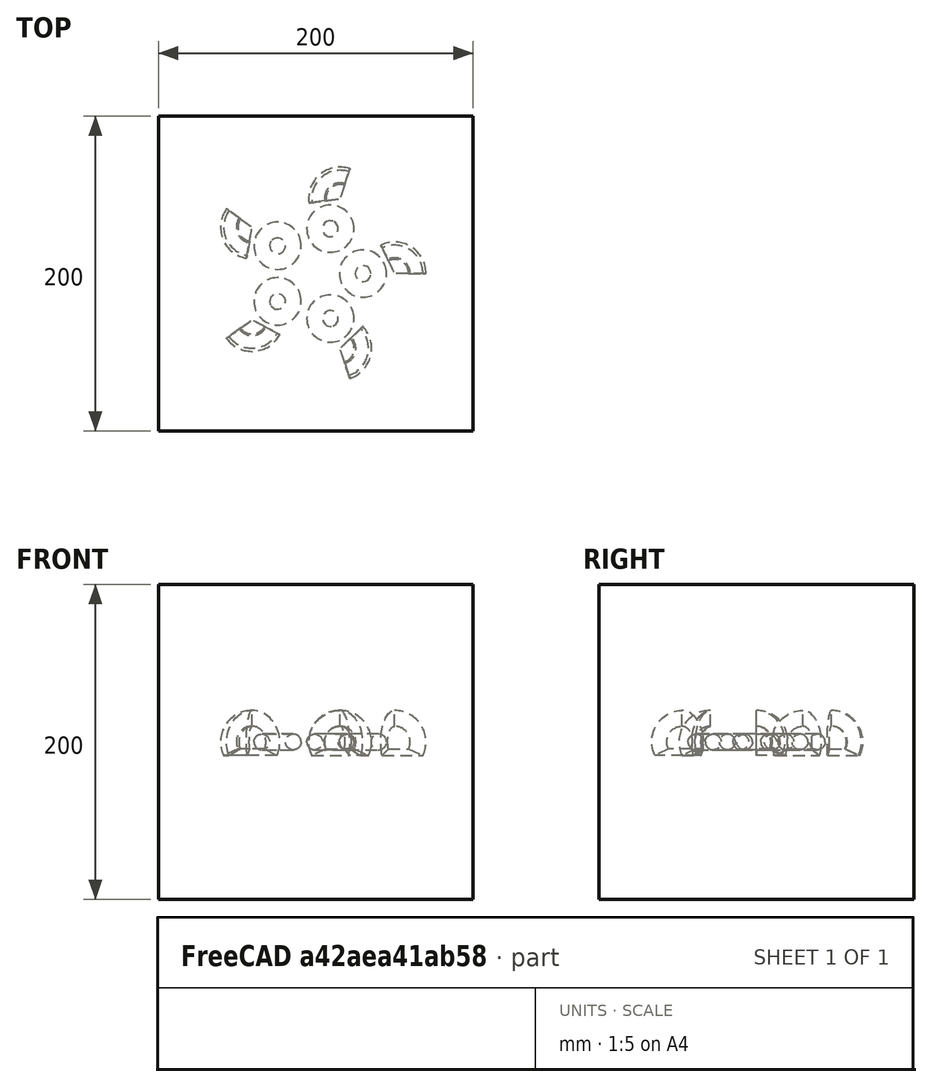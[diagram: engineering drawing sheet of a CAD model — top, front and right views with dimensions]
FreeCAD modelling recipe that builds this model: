
FCSTD DOCUMENT  (FreeCAD 0.19RUnknown)
Label: polarArray
License: All rights reserved
LicenseURL: http://en.wikipedia.org/wiki/All_rights_reserved
objects: App::DocumentObjectGroupPython×1248, Part::FeaturePython×4, App::Part×2, Part::MultiFuse×1
note: 5 computed .brp shape members not serialized (recipe doc carries the construction recipe); baked Part::Feature solids carry a one-line shape summary decoded from their .brp

FEATURE [App::DocumentObjectGroupPython] HALFPI  # scripted group (container) (typed FeaturePython)
  name = HALFPI
  value = pi/2.
FEATURE [App::DocumentObjectGroupPython] PI  # scripted group (container) (typed FeaturePython)
  name = PI
  value = 1.*pi
FEATURE [App::DocumentObjectGroupPython] TWOPI  # scripted group (container) (typed FeaturePython)
  name = TWOPI
  value = 2.*pi
FEATURE [App::DocumentObjectGroupPython] Constants  # scripted group (container) (typed FeaturePython)
  Group = -> [HALFPI,PI,TWOPI]
FEATURE [App::DocumentObjectGroupPython] Variables  # scripted group (container) (typed FeaturePython)
FEATURE [App::DocumentObjectGroupPython] Quantities  # scripted group (container) (typed FeaturePython)
FEATURE [App::DocumentObjectGroupPython] Isotopes  # scripted group (container) (typed FeaturePython)
FEATURE [App::DocumentObjectGroupPython] Elements  # scripted group (container) (typed FeaturePython)
FEATURE [App::DocumentObjectGroupPython] G4Isotopes  # scripted group (container) (typed FeaturePython)
FEATURE [App::DocumentObjectGroupPython] H_element  # scripted group (container) (typed FeaturePython)
  Z = 1
  atom_value = 1.008
  formula = H
  name = H_element
FEATURE [App::DocumentObjectGroupPython] He_element  # scripted group (container) (typed FeaturePython)
  Z = 2
  atom_value = 4.0026
  formula = He
  name = He_element
FEATURE [App::DocumentObjectGroupPython] Li_element  # scripted group (container) (typed FeaturePython)
  Z = 3
  atom_value = 6.94
  formula = Li
  name = Li_element
FEATURE [App::DocumentObjectGroupPython] Be_element  # scripted group (container) (typed FeaturePython)
  Z = 4
  atom_value = 9.01218
  formula = Be
  name = Be_element
FEATURE [App::DocumentObjectGroupPython] B_element  # scripted group (container) (typed FeaturePython)
  Z = 5
  atom_value = 10.81
  formula = B
  name = B_element
FEATURE [App::DocumentObjectGroupPython] C_element  # scripted group (container) (typed FeaturePython)
  Z = 6
  atom_value = 12.011
  formula = C
  name = C_element
FEATURE [App::DocumentObjectGroupPython] N_element  # scripted group (container) (typed FeaturePython)
  Z = 7
  atom_value = 14.007
  formula = N
  name = N_element
FEATURE [App::DocumentObjectGroupPython] O_element  # scripted group (container) (typed FeaturePython)
  Z = 8
  atom_value = 15.999
  formula = O
  name = O_element
FEATURE [App::DocumentObjectGroupPython] F_element  # scripted group (container) (typed FeaturePython)
  Z = 9
  atom_value = 18.9984
  formula = F
  name = F_element
FEATURE [App::DocumentObjectGroupPython] Ne_element  # scripted group (container) (typed FeaturePython)
  Z = 10
  atom_value = 20.1797
  formula = Ne
  name = Ne_element
FEATURE [App::DocumentObjectGroupPython] Na_element  # scripted group (container) (typed FeaturePython)
  Z = 11
  atom_value = 22.9898
  formula = Na
  name = Na_element
FEATURE [App::DocumentObjectGroupPython] Mg_element  # scripted group (container) (typed FeaturePython)
  Z = 12
  atom_value = 24.305
  formula = Mg
  name = Mg_element
FEATURE [App::DocumentObjectGroupPython] Al_element  # scripted group (container) (typed FeaturePython)
  Z = 13
  atom_value = 26.9815
  formula = Al
  name = Al_element
FEATURE [App::DocumentObjectGroupPython] Si_element  # scripted group (container) (typed FeaturePython)
  Z = 14
  atom_value = 28.085
  formula = Si
  name = Si_element
FEATURE [App::DocumentObjectGroupPython] P_element  # scripted group (container) (typed FeaturePython)
  Z = 15
  atom_value = 30.9738
  formula = P
  name = P_element
FEATURE [App::DocumentObjectGroupPython] S_element  # scripted group (container) (typed FeaturePython)
  Z = 16
  atom_value = 32.06
  formula = S
  name = S_element
FEATURE [App::DocumentObjectGroupPython] Cl_element  # scripted group (container) (typed FeaturePython)
  Z = 17
  atom_value = 35.45
  formula = Cl
  name = Cl_element
FEATURE [App::DocumentObjectGroupPython] Ar_element  # scripted group (container) (typed FeaturePython)
  Z = 18
  atom_value = 39.95
  formula = Ar
  name = Ar_element
FEATURE [App::DocumentObjectGroupPython] K_element  # scripted group (container) (typed FeaturePython)
  Z = 19
  atom_value = 39.0983
  formula = K
  name = K_element
FEATURE [App::DocumentObjectGroupPython] Ca_element  # scripted group (container) (typed FeaturePython)
  Z = 20
  atom_value = 40.078
  formula = Ca
  name = Ca_element
FEATURE [App::DocumentObjectGroupPython] Sc_element  # scripted group (container) (typed FeaturePython)
  Z = 21
  atom_value = 44.9559
  formula = Sc
  name = Sc_element
FEATURE [App::DocumentObjectGroupPython] Ti_element  # scripted group (container) (typed FeaturePython)
  Z = 22
  atom_value = 47.867
  formula = Ti
  name = Ti_element
FEATURE [App::DocumentObjectGroupPython] V_element  # scripted group (container) (typed FeaturePython)
  Z = 23
  atom_value = 50.9415
  formula = V
  name = V_element
FEATURE [App::DocumentObjectGroupPython] Cr_element  # scripted group (container) (typed FeaturePython)
  Z = 24
  atom_value = 51.9961
  formula = Cr
  name = Cr_element
FEATURE [App::DocumentObjectGroupPython] Mn_element  # scripted group (container) (typed FeaturePython)
  Z = 25
  atom_value = 54.938
  formula = Mn
  name = Mn_element
FEATURE [App::DocumentObjectGroupPython] Fe_element  # scripted group (container) (typed FeaturePython)
  Z = 26
  atom_value = 55.845
  formula = Fe
  name = Fe_element
FEATURE [App::DocumentObjectGroupPython] Co_element  # scripted group (container) (typed FeaturePython)
  Z = 27
  atom_value = 58.9332
  formula = Co
  name = Co_element
FEATURE [App::DocumentObjectGroupPython] Ni_element  # scripted group (container) (typed FeaturePython)
  Z = 28
  atom_value = 58.6934
  formula = Ni
  name = Ni_element
FEATURE [App::DocumentObjectGroupPython] Cu_element  # scripted group (container) (typed FeaturePython)
  Z = 29
  atom_value = 63.546
  formula = Cu
  name = Cu_element
FEATURE [App::DocumentObjectGroupPython] Zn_element  # scripted group (container) (typed FeaturePython)
  Z = 30
  atom_value = 65.38
  formula = Zn
  name = Zn_element
FEATURE [App::DocumentObjectGroupPython] Ga_element  # scripted group (container) (typed FeaturePython)
  Z = 31
  atom_value = 69.723
  formula = Ga
  name = Ga_element
FEATURE [App::DocumentObjectGroupPython] Ge_element  # scripted group (container) (typed FeaturePython)
  Z = 32
  atom_value = 72.63
  formula = Ge
  name = Ge_element
FEATURE [App::DocumentObjectGroupPython] As_element  # scripted group (container) (typed FeaturePython)
  Z = 33
  atom_value = 74.9216
  formula = As
  name = As_element
FEATURE [App::DocumentObjectGroupPython] Se_element  # scripted group (container) (typed FeaturePython)
  Z = 34
  atom_value = 78.971
  formula = Se
  name = Se_element
FEATURE [App::DocumentObjectGroupPython] Br_element  # scripted group (container) (typed FeaturePython)
  Z = 35
  atom_value = 79.904
  formula = Br
  name = Br_element
FEATURE [App::DocumentObjectGroupPython] Kr_element  # scripted group (container) (typed FeaturePython)
  Z = 36
  atom_value = 83.798
  formula = Kr
  name = Kr_element
FEATURE [App::DocumentObjectGroupPython] Rb_element  # scripted group (container) (typed FeaturePython)
  Z = 37
  atom_value = 85.4678
  formula = Rb
  name = Rb_element
FEATURE [App::DocumentObjectGroupPython] Sr_element  # scripted group (container) (typed FeaturePython)
  Z = 38
  atom_value = 87.62
  formula = Sr
  name = Sr_element
FEATURE [App::DocumentObjectGroupPython] Y_element  # scripted group (container) (typed FeaturePython)
  Z = 39
  atom_value = 88.9058
  formula = Y
  name = Y_element
FEATURE [App::DocumentObjectGroupPython] Zr_element  # scripted group (container) (typed FeaturePython)
  Z = 40
  atom_value = 91.224
  formula = Zr
  name = Zr_element
FEATURE [App::DocumentObjectGroupPython] Nb_element  # scripted group (container) (typed FeaturePython)
  Z = 41
  atom_value = 92.9064
  formula = Nb
  name = Nb_element
FEATURE [App::DocumentObjectGroupPython] Mo_element  # scripted group (container) (typed FeaturePython)
  Z = 42
  atom_value = 95.95
  formula = Mo
  name = Mo_element
FEATURE [App::DocumentObjectGroupPython] Tc_element  # scripted group (container) (typed FeaturePython)
  Z = 43
  atom_value = 97
  formula = Tc
  name = Tc_element
FEATURE [App::DocumentObjectGroupPython] Ru_element  # scripted group (container) (typed FeaturePython)
  Z = 44
  atom_value = 101.07
  formula = Ru
  name = Ru_element
FEATURE [App::DocumentObjectGroupPython] Rh_element  # scripted group (container) (typed FeaturePython)
  Z = 45
  atom_value = 102.905
  formula = Rh
  name = Rh_element
FEATURE [App::DocumentObjectGroupPython] Pd_element  # scripted group (container) (typed FeaturePython)
  Z = 46
  atom_value = 106.42
  formula = Pd
  name = Pd_element
FEATURE [App::DocumentObjectGroupPython] Ag_element  # scripted group (container) (typed FeaturePython)
  Z = 47
  atom_value = 107.868
  formula = Ag
  name = Ag_element
FEATURE [App::DocumentObjectGroupPython] Cd_element  # scripted group (container) (typed FeaturePython)
  Z = 48
  atom_value = 112.414
  formula = Cd
  name = Cd_element
FEATURE [App::DocumentObjectGroupPython] In_element  # scripted group (container) (typed FeaturePython)
  Z = 49
  atom_value = 114.818
  formula = In
  name = In_element
FEATURE [App::DocumentObjectGroupPython] Sn_element  # scripted group (container) (typed FeaturePython)
  Z = 50
  atom_value = 118.71
  formula = Sn
  name = Sn_element
FEATURE [App::DocumentObjectGroupPython] Sb_element  # scripted group (container) (typed FeaturePython)
  Z = 51
  atom_value = 121.76
  formula = Sb
  name = Sb_element
FEATURE [App::DocumentObjectGroupPython] Te_element  # scripted group (container) (typed FeaturePython)
  Z = 52
  atom_value = 127.6
  formula = Te
  name = Te_element
FEATURE [App::DocumentObjectGroupPython] I_element  # scripted group (container) (typed FeaturePython)
  Z = 53
  atom_value = 126.904
  formula = I
  name = I_element
FEATURE [App::DocumentObjectGroupPython] Xe_element  # scripted group (container) (typed FeaturePython)
  Z = 54
  atom_value = 131.293
  formula = Xe
  name = Xe_element
FEATURE [App::DocumentObjectGroupPython] Cs_element  # scripted group (container) (typed FeaturePython)
  Z = 55
  atom_value = 132.905
  formula = Cs
  name = Cs_element
FEATURE [App::DocumentObjectGroupPython] Ba_element  # scripted group (container) (typed FeaturePython)
  Z = 56
  atom_value = 137.327
  formula = Ba
  name = Ba_element
FEATURE [App::DocumentObjectGroupPython] La_element  # scripted group (container) (typed FeaturePython)
  Z = 57
  atom_value = 138.905
  formula = La
  name = La_element
FEATURE [App::DocumentObjectGroupPython] Ce_element  # scripted group (container) (typed FeaturePython)
  Z = 58
  atom_value = 140.116
  formula = Ce
  name = Ce_element
FEATURE [App::DocumentObjectGroupPython] Pr_element  # scripted group (container) (typed FeaturePython)
  Z = 59
  atom_value = 140.908
  formula = Pr
  name = Pr_element
FEATURE [App::DocumentObjectGroupPython] Nd_element  # scripted group (container) (typed FeaturePython)
  Z = 60
  atom_value = 144.242
  formula = Nd
  name = Nd_element
FEATURE [App::DocumentObjectGroupPython] Pm_element  # scripted group (container) (typed FeaturePython)
  Z = 61
  atom_value = 145
  formula = Pm
  name = Pm_element
FEATURE [App::DocumentObjectGroupPython] Sm_element  # scripted group (container) (typed FeaturePython)
  Z = 62
  atom_value = 150.36
  formula = Sm
  name = Sm_element
FEATURE [App::DocumentObjectGroupPython] Eu_element  # scripted group (container) (typed FeaturePython)
  Z = 63
  atom_value = 151.964
  formula = Eu
  name = Eu_element
FEATURE [App::DocumentObjectGroupPython] Gd_element  # scripted group (container) (typed FeaturePython)
  Z = 64
  atom_value = 157.25
  formula = Gd
  name = Gd_element
FEATURE [App::DocumentObjectGroupPython] Tb_element  # scripted group (container) (typed FeaturePython)
  Z = 65
  atom_value = 158.925
  formula = Tb
  name = Tb_element
FEATURE [App::DocumentObjectGroupPython] Dy_element  # scripted group (container) (typed FeaturePython)
  Z = 66
  atom_value = 162.5
  formula = Dy
  name = Dy_element
FEATURE [App::DocumentObjectGroupPython] Ho_element  # scripted group (container) (typed FeaturePython)
  Z = 67
  atom_value = 164.93
  formula = Ho
  name = Ho_element
FEATURE [App::DocumentObjectGroupPython] Er_element  # scripted group (container) (typed FeaturePython)
  Z = 68
  atom_value = 167.259
  formula = Er
  name = Er_element
FEATURE [App::DocumentObjectGroupPython] Tm_element  # scripted group (container) (typed FeaturePython)
  Z = 69
  atom_value = 168.934
  formula = Tm
  name = Tm_element
FEATURE [App::DocumentObjectGroupPython] Yb_element  # scripted group (container) (typed FeaturePython)
  Z = 70
  atom_value = 173.045
  formula = Yb
  name = Yb_element
FEATURE [App::DocumentObjectGroupPython] Lu_element  # scripted group (container) (typed FeaturePython)
  Z = 71
  atom_value = 174.967
  formula = Lu
  name = Lu_element
FEATURE [App::DocumentObjectGroupPython] Hf_element  # scripted group (container) (typed FeaturePython)
  Z = 72
  atom_value = 178.49
  formula = Hf
  name = Hf_element
FEATURE [App::DocumentObjectGroupPython] Ta_element  # scripted group (container) (typed FeaturePython)
  Z = 73
  atom_value = 180.948
  formula = Ta
  name = Ta_element
FEATURE [App::DocumentObjectGroupPython] W_element  # scripted group (container) (typed FeaturePython)
  Z = 74
  atom_value = 183.84
  formula = W
  name = W_element
FEATURE [App::DocumentObjectGroupPython] Re_element  # scripted group (container) (typed FeaturePython)
  Z = 75
  atom_value = 186.207
  formula = Re
  name = Re_element
FEATURE [App::DocumentObjectGroupPython] Os_element  # scripted group (container) (typed FeaturePython)
  Z = 76
  atom_value = 190.23
  formula = Os
  name = Os_element
FEATURE [App::DocumentObjectGroupPython] Ir_element  # scripted group (container) (typed FeaturePython)
  Z = 77
  atom_value = 192.217
  formula = Ir
  name = Ir_element
FEATURE [App::DocumentObjectGroupPython] Pt_element  # scripted group (container) (typed FeaturePython)
  Z = 78
  atom_value = 195.084
  formula = Pt
  name = Pt_element
FEATURE [App::DocumentObjectGroupPython] Au_element  # scripted group (container) (typed FeaturePython)
  Z = 79
  atom_value = 196.967
  formula = Au
  name = Au_element
FEATURE [App::DocumentObjectGroupPython] Hg_element  # scripted group (container) (typed FeaturePython)
  Z = 80
  atom_value = 200.592
  formula = Hg
  name = Hg_element
FEATURE [App::DocumentObjectGroupPython] Tl_element  # scripted group (container) (typed FeaturePython)
  Z = 81
  atom_value = 204.38
  formula = Tl
  name = Tl_element
FEATURE [App::DocumentObjectGroupPython] Pb_element  # scripted group (container) (typed FeaturePython)
  Z = 82
  atom_value = 207.2
  formula = Pb
  name = Pb_element
FEATURE [App::DocumentObjectGroupPython] Bi_element  # scripted group (container) (typed FeaturePython)
  Z = 83
  atom_value = 208.98
  formula = Bi
  name = Bi_element
FEATURE [App::DocumentObjectGroupPython] Po_element  # scripted group (container) (typed FeaturePython)
  Z = 84
  atom_value = 209
  formula = Po
  name = Po_element
FEATURE [App::DocumentObjectGroupPython] At_element  # scripted group (container) (typed FeaturePython)
  Z = 85
  atom_value = 210
  formula = At
  name = At_element
FEATURE [App::DocumentObjectGroupPython] Rn_element  # scripted group (container) (typed FeaturePython)
  Z = 86
  atom_value = 222
  formula = Rn
  name = Rn_element
FEATURE [App::DocumentObjectGroupPython] Fr_element  # scripted group (container) (typed FeaturePython)
  Z = 87
  atom_value = 223
  formula = Fr
  name = Fr_element
FEATURE [App::DocumentObjectGroupPython] Ra_element  # scripted group (container) (typed FeaturePython)
  Z = 88
  atom_value = 226
  formula = Ra
  name = Ra_element
FEATURE [App::DocumentObjectGroupPython] Ac_element  # scripted group (container) (typed FeaturePython)
  Z = 89
  atom_value = 227
  formula = Ac
  name = Ac_element
FEATURE [App::DocumentObjectGroupPython] Th_element  # scripted group (container) (typed FeaturePython)
  Z = 90
  atom_value = 232.038
  formula = Th
  name = Th_element
FEATURE [App::DocumentObjectGroupPython] Pa_element  # scripted group (container) (typed FeaturePython)
  Z = 91
  atom_value = 231.036
  formula = Pa
  name = Pa_element
FEATURE [App::DocumentObjectGroupPython] U_element  # scripted group (container) (typed FeaturePython)
  Z = 92
  atom_value = 238.029
  formula = U
  name = U_element
FEATURE [App::DocumentObjectGroupPython] Np_element  # scripted group (container) (typed FeaturePython)
  Z = 93
  atom_value = 237
  formula = Np
  name = Np_element
FEATURE [App::DocumentObjectGroupPython] Pu_element  # scripted group (container) (typed FeaturePython)
  Z = 94
  atom_value = 244
  formula = Pu
  name = Pu_element
FEATURE [App::DocumentObjectGroupPython] Am_element  # scripted group (container) (typed FeaturePython)
  Z = 95
  atom_value = 243
  formula = Am
  name = Am_element
FEATURE [App::DocumentObjectGroupPython] Cm_element  # scripted group (container) (typed FeaturePython)
  Z = 96
  atom_value = 247
  formula = Cm
  name = Cm_element
FEATURE [App::DocumentObjectGroupPython] Bk_element  # scripted group (container) (typed FeaturePython)
  Z = 97
  atom_value = 247
  formula = Bk
  name = Bk_element
FEATURE [App::DocumentObjectGroupPython] Cf_element  # scripted group (container) (typed FeaturePython)
  Z = 98
  atom_value = 251
  formula = Cf
  name = Cf_element
FEATURE [App::DocumentObjectGroupPython] G4Elements  # scripted group (container) (typed FeaturePython)
  Group = -> [H_element,He_element,Li_element,Be_element,B_element,C_element,N_element,O_element,F_element,Ne_element,Na_element,Mg_element,Al_element,Si_element,P_element,S_element,Cl_element,Ar_element,K_element,Ca_element,Sc_element,Ti_element,V_element,Cr_element,Mn_element,Fe_element,Co_element,Ni_element,Cu_element,Zn_element,Ga_element,Ge_element,As_element,Se_element,Br_element,Kr_element,Rb_element,+61 more]
FEATURE [App::DocumentObjectGroupPython] H_element001  label="H_element : 0.101"  # scripted group (container) (typed FeaturePython)
  n = 0.101327
FEATURE [App::DocumentObjectGroupPython] C_element001  label="C_element : 0.775"  # scripted group (container) (typed FeaturePython)
  n = 0.7755
FEATURE [App::DocumentObjectGroupPython] N_element001  label="N_element : 0.035"  # scripted group (container) (typed FeaturePython)
  n = 0.035057
FEATURE [App::DocumentObjectGroupPython] O_element001  label="O_element : 0.052"  # scripted group (container) (typed FeaturePython)
  n = 0.0523159
FEATURE [App::DocumentObjectGroupPython] F_element001  label="F_element : 0.017"  # scripted group (container) (typed FeaturePython)
  n = 0.017422
FEATURE [App::DocumentObjectGroupPython] Ca_element001  label="Ca_element : 0.018"  # scripted group (container) (typed FeaturePython)
  n = 0.018378
FEATURE [App::DocumentObjectGroupPython] G4_A_150_TISSUE  label="G4_A-150_TISSUE"  # scripted group (container) (typed FeaturePython)
  Dunit = g/cm3
  Dvalue = 1.127
  Group = -> [H_element001,C_element001,N_element001,O_element001,F_element001,Ca_element001]
  conduct = 2
  density = 1
  expand = 3
  formula = G4_A-150_TISSUE
  name = G4_A-150_TISSUE
  specific = 4
FEATURE [App::DocumentObjectGroupPython] C_element002  label="C_element : 3"  # scripted group (container) (typed FeaturePython)
  n = 3
  ref = C_element
FEATURE [App::DocumentObjectGroupPython] H_element002  label="H_element : 6"  # scripted group (container) (typed FeaturePython)
  n = 6
  ref = H_element
FEATURE [App::DocumentObjectGroupPython] O_element002  label="O_element : 1"  # scripted group (container) (typed FeaturePython)
  n = 1
  ref = O_element
FEATURE [App::DocumentObjectGroupPython] G4_ACETONE  # scripted group (container) (typed FeaturePython)
  Dunit = g/cm3
  Dvalue = 0.7899
  Group = -> [C_element002,H_element002,O_element002]
  conduct = 2
  density = 1
  expand = 3
  formula = G4_ACETONE
  name = G4_ACETONE
  specific = 4
FEATURE [App::DocumentObjectGroupPython] C_element003  label="C_element : 2"  # scripted group (container) (typed FeaturePython)
  n = 2
  ref = C_element
FEATURE [App::DocumentObjectGroupPython] H_element003  label="H_element : 2"  # scripted group (container) (typed FeaturePython)
  n = 2
  ref = H_element
FEATURE [App::DocumentObjectGroupPython] G4_ACETYLENE  # scripted group (container) (typed FeaturePython)
  Dunit = g/cm3
  Dvalue = 0.0010967
  Group = -> [C_element003,H_element003]
  conduct = 2
  density = 1
  expand = 3
  formula = G4_ACETYLENE
  name = G4_ACETYLENE
  specific = 4
FEATURE [App::DocumentObjectGroupPython] C_element004  label="C_element : 5"  # scripted group (container) (typed FeaturePython)
  n = 5
  ref = C_element
FEATURE [App::DocumentObjectGroupPython] H_element004  label="H_element : 5"  # scripted group (container) (typed FeaturePython)
  n = 5
  ref = H_element
FEATURE [App::DocumentObjectGroupPython] N_element002  label="N_element : 5"  # scripted group (container) (typed FeaturePython)
  n = 5
  ref = N_element
FEATURE [App::DocumentObjectGroupPython] G4_ADENINE  # scripted group (container) (typed FeaturePython)
  Dunit = g/cm3
  Dvalue = 1.6
  Group = -> [C_element004,H_element004,N_element002]
  conduct = 2
  density = 1
  expand = 3
  formula = G4_ADENINE
  name = G4_ADENINE
  specific = 4
FEATURE [App::DocumentObjectGroupPython] H_element005  label="H_element : 0.114"  # scripted group (container) (typed FeaturePython)
  n = 0.114
FEATURE [App::DocumentObjectGroupPython] C_element005  label="C_element : 0.598"  # scripted group (container) (typed FeaturePython)
  n = 0.598
FEATURE [App::DocumentObjectGroupPython] N_element003  label="N_element : 0.007"  # scripted group (container) (typed FeaturePython)
  n = 0.007
FEATURE [App::DocumentObjectGroupPython] O_element003  label="O_element : 0.278"  # scripted group (container) (typed FeaturePython)
  n = 0.278
FEATURE [App::DocumentObjectGroupPython] Na_element001  label="Na_element : 0.001"  # scripted group (container) (typed FeaturePython)
  n = 0.001
FEATURE [App::DocumentObjectGroupPython] S_element001  label="S_element : 0.001"  # scripted group (container) (typed FeaturePython)
  n = 0.001
FEATURE [App::DocumentObjectGroupPython] Cl_element001  label="Cl_element : 0.001"  # scripted group (container) (typed FeaturePython)
  n = 0.001
FEATURE [App::DocumentObjectGroupPython] G4_ADIPOSE_TISSUE_ICRP  # scripted group (container) (typed FeaturePython)
  Dunit = g/cm3
  Dvalue = 0.95
  Group = -> [H_element005,C_element005,N_element003,O_element003,Na_element001,S_element001,Cl_element001]
  conduct = 2
  density = 1
  expand = 3
  formula = G4_ADIPOSE_TISSUE_ICRP
  name = G4_ADIPOSE_TISSUE_ICRP
  specific = 4
FEATURE [App::DocumentObjectGroupPython] C_element006  label="C_element : 0.000"  # scripted group (container) (typed FeaturePython)
  n = 0.000124
FEATURE [App::DocumentObjectGroupPython] N_element004  label="N_element : 0.755"  # scripted group (container) (typed FeaturePython)
  n = 0.755268
FEATURE [App::DocumentObjectGroupPython] O_element004  label="O_element : 0.232"  # scripted group (container) (typed FeaturePython)
  n = 0.231781
FEATURE [App::DocumentObjectGroupPython] Ar_element001  label="Ar_element : 0.013"  # scripted group (container) (typed FeaturePython)
  n = 0.012827
FEATURE [App::DocumentObjectGroupPython] G4_AIR  # scripted group (container) (typed FeaturePython)
  Dunit = g/cm3
  Dvalue = 0.00120479
  Group = -> [C_element006,N_element004,O_element004,Ar_element001]
  conduct = 2
  density = 1
  expand = 3
  formula = G4_AIR
  name = G4_AIR
  specific = 4
FEATURE [App::DocumentObjectGroupPython] C_element007  label="C_element : 006"  # scripted group (container) (typed FeaturePython)
  n = 3
  ref = C_element
FEATURE [App::DocumentObjectGroupPython] H_element006  label="H_element : 7"  # scripted group (container) (typed FeaturePython)
  n = 7
  ref = H_element
FEATURE [App::DocumentObjectGroupPython] N_element005  label="N_element : 1"  # scripted group (container) (typed FeaturePython)
  n = 1
  ref = N_element
FEATURE [App::DocumentObjectGroupPython] O_element005  label="O_element : 2"  # scripted group (container) (typed FeaturePython)
  n = 2
  ref = O_element
FEATURE [App::DocumentObjectGroupPython] G4_ALANINE  # scripted group (container) (typed FeaturePython)
  Dunit = g/cm3
  Dvalue = 1.42
  Group = -> [C_element007,H_element006,N_element005,O_element005]
  conduct = 2
  density = 1
  expand = 3
  formula = G4_ALANINE
  name = G4_ALANINE
  specific = 4
FEATURE [App::DocumentObjectGroupPython] Al_element001  label="Al_element : 2"  # scripted group (container) (typed FeaturePython)
  n = 2
  ref = Al_element
FEATURE [App::DocumentObjectGroupPython] O_element006  label="O_element : 3"  # scripted group (container) (typed FeaturePython)
  n = 3
  ref = O_element
FEATURE [App::DocumentObjectGroupPython] G4_ALUMINUM_OXIDE  # scripted group (container) (typed FeaturePython)
  Dunit = g/cm3
  Dvalue = 3.97
  Group = -> [Al_element001,O_element006]
  conduct = 2
  density = 1
  expand = 3
  formula = G4_ALUMINUM_OXIDE
  name = G4_ALUMINUM_OXIDE
  specific = 4
FEATURE [App::DocumentObjectGroupPython] H_element007  label="H_element : 0.106"  # scripted group (container) (typed FeaturePython)
  n = 0.10593
FEATURE [App::DocumentObjectGroupPython] C_element008  label="C_element : 0.789"  # scripted group (container) (typed FeaturePython)
  n = 0.788974
FEATURE [App::DocumentObjectGroupPython] O_element007  label="O_element : 0.105"  # scripted group (container) (typed FeaturePython)
  n = 0.105096
FEATURE [App::DocumentObjectGroupPython] G4_AMBER  # scripted group (container) (typed FeaturePython)
  Dunit = g/cm3
  Dvalue = 1.1
  Group = -> [H_element007,C_element008,O_element007]
  conduct = 2
  density = 1
  expand = 3
  formula = G4_AMBER
  name = G4_AMBER
  specific = 4
FEATURE [App::DocumentObjectGroupPython] N_element006  label="N_element : 006"  # scripted group (container) (typed FeaturePython)
  n = 1
  ref = N_element
FEATURE [App::DocumentObjectGroupPython] H_element008  label="H_element : 3"  # scripted group (container) (typed FeaturePython)
  n = 3
  ref = H_element
FEATURE [App::DocumentObjectGroupPython] G4_AMMONIA  # scripted group (container) (typed FeaturePython)
  Dunit = g/cm3
  Dvalue = 0.000826019
  Group = -> [N_element006,H_element008]
  conduct = 2
  density = 1
  expand = 3
  formula = G4_AMMONIA
  name = G4_AMMONIA
  specific = 4
FEATURE [App::DocumentObjectGroupPython] C_element009  label="C_element : 6"  # scripted group (container) (typed FeaturePython)
  n = 6
  ref = C_element
FEATURE [App::DocumentObjectGroupPython] H_element009  label="H_element : 008"  # scripted group (container) (typed FeaturePython)
  n = 7
  ref = H_element
FEATURE [App::DocumentObjectGroupPython] N_element007  label="N_element : 007"  # scripted group (container) (typed FeaturePython)
  n = 1
  ref = N_element
FEATURE [App::DocumentObjectGroupPython] G4_ANILINE  # scripted group (container) (typed FeaturePython)
  Dunit = g/cm3
  Dvalue = 1.0235
  Group = -> [C_element009,H_element009,N_element007]
  conduct = 2
  density = 1
  expand = 3
  formula = G4_ANILINE
  name = G4_ANILINE
  specific = 4
FEATURE [App::DocumentObjectGroupPython] C_element010  label="C_element : 14"  # scripted group (container) (typed FeaturePython)
  n = 14
  ref = C_element
FEATURE [App::DocumentObjectGroupPython] H_element010  label="H_element : 10"  # scripted group (container) (typed FeaturePython)
  n = 10
  ref = H_element
FEATURE [App::DocumentObjectGroupPython] G4_ANTHRACENE  # scripted group (container) (typed FeaturePython)
  Dunit = g/cm3
  Dvalue = 1.283
  Group = -> [C_element010,H_element010]
  conduct = 2
  density = 1
  expand = 3
  formula = G4_ANTHRACENE
  name = G4_ANTHRACENE
  specific = 4
FEATURE [App::DocumentObjectGroupPython] H_element011  label="H_element : 0.065"  # scripted group (container) (typed FeaturePython)
  n = 0.0654709
FEATURE [App::DocumentObjectGroupPython] C_element011  label="C_element : 0.537"  # scripted group (container) (typed FeaturePython)
  n = 0.536944
FEATURE [App::DocumentObjectGroupPython] N_element008  label="N_element : 0.021"  # scripted group (container) (typed FeaturePython)
  n = 0.0215
FEATURE [App::DocumentObjectGroupPython] O_element008  label="O_element : 0.032"  # scripted group (container) (typed FeaturePython)
  n = 0.032085
FEATURE [App::DocumentObjectGroupPython] F_element002  label="F_element : 0.167"  # scripted group (container) (typed FeaturePython)
  n = 0.167411
FEATURE [App::DocumentObjectGroupPython] Ca_element002  label="Ca_element : 0.177"  # scripted group (container) (typed FeaturePython)
  n = 0.176589
FEATURE [App::DocumentObjectGroupPython] G4_B_100_BONE  label="G4_B-100_BONE"  # scripted group (container) (typed FeaturePython)
  Dunit = g/cm3
  Dvalue = 1.45
  Group = -> [H_element011,C_element011,N_element008,O_element008,F_element002,Ca_element002]
  conduct = 2
  density = 1
  expand = 3
  formula = G4_B-100_BONE
  name = G4_B-100_BONE
  specific = 4
FEATURE [App::DocumentObjectGroupPython] H_element012  label="H_element : 0.057"  # scripted group (container) (typed FeaturePython)
  n = 0.057441
FEATURE [App::DocumentObjectGroupPython] C_element012  label="C_element : 0.790"  # scripted group (container) (typed FeaturePython)
  n = 0.774591
FEATURE [App::DocumentObjectGroupPython] O_element009  label="O_element : 0.168"  # scripted group (container) (typed FeaturePython)
  n = 0.167968
FEATURE [App::DocumentObjectGroupPython] G4_BAKELITE  # scripted group (container) (typed FeaturePython)
  Dunit = g/cm3
  Dvalue = 1.25
  Group = -> [H_element012,C_element012,O_element009]
  conduct = 2
  density = 1
  expand = 3
  formula = G4_BAKELITE
  name = G4_BAKELITE
  specific = 4
FEATURE [App::DocumentObjectGroupPython] Ba_element001  label="Ba_element : 1"  # scripted group (container) (typed FeaturePython)
  n = 1
  ref = Ba_element
FEATURE [App::DocumentObjectGroupPython] F_element003  label="F_element : 2"  # scripted group (container) (typed FeaturePython)
  n = 2
  ref = F_element
FEATURE [App::DocumentObjectGroupPython] G4_BARIUM_FLUORIDE  # scripted group (container) (typed FeaturePython)
  Dunit = g/cm3
  Dvalue = 4.89
  Group = -> [Ba_element001,F_element003]
  conduct = 2
  density = 1
  expand = 3
  formula = G4_BARIUM_FLUORIDE
  name = G4_BARIUM_FLUORIDE
  specific = 4
FEATURE [App::DocumentObjectGroupPython] Ba_element002  label="Ba_element : 002"  # scripted group (container) (typed FeaturePython)
  n = 1
  ref = Ba_element
FEATURE [App::DocumentObjectGroupPython] S_element002  label="S_element : 1"  # scripted group (container) (typed FeaturePython)
  n = 1
  ref = S_element
FEATURE [App::DocumentObjectGroupPython] O_element010  label="O_element : 4"  # scripted group (container) (typed FeaturePython)
  n = 4
  ref = O_element
FEATURE [App::DocumentObjectGroupPython] G4_BARIUM_SULFATE  # scripted group (container) (typed FeaturePython)
  Dunit = g/cm3
  Dvalue = 4.5
  Group = -> [Ba_element002,S_element002,O_element010]
  conduct = 2
  density = 1
  expand = 3
  formula = G4_BARIUM_SULFATE
  name = G4_BARIUM_SULFATE
  specific = 4
FEATURE [App::DocumentObjectGroupPython] C_element013  label="C_element : 007"  # scripted group (container) (typed FeaturePython)
  n = 6
  ref = C_element
FEATURE [App::DocumentObjectGroupPython] H_element013  label="H_element : 009"  # scripted group (container) (typed FeaturePython)
  n = 6
  ref = H_element
FEATURE [App::DocumentObjectGroupPython] G4_BENZENE  # scripted group (container) (typed FeaturePython)
  Dunit = g/cm3
  Dvalue = 0.87865
  Group = -> [C_element013,H_element013]
  conduct = 2
  density = 1
  expand = 3
  formula = G4_BENZENE
  name = G4_BENZENE
  specific = 4
FEATURE [App::DocumentObjectGroupPython] Be_element001  label="Be_element : 1"  # scripted group (container) (typed FeaturePython)
  n = 1
  ref = Be_element
FEATURE [App::DocumentObjectGroupPython] O_element011  label="O_element : 005"  # scripted group (container) (typed FeaturePython)
  n = 1
  ref = O_element
FEATURE [App::DocumentObjectGroupPython] G4_BERYLLIUM_OXIDE  # scripted group (container) (typed FeaturePython)
  Dunit = g/cm3
  Dvalue = 3.01
  Group = -> [Be_element001,O_element011]
  conduct = 2
  density = 1
  expand = 3
  formula = G4_BERYLLIUM_OXIDE
  name = G4_BERYLLIUM_OXIDE
  specific = 4
FEATURE [App::DocumentObjectGroupPython] Bi_element001  label="Bi_element : 4"  # scripted group (container) (typed FeaturePython)
  n = 4
  ref = Bi_element
FEATURE [App::DocumentObjectGroupPython] Ge_element001  label="Ge_element : 3"  # scripted group (container) (typed FeaturePython)
  n = 3
  ref = Ge_element
FEATURE [App::DocumentObjectGroupPython] O_element012  label="O_element : 12"  # scripted group (container) (typed FeaturePython)
  n = 12
  ref = O_element
FEATURE [App::DocumentObjectGroupPython] G4_BGO  # scripted group (container) (typed FeaturePython)
  Dunit = g/cm3
  Dvalue = 7.13
  Group = -> [Bi_element001,Ge_element001,O_element012]
  conduct = 2
  density = 1
  expand = 3
  formula = G4_BGO
  name = G4_BGO
  specific = 4
FEATURE [App::DocumentObjectGroupPython] H_element014  label="H_element : 0.102"  # scripted group (container) (typed FeaturePython)
  n = 0.102
FEATURE [App::DocumentObjectGroupPython] C_element014  label="C_element : 0.110"  # scripted group (container) (typed FeaturePython)
  n = 0.11
FEATURE [App::DocumentObjectGroupPython] N_element009  label="N_element : 0.033"  # scripted group (container) (typed FeaturePython)
  n = 0.033
FEATURE [App::DocumentObjectGroupPython] O_element013  label="O_element : 0.745"  # scripted group (container) (typed FeaturePython)
  n = 0.745
FEATURE [App::DocumentObjectGroupPython] Na_element002  label="Na_element : 0.002"  # scripted group (container) (typed FeaturePython)
  n = 0.001
FEATURE [App::DocumentObjectGroupPython] P_element001  label="P_element : 0.001"  # scripted group (container) (typed FeaturePython)
  n = 0.001
FEATURE [App::DocumentObjectGroupPython] S_element003  label="S_element : 0.002"  # scripted group (container) (typed FeaturePython)
  n = 0.002
FEATURE [App::DocumentObjectGroupPython] Cl_element002  label="Cl_element : 0.003"  # scripted group (container) (typed FeaturePython)
  n = 0.003
FEATURE [App::DocumentObjectGroupPython] K_element001  label="K_element : 0.002"  # scripted group (container) (typed FeaturePython)
  n = 0.002
FEATURE [App::DocumentObjectGroupPython] Fe_element001  label="Fe_element : 0.001"  # scripted group (container) (typed FeaturePython)
  n = 0.001
FEATURE [App::DocumentObjectGroupPython] G4_BLOOD_ICRP  # scripted group (container) (typed FeaturePython)
  Dunit = g/cm3
  Dvalue = 1.06
  Group = -> [H_element014,C_element014,N_element009,O_element013,Na_element002,P_element001,S_element003,Cl_element002,K_element001,Fe_element001]
  conduct = 2
  density = 1
  expand = 3
  formula = G4_BLOOD_ICRP
  name = G4_BLOOD_ICRP
  specific = 4
FEATURE [App::DocumentObjectGroupPython] H_element015  label="H_element : 0.064"  # scripted group (container) (typed FeaturePython)
  n = 0.064
FEATURE [App::DocumentObjectGroupPython] C_element015  label="C_element : 0.278"  # scripted group (container) (typed FeaturePython)
  n = 0.278
FEATURE [App::DocumentObjectGroupPython] N_element010  label="N_element : 0.027"  # scripted group (container) (typed FeaturePython)
  n = 0.027
FEATURE [App::DocumentObjectGroupPython] O_element014  label="O_element : 0.410"  # scripted group (container) (typed FeaturePython)
  n = 0.41
FEATURE [App::DocumentObjectGroupPython] Mg_element001  label="Mg_element : 0.002"  # scripted group (container) (typed FeaturePython)
  n = 0.002
FEATURE [App::DocumentObjectGroupPython] P_element002  label="P_element : 0.070"  # scripted group (container) (typed FeaturePython)
  n = 0.07
FEATURE [App::DocumentObjectGroupPython] S_element004  label="S_element : 0.003"  # scripted group (container) (typed FeaturePython)
  n = 0.002
FEATURE [App::DocumentObjectGroupPython] Ca_element003  label="Ca_element : 0.147"  # scripted group (container) (typed FeaturePython)
  n = 0.147
FEATURE [App::DocumentObjectGroupPython] G4_BONE_COMPACT_ICRU  # scripted group (container) (typed FeaturePython)
  Dunit = g/cm3
  Dvalue = 1.85
  Group = -> [H_element015,C_element015,N_element010,O_element014,Mg_element001,P_element002,S_element004,Ca_element003]
  conduct = 2
  density = 1
  expand = 3
  formula = G4_BONE_COMPACT_ICRU
  name = G4_BONE_COMPACT_ICRU
  specific = 4
FEATURE [App::DocumentObjectGroupPython] H_element016  label="H_element : 0.034"  # scripted group (container) (typed FeaturePython)
  n = 0.034
FEATURE [App::DocumentObjectGroupPython] C_element016  label="C_element : 0.155"  # scripted group (container) (typed FeaturePython)
  n = 0.155
FEATURE [App::DocumentObjectGroupPython] N_element011  label="N_element : 0.042"  # scripted group (container) (typed FeaturePython)
  n = 0.042
FEATURE [App::DocumentObjectGroupPython] O_element015  label="O_element : 0.435"  # scripted group (container) (typed FeaturePython)
  n = 0.435
FEATURE [App::DocumentObjectGroupPython] Na_element003  label="Na_element : 0.003"  # scripted group (container) (typed FeaturePython)
  n = 0.001
FEATURE [App::DocumentObjectGroupPython] Mg_element002  label="Mg_element : 0.003"  # scripted group (container) (typed FeaturePython)
  n = 0.002
FEATURE [App::DocumentObjectGroupPython] P_element003  label="P_element : 0.103"  # scripted group (container) (typed FeaturePython)
  n = 0.103
FEATURE [App::DocumentObjectGroupPython] S_element005  label="S_element : 0.004"  # scripted group (container) (typed FeaturePython)
  n = 0.003
FEATURE [App::DocumentObjectGroupPython] Ca_element004  label="Ca_element : 0.225"  # scripted group (container) (typed FeaturePython)
  n = 0.225
FEATURE [App::DocumentObjectGroupPython] G4_BONE_CORTICAL_ICRP  # scripted group (container) (typed FeaturePython)
  Dunit = g/cm3
  Dvalue = 1.92
  Group = -> [H_element016,C_element016,N_element011,O_element015,Na_element003,Mg_element002,P_element003,S_element005,Ca_element004]
  conduct = 2
  density = 1
  expand = 3
  formula = G4_BONE_CORTICAL_ICRP
  name = G4_BONE_CORTICAL_ICRP
  specific = 4
FEATURE [App::DocumentObjectGroupPython] B_element001  label="B_element : 4"  # scripted group (container) (typed FeaturePython)
  n = 4
  ref = B_element
FEATURE [App::DocumentObjectGroupPython] C_element017  label="C_element : 1"  # scripted group (container) (typed FeaturePython)
  n = 1
  ref = C_element
FEATURE [App::DocumentObjectGroupPython] G4_BORON_CARBIDE  # scripted group (container) (typed FeaturePython)
  Dunit = g/cm3
  Dvalue = 2.52
  Group = -> [B_element001,C_element017]
  conduct = 2
  density = 1
  expand = 3
  formula = G4_BORON_CARBIDE
  name = G4_BORON_CARBIDE
  specific = 4
FEATURE [App::DocumentObjectGroupPython] B_element002  label="B_element : 2"  # scripted group (container) (typed FeaturePython)
  n = 2
  ref = B_element
FEATURE [App::DocumentObjectGroupPython] O_element016  label="O_element : 006"  # scripted group (container) (typed FeaturePython)
  n = 3
  ref = O_element
FEATURE [App::DocumentObjectGroupPython] G4_BORON_OXIDE  # scripted group (container) (typed FeaturePython)
  Dunit = g/cm3
  Dvalue = 1.812
  Group = -> [B_element002,O_element016]
  conduct = 2
  density = 1
  expand = 3
  formula = G4_BORON_OXIDE
  name = G4_BORON_OXIDE
  specific = 4
FEATURE [App::DocumentObjectGroupPython] H_element017  label="H_element : 0.107"  # scripted group (container) (typed FeaturePython)
  n = 0.107
FEATURE [App::DocumentObjectGroupPython] C_element018  label="C_element : 0.145"  # scripted group (container) (typed FeaturePython)
  n = 0.145
FEATURE [App::DocumentObjectGroupPython] N_element012  label="N_element : 0.022"  # scripted group (container) (typed FeaturePython)
  n = 0.022
FEATURE [App::DocumentObjectGroupPython] O_element017  label="O_element : 0.712"  # scripted group (container) (typed FeaturePython)
  n = 0.712
FEATURE [App::DocumentObjectGroupPython] Na_element004  label="Na_element : 0.004"  # scripted group (container) (typed FeaturePython)
  n = 0.002
FEATURE [App::DocumentObjectGroupPython] P_element004  label="P_element : 0.004"  # scripted group (container) (typed FeaturePython)
  n = 0.004
FEATURE [App::DocumentObjectGroupPython] S_element006  label="S_element : 0.005"  # scripted group (container) (typed FeaturePython)
  n = 0.002
FEATURE [App::DocumentObjectGroupPython] Cl_element003  label="Cl_element : 0.004"  # scripted group (container) (typed FeaturePython)
  n = 0.003
FEATURE [App::DocumentObjectGroupPython] K_element002  label="K_element : 0.003"  # scripted group (container) (typed FeaturePython)
  n = 0.003
FEATURE [App::DocumentObjectGroupPython] G4_BRAIN_ICRP  # scripted group (container) (typed FeaturePython)
  Dunit = g/cm3
  Dvalue = 1.04
  Group = -> [H_element017,C_element018,N_element012,O_element017,Na_element004,P_element004,S_element006,Cl_element003,K_element002]
  conduct = 2
  density = 1
  expand = 3
  formula = G4_BRAIN_ICRP
  name = G4_BRAIN_ICRP
  specific = 4
FEATURE [App::DocumentObjectGroupPython] C_element019  label="C_element : 4"  # scripted group (container) (typed FeaturePython)
  n = 4
  ref = C_element
FEATURE [App::DocumentObjectGroupPython] H_element018  label="H_element : 010"  # scripted group (container) (typed FeaturePython)
  n = 10
  ref = H_element
FEATURE [App::DocumentObjectGroupPython] G4_BUTANE  # scripted group (container) (typed FeaturePython)
  Dunit = g/cm3
  Dvalue = 0.00249343
  Group = -> [C_element019,H_element018]
  conduct = 2
  density = 1
  expand = 3
  formula = G4_BUTANE
  name = G4_BUTANE
  specific = 4
FEATURE [App::DocumentObjectGroupPython] C_element020  label="C_element : 008"  # scripted group (container) (typed FeaturePython)
  n = 4
  ref = C_element
FEATURE [App::DocumentObjectGroupPython] H_element019  label="H_element : 011"  # scripted group (container) (typed FeaturePython)
  n = 10
  ref = H_element
FEATURE [App::DocumentObjectGroupPython] O_element018  label="O_element : 007"  # scripted group (container) (typed FeaturePython)
  n = 1
  ref = O_element
FEATURE [App::DocumentObjectGroupPython] G4_N_BUTYL_ALCOHOL  label="G4_N-BUTYL_ALCOHOL"  # scripted group (container) (typed FeaturePython)
  Dunit = g/cm3
  Dvalue = 0.8098
  Group = -> [C_element020,H_element019,O_element018]
  conduct = 2
  density = 1
  expand = 3
  formula = G4_N-BUTYL_ALCOHOL
  name = G4_N-BUTYL_ALCOHOL
  specific = 4
FEATURE [App::DocumentObjectGroupPython] H_element020  label="H_element : 0.025"  # scripted group (container) (typed FeaturePython)
  n = 0.02468
FEATURE [App::DocumentObjectGroupPython] C_element021  label="C_element : 0.502"  # scripted group (container) (typed FeaturePython)
  n = 0.501611
FEATURE [App::DocumentObjectGroupPython] O_element019  label="O_element : 0.005"  # scripted group (container) (typed FeaturePython)
  n = 0.004527
FEATURE [App::DocumentObjectGroupPython] F_element004  label="F_element : 0.465"  # scripted group (container) (typed FeaturePython)
  n = 0.465209
FEATURE [App::DocumentObjectGroupPython] Si_element001  label="Si_element : 0.004"  # scripted group (container) (typed FeaturePython)
  n = 0.003973
FEATURE [App::DocumentObjectGroupPython] G4_C_552  label="G4_C-552"  # scripted group (container) (typed FeaturePython)
  Dunit = g/cm3
  Dvalue = 1.76
  Group = -> [H_element020,C_element021,O_element019,F_element004,Si_element001]
  conduct = 2
  density = 1
  expand = 3
  formula = G4_C-552
  name = G4_C-552
  specific = 4
FEATURE [App::DocumentObjectGroupPython] Cd_element001  label="Cd_element : 1"  # scripted group (container) (typed FeaturePython)
  n = 1
  ref = Cd_element
FEATURE [App::DocumentObjectGroupPython] Te_element001  label="Te_element : 1"  # scripted group (container) (typed FeaturePython)
  n = 1
  ref = Te_element
FEATURE [App::DocumentObjectGroupPython] G4_CADMIUM_TELLURIDE  # scripted group (container) (typed FeaturePython)
  Dunit = g/cm3
  Dvalue = 6.2
  Group = -> [Cd_element001,Te_element001]
  conduct = 2
  density = 1
  expand = 3
  formula = G4_CADMIUM_TELLURIDE
  name = G4_CADMIUM_TELLURIDE
  specific = 4
FEATURE [App::DocumentObjectGroupPython] Cd_element002  label="Cd_element : 002"  # scripted group (container) (typed FeaturePython)
  n = 1
  ref = Cd_element
FEATURE [App::DocumentObjectGroupPython] W_element001  label="W_element : 1"  # scripted group (container) (typed FeaturePython)
  n = 1
  ref = W_element
FEATURE [App::DocumentObjectGroupPython] O_element020  label="O_element : 008"  # scripted group (container) (typed FeaturePython)
  n = 4
  ref = O_element
FEATURE [App::DocumentObjectGroupPython] G4_CADMIUM_TUNGSTATE  # scripted group (container) (typed FeaturePython)
  Dunit = g/cm3
  Dvalue = 7.9
  Group = -> [Cd_element002,W_element001,O_element020]
  conduct = 2
  density = 1
  expand = 3
  formula = G4_CADMIUM_TUNGSTATE
  name = G4_CADMIUM_TUNGSTATE
  specific = 4
FEATURE [App::DocumentObjectGroupPython] Ca_element005  label="Ca_element : 1"  # scripted group (container) (typed FeaturePython)
  n = 1
  ref = Ca_element
FEATURE [App::DocumentObjectGroupPython] C_element022  label="C_element : 009"  # scripted group (container) (typed FeaturePython)
  n = 1
  ref = C_element
FEATURE [App::DocumentObjectGroupPython] O_element021  label="O_element : 009"  # scripted group (container) (typed FeaturePython)
  n = 3
  ref = O_element
FEATURE [App::DocumentObjectGroupPython] G4_CALCIUM_CARBONATE  # scripted group (container) (typed FeaturePython)
  Dunit = g/cm3
  Dvalue = 2.8
  Group = -> [Ca_element005,C_element022,O_element021]
  conduct = 2
  density = 1
  expand = 3
  formula = G4_CALCIUM_CARBONATE
  name = G4_CALCIUM_CARBONATE
  specific = 4
FEATURE [App::DocumentObjectGroupPython] Ca_element006  label="Ca_element : 002"  # scripted group (container) (typed FeaturePython)
  n = 1
  ref = Ca_element
FEATURE [App::DocumentObjectGroupPython] F_element005  label="F_element : 003"  # scripted group (container) (typed FeaturePython)
  n = 2
  ref = F_element
FEATURE [App::DocumentObjectGroupPython] G4_CALCIUM_FLUORIDE  # scripted group (container) (typed FeaturePython)
  Dunit = g/cm3
  Dvalue = 3.18
  Group = -> [Ca_element006,F_element005]
  conduct = 2
  density = 1
  expand = 3
  formula = G4_CALCIUM_FLUORIDE
  name = G4_CALCIUM_FLUORIDE
  specific = 4
FEATURE [App::DocumentObjectGroupPython] Ca_element007  label="Ca_element : 003"  # scripted group (container) (typed FeaturePython)
  n = 1
  ref = Ca_element
FEATURE [App::DocumentObjectGroupPython] O_element022  label="O_element : 010"  # scripted group (container) (typed FeaturePython)
  n = 1
  ref = O_element
FEATURE [App::DocumentObjectGroupPython] G4_CALCIUM_OXIDE  # scripted group (container) (typed FeaturePython)
  Dunit = g/cm3
  Dvalue = 3.3
  Group = -> [Ca_element007,O_element022]
  conduct = 2
  density = 1
  expand = 3
  formula = G4_CALCIUM_OXIDE
  name = G4_CALCIUM_OXIDE
  specific = 4
FEATURE [App::DocumentObjectGroupPython] Ca_element008  label="Ca_element : 004"  # scripted group (container) (typed FeaturePython)
  n = 1
  ref = Ca_element
FEATURE [App::DocumentObjectGroupPython] S_element007  label="S_element : 002"  # scripted group (container) (typed FeaturePython)
  n = 1
  ref = S_element
FEATURE [App::DocumentObjectGroupPython] O_element023  label="O_element : 011"  # scripted group (container) (typed FeaturePython)
  n = 4
  ref = O_element
FEATURE [App::DocumentObjectGroupPython] G4_CALCIUM_SULFATE  # scripted group (container) (typed FeaturePython)
  Dunit = g/cm3
  Dvalue = 2.96
  Group = -> [Ca_element008,S_element007,O_element023]
  conduct = 2
  density = 1
  expand = 3
  formula = G4_CALCIUM_SULFATE
  name = G4_CALCIUM_SULFATE
  specific = 4
FEATURE [App::DocumentObjectGroupPython] Ca_element009  label="Ca_element : 005"  # scripted group (container) (typed FeaturePython)
  n = 1
  ref = Ca_element
FEATURE [App::DocumentObjectGroupPython] W_element002  label="W_element : 002"  # scripted group (container) (typed FeaturePython)
  n = 1
  ref = W_element
FEATURE [App::DocumentObjectGroupPython] O_element024  label="O_element : 012"  # scripted group (container) (typed FeaturePython)
  n = 4
  ref = O_element
FEATURE [App::DocumentObjectGroupPython] G4_CALCIUM_TUNGSTATE  # scripted group (container) (typed FeaturePython)
  Dunit = g/cm3
  Dvalue = 6.062
  Group = -> [Ca_element009,W_element002,O_element024]
  conduct = 2
  density = 1
  expand = 3
  formula = G4_CALCIUM_TUNGSTATE
  name = G4_CALCIUM_TUNGSTATE
  specific = 4
FEATURE [App::DocumentObjectGroupPython] C_element023  label="C_element : 010"  # scripted group (container) (typed FeaturePython)
  n = 1
  ref = C_element
FEATURE [App::DocumentObjectGroupPython] O_element025  label="O_element : 013"  # scripted group (container) (typed FeaturePython)
  n = 2
  ref = O_element
FEATURE [App::DocumentObjectGroupPython] G4_CARBON_DIOXIDE  # scripted group (container) (typed FeaturePython)
  Dunit = g/cm3
  Dvalue = 0.00184212
  Group = -> [C_element023,O_element025]
  conduct = 2
  density = 1
  expand = 3
  formula = G4_CARBON_DIOXIDE
  name = G4_CARBON_DIOXIDE
  specific = 4
FEATURE [App::DocumentObjectGroupPython] C_element024  label="C_element : 011"  # scripted group (container) (typed FeaturePython)
  n = 1
  ref = C_element
FEATURE [App::DocumentObjectGroupPython] Cl_element004  label="Cl_element : 4"  # scripted group (container) (typed FeaturePython)
  n = 4
  ref = Cl_element
FEATURE [App::DocumentObjectGroupPython] G4_CARBON_TETRACHLORIDE  # scripted group (container) (typed FeaturePython)
  Dunit = g/cm3
  Dvalue = 1.594
  Group = -> [C_element024,Cl_element004]
  conduct = 2
  density = 1
  expand = 3
  formula = G4_CARBON_TETRACHLORIDE
  name = G4_CARBON_TETRACHLORIDE
  specific = 4
FEATURE [App::DocumentObjectGroupPython] C_element025  label="C_element : 012"  # scripted group (container) (typed FeaturePython)
  n = 6
  ref = C_element
FEATURE [App::DocumentObjectGroupPython] H_element021  label="H_element : 012"  # scripted group (container) (typed FeaturePython)
  n = 10
  ref = H_element
FEATURE [App::DocumentObjectGroupPython] O_element026  label="O_element : 5"  # scripted group (container) (typed FeaturePython)
  n = 5
  ref = O_element
FEATURE [App::DocumentObjectGroupPython] G4_CELLULOSE_CELLOPHANE  # scripted group (container) (typed FeaturePython)
  Dunit = g/cm3
  Dvalue = 1.42
  Group = -> [C_element025,H_element021,O_element026]
  conduct = 2
  density = 1
  expand = 3
  formula = G4_CELLULOSE_CELLOPHANE
  name = G4_CELLULOSE_CELLOPHANE
  specific = 4
FEATURE [App::DocumentObjectGroupPython] H_element022  label="H_element : 0.067"  # scripted group (container) (typed FeaturePython)
  n = 0.067125
FEATURE [App::DocumentObjectGroupPython] C_element026  label="C_element : 0.545"  # scripted group (container) (typed FeaturePython)
  n = 0.545403
FEATURE [App::DocumentObjectGroupPython] O_element027  label="O_element : 0.387"  # scripted group (container) (typed FeaturePython)
  n = 0.387472
FEATURE [App::DocumentObjectGroupPython] G4_CELLULOSE_BUTYRATE  # scripted group (container) (typed FeaturePython)
  Dunit = g/cm3
  Dvalue = 1.2
  Group = -> [H_element022,C_element026,O_element027]
  conduct = 2
  density = 1
  expand = 3
  formula = G4_CELLULOSE_BUTYRATE
  name = G4_CELLULOSE_BUTYRATE
  specific = 4
FEATURE [App::DocumentObjectGroupPython] H_element023  label="H_element : 0.029"  # scripted group (container) (typed FeaturePython)
  n = 0.029216
FEATURE [App::DocumentObjectGroupPython] C_element027  label="C_element : 0.271"  # scripted group (container) (typed FeaturePython)
  n = 0.271296
FEATURE [App::DocumentObjectGroupPython] N_element013  label="N_element : 0.121"  # scripted group (container) (typed FeaturePython)
  n = 0.121276
FEATURE [App::DocumentObjectGroupPython] O_element028  label="O_element : 0.578"  # scripted group (container) (typed FeaturePython)
  n = 0.578212
FEATURE [App::DocumentObjectGroupPython] G4_CELLULOSE_NITRATE  # scripted group (container) (typed FeaturePython)
  Dunit = g/cm3
  Dvalue = 1.49
  Group = -> [H_element023,C_element027,N_element013,O_element028]
  conduct = 2
  density = 1
  expand = 3
  formula = G4_CELLULOSE_NITRATE
  name = G4_CELLULOSE_NITRATE
  specific = 4
FEATURE [App::DocumentObjectGroupPython] H_element024  label="H_element : 0.108"  # scripted group (container) (typed FeaturePython)
  n = 0.107596
FEATURE [App::DocumentObjectGroupPython] N_element014  label="N_element : 0.001"  # scripted group (container) (typed FeaturePython)
  n = 0.0008
FEATURE [App::DocumentObjectGroupPython] O_element029  label="O_element : 0.875"  # scripted group (container) (typed FeaturePython)
  n = 0.874976
FEATURE [App::DocumentObjectGroupPython] S_element008  label="S_element : 0.015"  # scripted group (container) (typed FeaturePython)
  n = 0.014627
FEATURE [App::DocumentObjectGroupPython] Ce_element001  label="Ce_element : 0.002"  # scripted group (container) (typed FeaturePython)
  n = 0.002001
FEATURE [App::DocumentObjectGroupPython] G4_CERIC_SULFATE  # scripted group (container) (typed FeaturePython)
  Dunit = g/cm3
  Dvalue = 1.03
  Group = -> [H_element024,N_element014,O_element029,S_element008,Ce_element001]
  conduct = 2
  density = 1
  expand = 3
  formula = G4_CERIC_SULFATE
  name = G4_CERIC_SULFATE
  specific = 4
FEATURE [App::DocumentObjectGroupPython] Cs_element001  label="Cs_element : 1"  # scripted group (container) (typed FeaturePython)
  n = 1
  ref = Cs_element
FEATURE [App::DocumentObjectGroupPython] F_element006  label="F_element : 1"  # scripted group (container) (typed FeaturePython)
  n = 1
  ref = F_element
FEATURE [App::DocumentObjectGroupPython] G4_CESIUM_FLUORIDE  # scripted group (container) (typed FeaturePython)
  Dunit = g/cm3
  Dvalue = 4.115
  Group = -> [Cs_element001,F_element006]
  conduct = 2
  density = 1
  expand = 3
  formula = G4_CESIUM_FLUORIDE
  name = G4_CESIUM_FLUORIDE
  specific = 4
FEATURE [App::DocumentObjectGroupPython] Cs_element002  label="Cs_element : 002"  # scripted group (container) (typed FeaturePython)
  n = 1
  ref = Cs_element
FEATURE [App::DocumentObjectGroupPython] I_element001  label="I_element : 1"  # scripted group (container) (typed FeaturePython)
  n = 1
  ref = I_element
FEATURE [App::DocumentObjectGroupPython] G4_CESIUM_IODIDE  # scripted group (container) (typed FeaturePython)
  Dunit = g/cm3
  Dvalue = 4.51
  Group = -> [Cs_element002,I_element001]
  conduct = 2
  density = 1
  expand = 3
  formula = G4_CESIUM_IODIDE
  name = G4_CESIUM_IODIDE
  specific = 4
FEATURE [App::DocumentObjectGroupPython] C_element028  label="C_element : 013"  # scripted group (container) (typed FeaturePython)
  n = 6
  ref = C_element
FEATURE [App::DocumentObjectGroupPython] H_element025  label="H_element : 013"  # scripted group (container) (typed FeaturePython)
  n = 5
  ref = H_element
FEATURE [App::DocumentObjectGroupPython] Cl_element005  label="Cl_element : 1"  # scripted group (container) (typed FeaturePython)
  n = 1
  ref = Cl_element
FEATURE [App::DocumentObjectGroupPython] G4_CHLOROBENZENE  # scripted group (container) (typed FeaturePython)
  Dunit = g/cm3
  Dvalue = 1.1058
  Group = -> [C_element028,H_element025,Cl_element005]
  conduct = 2
  density = 1
  expand = 3
  formula = G4_CHLOROBENZENE
  name = G4_CHLOROBENZENE
  specific = 4
FEATURE [App::DocumentObjectGroupPython] C_element029  label="C_element : 014"  # scripted group (container) (typed FeaturePython)
  n = 1
  ref = C_element
FEATURE [App::DocumentObjectGroupPython] H_element026  label="H_element : 1"  # scripted group (container) (typed FeaturePython)
  n = 1
  ref = H_element
FEATURE [App::DocumentObjectGroupPython] Cl_element006  label="Cl_element : 3"  # scripted group (container) (typed FeaturePython)
  n = 3
  ref = Cl_element
FEATURE [App::DocumentObjectGroupPython] G4_CHLOROFORM  # scripted group (container) (typed FeaturePython)
  Dunit = g/cm3
  Dvalue = 1.4832
  Group = -> [C_element029,H_element026,Cl_element006]
  conduct = 2
  density = 1
  expand = 3
  formula = G4_CHLOROFORM
  name = G4_CHLOROFORM
  specific = 4
FEATURE [App::DocumentObjectGroupPython] H_element027  label="H_element : 0.010"  # scripted group (container) (typed FeaturePython)
  n = 0.01
FEATURE [App::DocumentObjectGroupPython] C_element030  label="C_element : 0.001"  # scripted group (container) (typed FeaturePython)
  n = 0.001
FEATURE [App::DocumentObjectGroupPython] O_element030  label="O_element : 0.529"  # scripted group (container) (typed FeaturePython)
  n = 0.529107
FEATURE [App::DocumentObjectGroupPython] Na_element005  label="Na_element : 0.016"  # scripted group (container) (typed FeaturePython)
  n = 0.016
FEATURE [App::DocumentObjectGroupPython] Mg_element003  label="Mg_element : 0.004"  # scripted group (container) (typed FeaturePython)
  n = 0.002
FEATURE [App::DocumentObjectGroupPython] Al_element002  label="Al_element : 0.034"  # scripted group (container) (typed FeaturePython)
  n = 0.033872
FEATURE [App::DocumentObjectGroupPython] Si_element002  label="Si_element : 0.337"  # scripted group (container) (typed FeaturePython)
  n = 0.337021
FEATURE [App::DocumentObjectGroupPython] K_element003  label="K_element : 0.013"  # scripted group (container) (typed FeaturePython)
  n = 0.013
FEATURE [App::DocumentObjectGroupPython] Ca_element010  label="Ca_element : 0.044"  # scripted group (container) (typed FeaturePython)
  n = 0.044
FEATURE [App::DocumentObjectGroupPython] Fe_element002  label="Fe_element : 0.014"  # scripted group (container) (typed FeaturePython)
  n = 0.014
FEATURE [App::DocumentObjectGroupPython] G4_CONCRETE  # scripted group (container) (typed FeaturePython)
  Dunit = g/cm3
  Dvalue = 2.3
  Group = -> [H_element027,C_element030,O_element030,Na_element005,Mg_element003,Al_element002,Si_element002,K_element003,Ca_element010,Fe_element002]
  conduct = 2
  density = 1
  expand = 3
  formula = G4_CONCRETE
  name = G4_CONCRETE
  specific = 4
FEATURE [App::DocumentObjectGroupPython] C_element031  label="C_element : 015"  # scripted group (container) (typed FeaturePython)
  n = 6
  ref = C_element
FEATURE [App::DocumentObjectGroupPython] H_element028  label="H_element : 12"  # scripted group (container) (typed FeaturePython)
  n = 12
  ref = H_element
FEATURE [App::DocumentObjectGroupPython] G4_CYCLOHEXANE  # scripted group (container) (typed FeaturePython)
  Dunit = g/cm3
  Dvalue = 0.779
  Group = -> [C_element031,H_element028]
  conduct = 2
  density = 1
  expand = 3
  formula = G4_CYCLOHEXANE
  name = G4_CYCLOHEXANE
  specific = 4
FEATURE [App::DocumentObjectGroupPython] C_element032  label="C_element : 016"  # scripted group (container) (typed FeaturePython)
  n = 6
  ref = C_element
FEATURE [App::DocumentObjectGroupPython] H_element029  label="H_element : 4"  # scripted group (container) (typed FeaturePython)
  n = 4
  ref = H_element
FEATURE [App::DocumentObjectGroupPython] Cl_element007  label="Cl_element : 2"  # scripted group (container) (typed FeaturePython)
  n = 2
  ref = Cl_element
FEATURE [App::DocumentObjectGroupPython] G4_1_2_DICHLOROBENZENE  label="G4_1.2-DICHLOROBENZENE"  # scripted group (container) (typed FeaturePython)
  Dunit = g/cm3
  Dvalue = 1.3048
  Group = -> [C_element032,H_element029,Cl_element007]
  conduct = 2
  density = 1
  expand = 3
  formula = G4_1.2-DICHLOROBENZENE
  name = G4_1.2-DICHLOROBENZENE
  specific = 4
FEATURE [App::DocumentObjectGroupPython] C_element033  label="C_element : 017"  # scripted group (container) (typed FeaturePython)
  n = 4
  ref = C_element
FEATURE [App::DocumentObjectGroupPython] H_element030  label="H_element : 8"  # scripted group (container) (typed FeaturePython)
  n = 8
  ref = H_element
FEATURE [App::DocumentObjectGroupPython] O_element031  label="O_element : 014"  # scripted group (container) (typed FeaturePython)
  n = 1
  ref = O_element
FEATURE [App::DocumentObjectGroupPython] Cl_element008  label="Cl_element : 005"  # scripted group (container) (typed FeaturePython)
  n = 2
  ref = Cl_element
FEATURE [App::DocumentObjectGroupPython] G4_DICHLORODIETHYL_ETHER  # scripted group (container) (typed FeaturePython)
  Dunit = g/cm3
  Dvalue = 1.2199
  Group = -> [C_element033,H_element030,O_element031,Cl_element008]
  conduct = 2
  density = 1
  expand = 3
  formula = G4_DICHLORODIETHYL_ETHER
  name = G4_DICHLORODIETHYL_ETHER
  specific = 4
FEATURE [App::DocumentObjectGroupPython] C_element034  label="C_element : 018"  # scripted group (container) (typed FeaturePython)
  n = 2
  ref = C_element
FEATURE [App::DocumentObjectGroupPython] H_element031  label="H_element : 014"  # scripted group (container) (typed FeaturePython)
  n = 4
  ref = H_element
FEATURE [App::DocumentObjectGroupPython] Cl_element009  label="Cl_element : 006"  # scripted group (container) (typed FeaturePython)
  n = 2
  ref = Cl_element
FEATURE [App::DocumentObjectGroupPython] G4_1_2_DICHLOROETHANE  label="G4_1.2-DICHLOROETHANE"  # scripted group (container) (typed FeaturePython)
  Dunit = g/cm3
  Dvalue = 1.2351
  Group = -> [C_element034,H_element031,Cl_element009]
  conduct = 2
  density = 1
  expand = 3
  formula = G4_1.2-DICHLOROETHANE
  name = G4_1.2-DICHLOROETHANE
  specific = 4
FEATURE [App::DocumentObjectGroupPython] C_element035  label="C_element : 019"  # scripted group (container) (typed FeaturePython)
  n = 4
  ref = C_element
FEATURE [App::DocumentObjectGroupPython] H_element032  label="H_element : 015"  # scripted group (container) (typed FeaturePython)
  n = 10
  ref = H_element
FEATURE [App::DocumentObjectGroupPython] O_element032  label="O_element : 015"  # scripted group (container) (typed FeaturePython)
  n = 1
  ref = O_element
FEATURE [App::DocumentObjectGroupPython] G4_DIETHYL_ETHER  # scripted group (container) (typed FeaturePython)
  Dunit = g/cm3
  Dvalue = 0.71378
  Group = -> [C_element035,H_element032,O_element032]
  conduct = 2
  density = 1
  expand = 3
  formula = G4_DIETHYL_ETHER
  name = G4_DIETHYL_ETHER
  specific = 4
FEATURE [App::DocumentObjectGroupPython] C_element036  label="C_element : 020"  # scripted group (container) (typed FeaturePython)
  n = 3
  ref = C_element
FEATURE [App::DocumentObjectGroupPython] H_element033  label="H_element : 016"  # scripted group (container) (typed FeaturePython)
  n = 7
  ref = H_element
FEATURE [App::DocumentObjectGroupPython] N_element015  label="N_element : 008"  # scripted group (container) (typed FeaturePython)
  n = 1
  ref = N_element
FEATURE [App::DocumentObjectGroupPython] O_element033  label="O_element : 016"  # scripted group (container) (typed FeaturePython)
  n = 1
  ref = O_element
FEATURE [App::DocumentObjectGroupPython] G4_N_N_DIMETHYL_FORMAMIDE  label="G4_N.N-DIMETHYL_FORMAMIDE"  # scripted group (container) (typed FeaturePython)
  Dunit = g/cm3
  Dvalue = 0.9487
  Group = -> [C_element036,H_element033,N_element015,O_element033]
  conduct = 2
  density = 1
  expand = 3
  formula = G4_N.N-DIMETHYL_FORMAMIDE
  name = G4_N.N-DIMETHYL_FORMAMIDE
  specific = 4
FEATURE [App::DocumentObjectGroupPython] C_element037  label="C_element : 021"  # scripted group (container) (typed FeaturePython)
  n = 2
  ref = C_element
FEATURE [App::DocumentObjectGroupPython] H_element034  label="H_element : 017"  # scripted group (container) (typed FeaturePython)
  n = 6
  ref = H_element
FEATURE [App::DocumentObjectGroupPython] O_element034  label="O_element : 017"  # scripted group (container) (typed FeaturePython)
  n = 1
  ref = O_element
FEATURE [App::DocumentObjectGroupPython] S_element009  label="S_element : 003"  # scripted group (container) (typed FeaturePython)
  n = 1
  ref = S_element
FEATURE [App::DocumentObjectGroupPython] G4_DIMETHYL_SULFOXIDE  # scripted group (container) (typed FeaturePython)
  Dunit = g/cm3
  Dvalue = 1.1014
  Group = -> [C_element037,H_element034,O_element034,S_element009]
  conduct = 2
  density = 1
  expand = 3
  formula = G4_DIMETHYL_SULFOXIDE
  name = G4_DIMETHYL_SULFOXIDE
  specific = 4
FEATURE [App::DocumentObjectGroupPython] C_element038  label="C_element : 022"  # scripted group (container) (typed FeaturePython)
  n = 2
  ref = C_element
FEATURE [App::DocumentObjectGroupPython] H_element035  label="H_element : 018"  # scripted group (container) (typed FeaturePython)
  n = 6
  ref = H_element
FEATURE [App::DocumentObjectGroupPython] G4_ETHANE  # scripted group (container) (typed FeaturePython)
  Dunit = g/cm3
  Dvalue = 0.00125324
  Group = -> [C_element038,H_element035]
  conduct = 2
  density = 1
  expand = 3
  formula = G4_ETHANE
  name = G4_ETHANE
  specific = 4
FEATURE [App::DocumentObjectGroupPython] C_element039  label="C_element : 023"  # scripted group (container) (typed FeaturePython)
  n = 2
  ref = C_element
FEATURE [App::DocumentObjectGroupPython] H_element036  label="H_element : 019"  # scripted group (container) (typed FeaturePython)
  n = 6
  ref = H_element
FEATURE [App::DocumentObjectGroupPython] O_element035  label="O_element : 018"  # scripted group (container) (typed FeaturePython)
  n = 1
  ref = O_element
FEATURE [App::DocumentObjectGroupPython] G4_ETHYL_ALCOHOL  # scripted group (container) (typed FeaturePython)
  Dunit = g/cm3
  Dvalue = 0.7893
  Group = -> [C_element039,H_element036,O_element035]
  conduct = 2
  density = 1
  expand = 3
  formula = G4_ETHYL_ALCOHOL
  name = G4_ETHYL_ALCOHOL
  specific = 4
FEATURE [App::DocumentObjectGroupPython] H_element037  label="H_element : 0.090"  # scripted group (container) (typed FeaturePython)
  n = 0.090027
FEATURE [App::DocumentObjectGroupPython] C_element040  label="C_element : 0.585"  # scripted group (container) (typed FeaturePython)
  n = 0.585182
FEATURE [App::DocumentObjectGroupPython] O_element036  label="O_element : 0.325"  # scripted group (container) (typed FeaturePython)
  n = 0.324791
FEATURE [App::DocumentObjectGroupPython] G4_ETHYL_CELLULOSE  # scripted group (container) (typed FeaturePython)
  Dunit = g/cm3
  Dvalue = 1.13
  Group = -> [H_element037,C_element040,O_element036]
  conduct = 2
  density = 1
  expand = 3
  formula = G4_ETHYL_CELLULOSE
  name = G4_ETHYL_CELLULOSE
  specific = 4
FEATURE [App::DocumentObjectGroupPython] C_element041  label="C_element : 024"  # scripted group (container) (typed FeaturePython)
  n = 2
  ref = C_element
FEATURE [App::DocumentObjectGroupPython] H_element038  label="H_element : 020"  # scripted group (container) (typed FeaturePython)
  n = 4
  ref = H_element
FEATURE [App::DocumentObjectGroupPython] G4_ETHYLENE  # scripted group (container) (typed FeaturePython)
  Dunit = g/cm3
  Dvalue = 0.00117497
  Group = -> [C_element041,H_element038]
  conduct = 2
  density = 1
  expand = 3
  formula = G4_ETHYLENE
  name = G4_ETHYLENE
  specific = 4
FEATURE [App::DocumentObjectGroupPython] H_element039  label="H_element : 0.096"  # scripted group (container) (typed FeaturePython)
  n = 0.096
FEATURE [App::DocumentObjectGroupPython] C_element042  label="C_element : 0.195"  # scripted group (container) (typed FeaturePython)
  n = 0.195
FEATURE [App::DocumentObjectGroupPython] N_element016  label="N_element : 0.057"  # scripted group (container) (typed FeaturePython)
  n = 0.057
FEATURE [App::DocumentObjectGroupPython] O_element037  label="O_element : 0.646"  # scripted group (container) (typed FeaturePython)
  n = 0.646
FEATURE [App::DocumentObjectGroupPython] Na_element006  label="Na_element : 0.017"  # scripted group (container) (typed FeaturePython)
  n = 0.001
FEATURE [App::DocumentObjectGroupPython] P_element005  label="P_element : 0.104"  # scripted group (container) (typed FeaturePython)
  n = 0.001
FEATURE [App::DocumentObjectGroupPython] S_element010  label="S_element : 0.016"  # scripted group (container) (typed FeaturePython)
  n = 0.003
FEATURE [App::DocumentObjectGroupPython] Cl_element010  label="Cl_element : 0.005"  # scripted group (container) (typed FeaturePython)
  n = 0.001
FEATURE [App::DocumentObjectGroupPython] G4_EYE_LENS_ICRP  # scripted group (container) (typed FeaturePython)
  Dunit = g/cm3
  Dvalue = 1.07
  Group = -> [H_element039,C_element042,N_element016,O_element037,Na_element006,P_element005,S_element010,Cl_element010]
  conduct = 2
  density = 1
  expand = 3
  formula = G4_EYE_LENS_ICRP
  name = G4_EYE_LENS_ICRP
  specific = 4
FEATURE [App::DocumentObjectGroupPython] Fe_element003  label="Fe_element : 2"  # scripted group (container) (typed FeaturePython)
  n = 2
  ref = Fe_element
FEATURE [App::DocumentObjectGroupPython] O_element038  label="O_element : 019"  # scripted group (container) (typed FeaturePython)
  n = 3
  ref = O_element
FEATURE [App::DocumentObjectGroupPython] G4_FERRIC_OXIDE  # scripted group (container) (typed FeaturePython)
  Dunit = g/cm3
  Dvalue = 5.2
  Group = -> [Fe_element003,O_element038]
  conduct = 2
  density = 1
  expand = 3
  formula = G4_FERRIC_OXIDE
  name = G4_FERRIC_OXIDE
  specific = 4
FEATURE [App::DocumentObjectGroupPython] Fe_element004  label="Fe_element : 1"  # scripted group (container) (typed FeaturePython)
  n = 1
  ref = Fe_element
FEATURE [App::DocumentObjectGroupPython] B_element003  label="B_element : 1"  # scripted group (container) (typed FeaturePython)
  n = 1
  ref = B_element
FEATURE [App::DocumentObjectGroupPython] G4_FERROBORIDE  # scripted group (container) (typed FeaturePython)
  Dunit = g/cm3
  Dvalue = 7.15
  Group = -> [Fe_element004,B_element003]
  conduct = 2
  density = 1
  expand = 3
  formula = G4_FERROBORIDE
  name = G4_FERROBORIDE
  specific = 4
FEATURE [App::DocumentObjectGroupPython] Fe_element005  label="Fe_element : 003"  # scripted group (container) (typed FeaturePython)
  n = 1
  ref = Fe_element
FEATURE [App::DocumentObjectGroupPython] O_element039  label="O_element : 020"  # scripted group (container) (typed FeaturePython)
  n = 1
  ref = O_element
FEATURE [App::DocumentObjectGroupPython] G4_FERROUS_OXIDE  # scripted group (container) (typed FeaturePython)
  Dunit = g/cm3
  Dvalue = 5.7
  Group = -> [Fe_element005,O_element039]
  conduct = 2
  density = 1
  expand = 3
  formula = G4_FERROUS_OXIDE
  name = G4_FERROUS_OXIDE
  specific = 4
FEATURE [App::DocumentObjectGroupPython] H_element040  label="H_element : 0.115"  # scripted group (container) (typed FeaturePython)
  n = 0.108259
FEATURE [App::DocumentObjectGroupPython] N_element017  label="N_element : 0.000"  # scripted group (container) (typed FeaturePython)
  n = 2.7e-05
FEATURE [App::DocumentObjectGroupPython] O_element040  label="O_element : 0.879"  # scripted group (container) (typed FeaturePython)
  n = 0.878636
FEATURE [App::DocumentObjectGroupPython] Na_element007  label="Na_element : 0.000"  # scripted group (container) (typed FeaturePython)
  n = 2.2e-05
FEATURE [App::DocumentObjectGroupPython] S_element011  label="S_element : 0.013"  # scripted group (container) (typed FeaturePython)
  n = 0.012968
FEATURE [App::DocumentObjectGroupPython] Cl_element011  label="Cl_element : 0.000"  # scripted group (container) (typed FeaturePython)
  n = 3.4e-05
FEATURE [App::DocumentObjectGroupPython] Fe_element006  label="Fe_element : 0.000"  # scripted group (container) (typed FeaturePython)
  n = 5.4e-05
FEATURE [App::DocumentObjectGroupPython] G4_FERROUS_SULFATE  # scripted group (container) (typed FeaturePython)
  Dunit = g/cm3
  Dvalue = 1.024
  Group = -> [H_element040,N_element017,O_element040,Na_element007,S_element011,Cl_element011,Fe_element006]
  conduct = 2
  density = 1
  expand = 3
  formula = G4_FERROUS_SULFATE
  name = G4_FERROUS_SULFATE
  specific = 4
FEATURE [App::DocumentObjectGroupPython] C_element043  label="C_element : 0.099"  # scripted group (container) (typed FeaturePython)
  n = 0.099335
FEATURE [App::DocumentObjectGroupPython] F_element007  label="F_element : 0.314"  # scripted group (container) (typed FeaturePython)
  n = 0.314247
FEATURE [App::DocumentObjectGroupPython] Cl_element012  label="Cl_element : 0.586"  # scripted group (container) (typed FeaturePython)
  n = 0.586418
FEATURE [App::DocumentObjectGroupPython] G4_FREON_12  label="G4_FREON-12"  # scripted group (container) (typed FeaturePython)
  Dunit = g/cm3
  Dvalue = 1.12
  Group = -> [C_element043,F_element007,Cl_element012]
  conduct = 2
  density = 1
  expand = 3
  formula = G4_FREON-12
  name = G4_FREON-12
  specific = 4
FEATURE [App::DocumentObjectGroupPython] C_element044  label="C_element : 0.057"  # scripted group (container) (typed FeaturePython)
  n = 0.057245
FEATURE [App::DocumentObjectGroupPython] F_element008  label="F_element : 0.181"  # scripted group (container) (typed FeaturePython)
  n = 0.181096
FEATURE [App::DocumentObjectGroupPython] Br_element001  label="Br_element : 0.762"  # scripted group (container) (typed FeaturePython)
  n = 0.761659
FEATURE [App::DocumentObjectGroupPython] G4_FREON_12B2  label="G4_FREON-12B2"  # scripted group (container) (typed FeaturePython)
  Dunit = g/cm3
  Dvalue = 1.8
  Group = -> [C_element044,F_element008,Br_element001]
  conduct = 2
  density = 1
  expand = 3
  formula = G4_FREON-12B2
  name = G4_FREON-12B2
  specific = 4
FEATURE [App::DocumentObjectGroupPython] C_element045  label="C_element : 0.115"  # scripted group (container) (typed FeaturePython)
  n = 0.114983
FEATURE [App::DocumentObjectGroupPython] F_element009  label="F_element : 0.546"  # scripted group (container) (typed FeaturePython)
  n = 0.545621
FEATURE [App::DocumentObjectGroupPython] Cl_element013  label="Cl_element : 0.339"  # scripted group (container) (typed FeaturePython)
  n = 0.339396
FEATURE [App::DocumentObjectGroupPython] G4_FREON_13  label="G4_FREON-13"  # scripted group (container) (typed FeaturePython)
  Dunit = g/cm3
  Dvalue = 0.95
  Group = -> [C_element045,F_element009,Cl_element013]
  conduct = 2
  density = 1
  expand = 3
  formula = G4_FREON-13
  name = G4_FREON-13
  specific = 4
FEATURE [App::DocumentObjectGroupPython] C_element046  label="C_element : 025"  # scripted group (container) (typed FeaturePython)
  n = 1
  ref = C_element
FEATURE [App::DocumentObjectGroupPython] F_element010  label="F_element : 3"  # scripted group (container) (typed FeaturePython)
  n = 3
  ref = F_element
FEATURE [App::DocumentObjectGroupPython] Br_element002  label="Br_element : 1"  # scripted group (container) (typed FeaturePython)
  n = 1
  ref = Br_element
FEATURE [App::DocumentObjectGroupPython] G4_FREON_13B1  label="G4_FREON-13B1"  # scripted group (container) (typed FeaturePython)
  Dunit = g/cm3
  Dvalue = 1.5
  Group = -> [C_element046,F_element010,Br_element002]
  conduct = 2
  density = 1
  expand = 3
  formula = G4_FREON-13B1
  name = G4_FREON-13B1
  specific = 4
FEATURE [App::DocumentObjectGroupPython] C_element047  label="C_element : 0.061"  # scripted group (container) (typed FeaturePython)
  n = 0.061309
FEATURE [App::DocumentObjectGroupPython] F_element011  label="F_element : 0.291"  # scripted group (container) (typed FeaturePython)
  n = 0.290924
FEATURE [App::DocumentObjectGroupPython] I_element002  label="I_element : 0.648"  # scripted group (container) (typed FeaturePython)
  n = 0.647767
FEATURE [App::DocumentObjectGroupPython] G4_FREON_13I1  label="G4_FREON-13I1"  # scripted group (container) (typed FeaturePython)
  Dunit = g/cm3
  Dvalue = 1.8
  Group = -> [C_element047,F_element011,I_element002]
  conduct = 2
  density = 1
  expand = 3
  formula = G4_FREON-13I1
  name = G4_FREON-13I1
  specific = 4
FEATURE [App::DocumentObjectGroupPython] Gd_element001  label="Gd_element : 2"  # scripted group (container) (typed FeaturePython)
  n = 2
  ref = Gd_element
FEATURE [App::DocumentObjectGroupPython] O_element041  label="O_element : 021"  # scripted group (container) (typed FeaturePython)
  n = 2
  ref = O_element
FEATURE [App::DocumentObjectGroupPython] S_element012  label="S_element : 004"  # scripted group (container) (typed FeaturePython)
  n = 1
  ref = S_element
FEATURE [App::DocumentObjectGroupPython] G4_GADOLINIUM_OXYSULFIDE  # scripted group (container) (typed FeaturePython)
  Dunit = g/cm3
  Dvalue = 7.44
  Group = -> [Gd_element001,O_element041,S_element012]
  conduct = 2
  density = 1
  expand = 3
  formula = G4_GADOLINIUM_OXYSULFIDE
  name = G4_GADOLINIUM_OXYSULFIDE
  specific = 4
FEATURE [App::DocumentObjectGroupPython] Ga_element001  label="Ga_element : 1"  # scripted group (container) (typed FeaturePython)
  n = 1
  ref = Ga_element
FEATURE [App::DocumentObjectGroupPython] As_element001  label="As_element : 1"  # scripted group (container) (typed FeaturePython)
  n = 1
  ref = As_element
FEATURE [App::DocumentObjectGroupPython] G4_GALLIUM_ARSENIDE  # scripted group (container) (typed FeaturePython)
  Dunit = g/cm3
  Dvalue = 5.31
  Group = -> [Ga_element001,As_element001]
  conduct = 2
  density = 1
  expand = 3
  formula = G4_GALLIUM_ARSENIDE
  name = G4_GALLIUM_ARSENIDE
  specific = 4
FEATURE [App::DocumentObjectGroupPython] H_element041  label="H_element : 0.081"  # scripted group (container) (typed FeaturePython)
  n = 0.08118
FEATURE [App::DocumentObjectGroupPython] C_element048  label="C_element : 0.416"  # scripted group (container) (typed FeaturePython)
  n = 0.41606
FEATURE [App::DocumentObjectGroupPython] N_element018  label="N_element : 0.111"  # scripted group (container) (typed FeaturePython)
  n = 0.11124
FEATURE [App::DocumentObjectGroupPython] O_element042  label="O_element : 0.381"  # scripted group (container) (typed FeaturePython)
  n = 0.38064
FEATURE [App::DocumentObjectGroupPython] S_element013  label="S_element : 0.011"  # scripted group (container) (typed FeaturePython)
  n = 0.01088
FEATURE [App::DocumentObjectGroupPython] G4_GEL_PHOTO_EMULSION  # scripted group (container) (typed FeaturePython)
  Dunit = g/cm3
  Dvalue = 1.2914
  Group = -> [H_element041,C_element048,N_element018,O_element042,S_element013]
  conduct = 2
  density = 1
  expand = 3
  formula = G4_GEL_PHOTO_EMULSION
  name = G4_GEL_PHOTO_EMULSION
  specific = 4
FEATURE [App::DocumentObjectGroupPython] B_element004  label="B_element : 0.040"  # scripted group (container) (typed FeaturePython)
  n = 0.0400639
FEATURE [App::DocumentObjectGroupPython] O_element043  label="O_element : 0.540"  # scripted group (container) (typed FeaturePython)
  n = 0.539561
FEATURE [App::DocumentObjectGroupPython] Na_element008  label="Na_element : 0.028"  # scripted group (container) (typed FeaturePython)
  n = 0.0281909
FEATURE [App::DocumentObjectGroupPython] Al_element003  label="Al_element : 0.012"  # scripted group (container) (typed FeaturePython)
  n = 0.011644
FEATURE [App::DocumentObjectGroupPython] Si_element003  label="Si_element : 0.377"  # scripted group (container) (typed FeaturePython)
  n = 0.377219
FEATURE [App::DocumentObjectGroupPython] K_element004  label="K_element : 0.014"  # scripted group (container) (typed FeaturePython)
  n = 0.00332099
FEATURE [App::DocumentObjectGroupPython] G4_Pyrex_Glass  # scripted group (container) (typed FeaturePython)
  Dunit = g/cm3
  Dvalue = 2.23
  Group = -> [B_element004,O_element043,Na_element008,Al_element003,Si_element003,K_element004]
  conduct = 2
  density = 1
  expand = 3
  formula = G4_Pyrex_Glass
  name = G4_Pyrex_Glass
  specific = 4
FEATURE [App::DocumentObjectGroupPython] O_element044  label="O_element : 0.156"  # scripted group (container) (typed FeaturePython)
  n = 0.156453
FEATURE [App::DocumentObjectGroupPython] Si_element004  label="Si_element : 0.081"  # scripted group (container) (typed FeaturePython)
  n = 0.080866
FEATURE [App::DocumentObjectGroupPython] Ti_element001  label="Ti_element : 0.008"  # scripted group (container) (typed FeaturePython)
  n = 0.008092
FEATURE [App::DocumentObjectGroupPython] As_element002  label="As_element : 0.003"  # scripted group (container) (typed FeaturePython)
  n = 0.002651
FEATURE [App::DocumentObjectGroupPython] Pb_element001  label="Pb_element : 0.752"  # scripted group (container) (typed FeaturePython)
  n = 0.751938
FEATURE [App::DocumentObjectGroupPython] G4_GLASS_LEAD  # scripted group (container) (typed FeaturePython)
  Dunit = g/cm3
  Dvalue = 6.22
  Group = -> [O_element044,Si_element004,Ti_element001,As_element002,Pb_element001]
  conduct = 2
  density = 1
  expand = 3
  formula = G4_GLASS_LEAD
  name = G4_GLASS_LEAD
  specific = 4
FEATURE [App::DocumentObjectGroupPython] O_element045  label="O_element : 0.460"  # scripted group (container) (typed FeaturePython)
  n = 0.4598
FEATURE [App::DocumentObjectGroupPython] Na_element009  label="Na_element : 0.096"  # scripted group (container) (typed FeaturePython)
  n = 0.0964411
FEATURE [App::DocumentObjectGroupPython] Si_element005  label="Si_element : 0.378"  # scripted group (container) (typed FeaturePython)
  n = 0.336553
FEATURE [App::DocumentObjectGroupPython] Ca_element011  label="Ca_element : 0.107"  # scripted group (container) (typed FeaturePython)
  n = 0.107205
FEATURE [App::DocumentObjectGroupPython] G4_GLASS_PLATE  # scripted group (container) (typed FeaturePython)
  Dunit = g/cm3
  Dvalue = 2.4
  Group = -> [O_element045,Na_element009,Si_element005,Ca_element011]
  conduct = 2
  density = 1
  expand = 3
  formula = G4_GLASS_PLATE
  name = G4_GLASS_PLATE
  specific = 4
FEATURE [App::DocumentObjectGroupPython] C_element049  label="C_element : 026"  # scripted group (container) (typed FeaturePython)
  n = 5
  ref = C_element
FEATURE [App::DocumentObjectGroupPython] H_element042  label="H_element : 021"  # scripted group (container) (typed FeaturePython)
  n = 10
  ref = H_element
FEATURE [App::DocumentObjectGroupPython] N_element019  label="N_element : 2"  # scripted group (container) (typed FeaturePython)
  n = 2
  ref = N_element
FEATURE [App::DocumentObjectGroupPython] O_element046  label="O_element : 022"  # scripted group (container) (typed FeaturePython)
  n = 3
  ref = O_element
FEATURE [App::DocumentObjectGroupPython] G4_GLUTAMINE  # scripted group (container) (typed FeaturePython)
  Dunit = g/cm3
  Dvalue = 1.46
  Group = -> [C_element049,H_element042,N_element019,O_element046]
  conduct = 2
  density = 1
  expand = 3
  formula = G4_GLUTAMINE
  name = G4_GLUTAMINE
  specific = 4
FEATURE [App::DocumentObjectGroupPython] C_element050  label="C_element : 027"  # scripted group (container) (typed FeaturePython)
  n = 3
  ref = C_element
FEATURE [App::DocumentObjectGroupPython] H_element043  label="H_element : 022"  # scripted group (container) (typed FeaturePython)
  n = 8
  ref = H_element
FEATURE [App::DocumentObjectGroupPython] O_element047  label="O_element : 023"  # scripted group (container) (typed FeaturePython)
  n = 3
  ref = O_element
FEATURE [App::DocumentObjectGroupPython] G4_GLYCEROL  # scripted group (container) (typed FeaturePython)
  Dunit = g/cm3
  Dvalue = 1.2613
  Group = -> [C_element050,H_element043,O_element047]
  conduct = 2
  density = 1
  expand = 3
  formula = G4_GLYCEROL
  name = G4_GLYCEROL
  specific = 4
FEATURE [App::DocumentObjectGroupPython] C_element051  label="C_element : 028"  # scripted group (container) (typed FeaturePython)
  n = 5
  ref = C_element
FEATURE [App::DocumentObjectGroupPython] H_element044  label="H_element : 023"  # scripted group (container) (typed FeaturePython)
  n = 5
  ref = H_element
FEATURE [App::DocumentObjectGroupPython] N_element020  label="N_element : 009"  # scripted group (container) (typed FeaturePython)
  n = 5
  ref = N_element
FEATURE [App::DocumentObjectGroupPython] O_element048  label="O_element : 024"  # scripted group (container) (typed FeaturePython)
  n = 1
  ref = O_element
FEATURE [App::DocumentObjectGroupPython] G4_GUANINE  # scripted group (container) (typed FeaturePython)
  Dunit = g/cm3
  Dvalue = 2.2
  Group = -> [C_element051,H_element044,N_element020,O_element048]
  conduct = 2
  density = 1
  expand = 3
  formula = G4_GUANINE
  name = G4_GUANINE
  specific = 4
FEATURE [App::DocumentObjectGroupPython] Ca_element012  label="Ca_element : 006"  # scripted group (container) (typed FeaturePython)
  n = 1
  ref = Ca_element
FEATURE [App::DocumentObjectGroupPython] S_element014  label="S_element : 005"  # scripted group (container) (typed FeaturePython)
  n = 1
  ref = S_element
FEATURE [App::DocumentObjectGroupPython] O_element049  label="O_element : 6"  # scripted group (container) (typed FeaturePython)
  n = 6
  ref = O_element
FEATURE [App::DocumentObjectGroupPython] H_element045  label="H_element : 024"  # scripted group (container) (typed FeaturePython)
  n = 4
  ref = H_element
FEATURE [App::DocumentObjectGroupPython] G4_GYPSUM  # scripted group (container) (typed FeaturePython)
  Dunit = g/cm3
  Dvalue = 2.32
  Group = -> [Ca_element012,S_element014,O_element049,H_element045]
  conduct = 2
  density = 1
  expand = 3
  formula = G4_GYPSUM
  name = G4_GYPSUM
  specific = 4
FEATURE [App::DocumentObjectGroupPython] C_element052  label="C_element : 7"  # scripted group (container) (typed FeaturePython)
  n = 7
  ref = C_element
FEATURE [App::DocumentObjectGroupPython] H_element046  label="H_element : 16"  # scripted group (container) (typed FeaturePython)
  n = 16
  ref = H_element
FEATURE [App::DocumentObjectGroupPython] G4_N_HEPTANE  label="G4_N-HEPTANE"  # scripted group (container) (typed FeaturePython)
  Dunit = g/cm3
  Dvalue = 0.68376
  Group = -> [C_element052,H_element046]
  conduct = 2
  density = 1
  expand = 3
  formula = G4_N-HEPTANE
  name = G4_N-HEPTANE
  specific = 4
FEATURE [App::DocumentObjectGroupPython] C_element053  label="C_element : 029"  # scripted group (container) (typed FeaturePython)
  n = 6
  ref = C_element
FEATURE [App::DocumentObjectGroupPython] H_element047  label="H_element : 14"  # scripted group (container) (typed FeaturePython)
  n = 14
  ref = H_element
FEATURE [App::DocumentObjectGroupPython] G4_N_HEXANE  label="G4_N-HEXANE"  # scripted group (container) (typed FeaturePython)
  Dunit = g/cm3
  Dvalue = 0.6603
  Group = -> [C_element053,H_element047]
  conduct = 2
  density = 1
  expand = 3
  formula = G4_N-HEXANE
  name = G4_N-HEXANE
  specific = 4
FEATURE [App::DocumentObjectGroupPython] C_element054  label="C_element : 22"  # scripted group (container) (typed FeaturePython)
  n = 22
  ref = C_element
FEATURE [App::DocumentObjectGroupPython] H_element048  label="H_element : 025"  # scripted group (container) (typed FeaturePython)
  n = 10
  ref = H_element
FEATURE [App::DocumentObjectGroupPython] N_element021  label="N_element : 010"  # scripted group (container) (typed FeaturePython)
  n = 2
  ref = N_element
FEATURE [App::DocumentObjectGroupPython] O_element050  label="O_element : 025"  # scripted group (container) (typed FeaturePython)
  n = 5
  ref = O_element
FEATURE [App::DocumentObjectGroupPython] G4_KAPTON  # scripted group (container) (typed FeaturePython)
  Dunit = g/cm3
  Dvalue = 1.42
  Group = -> [C_element054,H_element048,N_element021,O_element050]
  conduct = 2
  density = 1
  expand = 3
  formula = G4_KAPTON
  name = G4_KAPTON
  specific = 4
FEATURE [App::DocumentObjectGroupPython] La_element001  label="La_element : 1"  # scripted group (container) (typed FeaturePython)
  n = 1
  ref = La_element
FEATURE [App::DocumentObjectGroupPython] Br_element003  label="Br_element : 002"  # scripted group (container) (typed FeaturePython)
  n = 1
  ref = Br_element
FEATURE [App::DocumentObjectGroupPython] O_element051  label="O_element : 026"  # scripted group (container) (typed FeaturePython)
  n = 1
  ref = O_element
FEATURE [App::DocumentObjectGroupPython] G4_LANTHANUM_OXYBROMIDE  # scripted group (container) (typed FeaturePython)
  Dunit = g/cm3
  Dvalue = 6.28
  Group = -> [La_element001,Br_element003,O_element051]
  conduct = 2
  density = 1
  expand = 3
  formula = G4_LANTHANUM_OXYBROMIDE
  name = G4_LANTHANUM_OXYBROMIDE
  specific = 4
FEATURE [App::DocumentObjectGroupPython] La_element002  label="La_element : 2"  # scripted group (container) (typed FeaturePython)
  n = 2
  ref = La_element
FEATURE [App::DocumentObjectGroupPython] O_element052  label="O_element : 027"  # scripted group (container) (typed FeaturePython)
  n = 2
  ref = O_element
FEATURE [App::DocumentObjectGroupPython] S_element015  label="S_element : 006"  # scripted group (container) (typed FeaturePython)
  n = 1
  ref = S_element
FEATURE [App::DocumentObjectGroupPython] G4_LANTHANUM_OXYSULFIDE  # scripted group (container) (typed FeaturePython)
  Dunit = g/cm3
  Dvalue = 5.86
  Group = -> [La_element002,O_element052,S_element015]
  conduct = 2
  density = 1
  expand = 3
  formula = G4_LANTHANUM_OXYSULFIDE
  name = G4_LANTHANUM_OXYSULFIDE
  specific = 4
FEATURE [App::DocumentObjectGroupPython] O_element053  label="O_element : 0.072"  # scripted group (container) (typed FeaturePython)
  n = 0.071682
FEATURE [App::DocumentObjectGroupPython] Pb_element002  label="Pb_element : 0.928"  # scripted group (container) (typed FeaturePython)
  n = 0.928318
FEATURE [App::DocumentObjectGroupPython] G4_LEAD_OXIDE  # scripted group (container) (typed FeaturePython)
  Dunit = g/cm3
  Dvalue = 9.53
  Group = -> [O_element053,Pb_element002]
  conduct = 2
  density = 1
  expand = 3
  formula = G4_LEAD_OXIDE
  name = G4_LEAD_OXIDE
  specific = 4
FEATURE [App::DocumentObjectGroupPython] Li_element001  label="Li_element : 1"  # scripted group (container) (typed FeaturePython)
  n = 1
  ref = Li_element
FEATURE [App::DocumentObjectGroupPython] N_element022  label="N_element : 011"  # scripted group (container) (typed FeaturePython)
  n = 1
  ref = N_element
FEATURE [App::DocumentObjectGroupPython] H_element049  label="H_element : 026"  # scripted group (container) (typed FeaturePython)
  n = 2
  ref = H_element
FEATURE [App::DocumentObjectGroupPython] G4_LITHIUM_AMIDE  # scripted group (container) (typed FeaturePython)
  Dunit = g/cm3
  Dvalue = 1.178
  Group = -> [Li_element001,N_element022,H_element049]
  conduct = 2
  density = 1
  expand = 3
  formula = G4_LITHIUM_AMIDE
  name = G4_LITHIUM_AMIDE
  specific = 4
FEATURE [App::DocumentObjectGroupPython] Li_element002  label="Li_element : 2"  # scripted group (container) (typed FeaturePython)
  n = 2
  ref = Li_element
FEATURE [App::DocumentObjectGroupPython] C_element055  label="C_element : 030"  # scripted group (container) (typed FeaturePython)
  n = 1
  ref = C_element
FEATURE [App::DocumentObjectGroupPython] O_element054  label="O_element : 028"  # scripted group (container) (typed FeaturePython)
  n = 3
  ref = O_element
FEATURE [App::DocumentObjectGroupPython] G4_LITHIUM_CARBONATE  # scripted group (container) (typed FeaturePython)
  Dunit = g/cm3
  Dvalue = 2.11
  Group = -> [Li_element002,C_element055,O_element054]
  conduct = 2
  density = 1
  expand = 3
  formula = G4_LITHIUM_CARBONATE
  name = G4_LITHIUM_CARBONATE
  specific = 4
FEATURE [App::DocumentObjectGroupPython] Li_element003  label="Li_element : 003"  # scripted group (container) (typed FeaturePython)
  n = 1
  ref = Li_element
FEATURE [App::DocumentObjectGroupPython] F_element012  label="F_element : 004"  # scripted group (container) (typed FeaturePython)
  n = 1
  ref = F_element
FEATURE [App::DocumentObjectGroupPython] G4_LITHIUM_FLUORIDE  # scripted group (container) (typed FeaturePython)
  Dunit = g/cm3
  Dvalue = 2.635
  Group = -> [Li_element003,F_element012]
  conduct = 2
  density = 1
  expand = 3
  formula = G4_LITHIUM_FLUORIDE
  name = G4_LITHIUM_FLUORIDE
  specific = 4
FEATURE [App::DocumentObjectGroupPython] Li_element004  label="Li_element : 004"  # scripted group (container) (typed FeaturePython)
  n = 1
  ref = Li_element
FEATURE [App::DocumentObjectGroupPython] H_element050  label="H_element : 027"  # scripted group (container) (typed FeaturePython)
  n = 1
  ref = H_element
FEATURE [App::DocumentObjectGroupPython] G4_LITHIUM_HYDRIDE  # scripted group (container) (typed FeaturePython)
  Dunit = g/cm3
  Dvalue = 0.82
  Group = -> [Li_element004,H_element050]
  conduct = 2
  density = 1
  expand = 3
  formula = G4_LITHIUM_HYDRIDE
  name = G4_LITHIUM_HYDRIDE
  specific = 4
FEATURE [App::DocumentObjectGroupPython] Li_element005  label="Li_element : 005"  # scripted group (container) (typed FeaturePython)
  n = 1
  ref = Li_element
FEATURE [App::DocumentObjectGroupPython] I_element003  label="I_element : 002"  # scripted group (container) (typed FeaturePython)
  n = 1
  ref = I_element
FEATURE [App::DocumentObjectGroupPython] G4_LITHIUM_IODIDE  # scripted group (container) (typed FeaturePython)
  Dunit = g/cm3
  Dvalue = 3.494
  Group = -> [Li_element005,I_element003]
  conduct = 2
  density = 1
  expand = 3
  formula = G4_LITHIUM_IODIDE
  name = G4_LITHIUM_IODIDE
  specific = 4
FEATURE [App::DocumentObjectGroupPython] Li_element006  label="Li_element : 006"  # scripted group (container) (typed FeaturePython)
  n = 2
  ref = Li_element
FEATURE [App::DocumentObjectGroupPython] O_element055  label="O_element : 029"  # scripted group (container) (typed FeaturePython)
  n = 1
  ref = O_element
FEATURE [App::DocumentObjectGroupPython] G4_LITHIUM_OXIDE  # scripted group (container) (typed FeaturePython)
  Dunit = g/cm3
  Dvalue = 2.013
  Group = -> [Li_element006,O_element055]
  conduct = 2
  density = 1
  expand = 3
  formula = G4_LITHIUM_OXIDE
  name = G4_LITHIUM_OXIDE
  specific = 4
FEATURE [App::DocumentObjectGroupPython] Li_element007  label="Li_element : 007"  # scripted group (container) (typed FeaturePython)
  n = 2
  ref = Li_element
FEATURE [App::DocumentObjectGroupPython] B_element005  label="B_element : 005"  # scripted group (container) (typed FeaturePython)
  n = 4
  ref = B_element
FEATURE [App::DocumentObjectGroupPython] O_element056  label="O_element : 7"  # scripted group (container) (typed FeaturePython)
  n = 7
  ref = O_element
FEATURE [App::DocumentObjectGroupPython] G4_LITHIUM_TETRABORATE  # scripted group (container) (typed FeaturePython)
  Dunit = g/cm3
  Dvalue = 2.44
  Group = -> [Li_element007,B_element005,O_element056]
  conduct = 2
  density = 1
  expand = 3
  formula = G4_LITHIUM_TETRABORATE
  name = G4_LITHIUM_TETRABORATE
  specific = 4
FEATURE [App::DocumentObjectGroupPython] H_element051  label="H_element : 0.105"  # scripted group (container) (typed FeaturePython)
  n = 0.105
FEATURE [App::DocumentObjectGroupPython] C_element056  label="C_element : 0.083"  # scripted group (container) (typed FeaturePython)
  n = 0.083
FEATURE [App::DocumentObjectGroupPython] N_element023  label="N_element : 0.023"  # scripted group (container) (typed FeaturePython)
  n = 0.023
FEATURE [App::DocumentObjectGroupPython] O_element057  label="O_element : 0.779"  # scripted group (container) (typed FeaturePython)
  n = 0.779
FEATURE [App::DocumentObjectGroupPython] Na_element010  label="Na_element : 0.097"  # scripted group (container) (typed FeaturePython)
  n = 0.002
FEATURE [App::DocumentObjectGroupPython] P_element006  label="P_element : 0.105"  # scripted group (container) (typed FeaturePython)
  n = 0.001
FEATURE [App::DocumentObjectGroupPython] S_element016  label="S_element : 0.017"  # scripted group (container) (typed FeaturePython)
  n = 0.002
FEATURE [App::DocumentObjectGroupPython] Cl_element014  label="Cl_element : 0.587"  # scripted group (container) (typed FeaturePython)
  n = 0.003
FEATURE [App::DocumentObjectGroupPython] K_element005  label="K_element : 0.015"  # scripted group (container) (typed FeaturePython)
  n = 0.002
FEATURE [App::DocumentObjectGroupPython] G4_LUNG_ICRP  # scripted group (container) (typed FeaturePython)
  Dunit = g/cm3
  Dvalue = 1.04
  Group = -> [H_element051,C_element056,N_element023,O_element057,Na_element010,P_element006,S_element016,Cl_element014,K_element005]
  conduct = 2
  density = 1
  expand = 3
  formula = G4_LUNG_ICRP
  name = G4_LUNG_ICRP
  specific = 4
FEATURE [App::DocumentObjectGroupPython] H_element052  label="H_element : 0.116"  # scripted group (container) (typed FeaturePython)
  n = 0.114318
FEATURE [App::DocumentObjectGroupPython] C_element057  label="C_element : 0.656"  # scripted group (container) (typed FeaturePython)
  n = 0.655824
FEATURE [App::DocumentObjectGroupPython] O_element058  label="O_element : 0.092"  # scripted group (container) (typed FeaturePython)
  n = 0.0921831
FEATURE [App::DocumentObjectGroupPython] Mg_element004  label="Mg_element : 0.135"  # scripted group (container) (typed FeaturePython)
  n = 0.134792
FEATURE [App::DocumentObjectGroupPython] Ca_element013  label="Ca_element : 0.003"  # scripted group (container) (typed FeaturePython)
  n = 0.002883
FEATURE [App::DocumentObjectGroupPython] G4_M3_WAX  # scripted group (container) (typed FeaturePython)
  Dunit = g/cm3
  Dvalue = 1.05
  Group = -> [H_element052,C_element057,O_element058,Mg_element004,Ca_element013]
  conduct = 2
  density = 1
  expand = 3
  formula = G4_M3_WAX
  name = G4_M3_WAX
  specific = 4
FEATURE [App::DocumentObjectGroupPython] Mg_element005  label="Mg_element : 1"  # scripted group (container) (typed FeaturePython)
  n = 1
  ref = Mg_element
FEATURE [App::DocumentObjectGroupPython] C_element058  label="C_element : 031"  # scripted group (container) (typed FeaturePython)
  n = 1
  ref = C_element
FEATURE [App::DocumentObjectGroupPython] O_element059  label="O_element : 030"  # scripted group (container) (typed FeaturePython)
  n = 3
  ref = O_element
FEATURE [App::DocumentObjectGroupPython] G4_MAGNESIUM_CARBONATE  # scripted group (container) (typed FeaturePython)
  Dunit = g/cm3
  Dvalue = 2.958
  Group = -> [Mg_element005,C_element058,O_element059]
  conduct = 2
  density = 1
  expand = 3
  formula = G4_MAGNESIUM_CARBONATE
  name = G4_MAGNESIUM_CARBONATE
  specific = 4
FEATURE [App::DocumentObjectGroupPython] Mg_element006  label="Mg_element : 002"  # scripted group (container) (typed FeaturePython)
  n = 1
  ref = Mg_element
FEATURE [App::DocumentObjectGroupPython] F_element013  label="F_element : 005"  # scripted group (container) (typed FeaturePython)
  n = 2
  ref = F_element
FEATURE [App::DocumentObjectGroupPython] G4_MAGNESIUM_FLUORIDE  # scripted group (container) (typed FeaturePython)
  Dunit = g/cm3
  Dvalue = 3
  Group = -> [Mg_element006,F_element013]
  conduct = 2
  density = 1
  expand = 3
  formula = G4_MAGNESIUM_FLUORIDE
  name = G4_MAGNESIUM_FLUORIDE
  specific = 4
FEATURE [App::DocumentObjectGroupPython] Mg_element007  label="Mg_element : 003"  # scripted group (container) (typed FeaturePython)
  n = 1
  ref = Mg_element
FEATURE [App::DocumentObjectGroupPython] O_element060  label="O_element : 031"  # scripted group (container) (typed FeaturePython)
  n = 1
  ref = O_element
FEATURE [App::DocumentObjectGroupPython] G4_MAGNESIUM_OXIDE  # scripted group (container) (typed FeaturePython)
  Dunit = g/cm3
  Dvalue = 3.58
  Group = -> [Mg_element007,O_element060]
  conduct = 2
  density = 1
  expand = 3
  formula = G4_MAGNESIUM_OXIDE
  name = G4_MAGNESIUM_OXIDE
  specific = 4
FEATURE [App::DocumentObjectGroupPython] Mg_element008  label="Mg_element : 004"  # scripted group (container) (typed FeaturePython)
  n = 1
  ref = Mg_element
FEATURE [App::DocumentObjectGroupPython] B_element006  label="B_element : 006"  # scripted group (container) (typed FeaturePython)
  n = 4
  ref = B_element
FEATURE [App::DocumentObjectGroupPython] O_element061  label="O_element : 032"  # scripted group (container) (typed FeaturePython)
  n = 7
  ref = O_element
FEATURE [App::DocumentObjectGroupPython] G4_MAGNESIUM_TETRABORATE  # scripted group (container) (typed FeaturePython)
  Dunit = g/cm3
  Dvalue = 2.53
  Group = -> [Mg_element008,B_element006,O_element061]
  conduct = 2
  density = 1
  expand = 3
  formula = G4_MAGNESIUM_TETRABORATE
  name = G4_MAGNESIUM_TETRABORATE
  specific = 4
FEATURE [App::DocumentObjectGroupPython] Hg_element001  label="Hg_element : 1"  # scripted group (container) (typed FeaturePython)
  n = 1
  ref = Hg_element
FEATURE [App::DocumentObjectGroupPython] I_element004  label="I_element : 2"  # scripted group (container) (typed FeaturePython)
  n = 2
  ref = I_element
FEATURE [App::DocumentObjectGroupPython] G4_MERCURIC_IODIDE  # scripted group (container) (typed FeaturePython)
  Dunit = g/cm3
  Dvalue = 6.36
  Group = -> [Hg_element001,I_element004]
  conduct = 2
  density = 1
  expand = 3
  formula = G4_MERCURIC_IODIDE
  name = G4_MERCURIC_IODIDE
  specific = 4
FEATURE [App::DocumentObjectGroupPython] C_element059  label="C_element : 032"  # scripted group (container) (typed FeaturePython)
  n = 1
  ref = C_element
FEATURE [App::DocumentObjectGroupPython] H_element053  label="H_element : 028"  # scripted group (container) (typed FeaturePython)
  n = 4
  ref = H_element
FEATURE [App::DocumentObjectGroupPython] G4_METHANE  # scripted group (container) (typed FeaturePython)
  Dunit = g/cm3
  Dvalue = 0.000667151
  Group = -> [C_element059,H_element053]
  conduct = 2
  density = 1
  expand = 3
  formula = G4_METHANE
  name = G4_METHANE
  specific = 4
FEATURE [App::DocumentObjectGroupPython] C_element060  label="C_element : 033"  # scripted group (container) (typed FeaturePython)
  n = 1
  ref = C_element
FEATURE [App::DocumentObjectGroupPython] H_element054  label="H_element : 029"  # scripted group (container) (typed FeaturePython)
  n = 4
  ref = H_element
FEATURE [App::DocumentObjectGroupPython] O_element062  label="O_element : 033"  # scripted group (container) (typed FeaturePython)
  n = 1
  ref = O_element
FEATURE [App::DocumentObjectGroupPython] G4_METHANOL  # scripted group (container) (typed FeaturePython)
  Dunit = g/cm3
  Dvalue = 0.7914
  Group = -> [C_element060,H_element054,O_element062]
  conduct = 2
  density = 1
  expand = 3
  formula = G4_METHANOL
  name = G4_METHANOL
  specific = 4
FEATURE [App::DocumentObjectGroupPython] H_element055  label="H_element : 0.134"  # scripted group (container) (typed FeaturePython)
  n = 0.13404
FEATURE [App::DocumentObjectGroupPython] C_element061  label="C_element : 0.778"  # scripted group (container) (typed FeaturePython)
  n = 0.77796
FEATURE [App::DocumentObjectGroupPython] O_element063  label="O_element : 0.035"  # scripted group (container) (typed FeaturePython)
  n = 0.03502
FEATURE [App::DocumentObjectGroupPython] Mg_element009  label="Mg_element : 0.039"  # scripted group (container) (typed FeaturePython)
  n = 0.038594
FEATURE [App::DocumentObjectGroupPython] Ti_element002  label="Ti_element : 0.014"  # scripted group (container) (typed FeaturePython)
  n = 0.014386
FEATURE [App::DocumentObjectGroupPython] G4_MIX_D_WAX  # scripted group (container) (typed FeaturePython)
  Dunit = g/cm3
  Dvalue = 0.99
  Group = -> [H_element055,C_element061,O_element063,Mg_element009,Ti_element002]
  conduct = 2
  density = 1
  expand = 3
  formula = G4_MIX_D_WAX
  name = G4_MIX_D_WAX
  specific = 4
FEATURE [App::DocumentObjectGroupPython] H_element056  label="H_element : 0.135"  # scripted group (container) (typed FeaturePython)
  n = 0.081192
FEATURE [App::DocumentObjectGroupPython] C_element062  label="C_element : 0.583"  # scripted group (container) (typed FeaturePython)
  n = 0.583442
FEATURE [App::DocumentObjectGroupPython] N_element024  label="N_element : 0.018"  # scripted group (container) (typed FeaturePython)
  n = 0.017798
FEATURE [App::DocumentObjectGroupPython] O_element064  label="O_element : 0.186"  # scripted group (container) (typed FeaturePython)
  n = 0.186381
FEATURE [App::DocumentObjectGroupPython] Mg_element010  label="Mg_element : 0.130"  # scripted group (container) (typed FeaturePython)
  n = 0.130287
FEATURE [App::DocumentObjectGroupPython] Cl_element015  label="Cl_element : 0.588"  # scripted group (container) (typed FeaturePython)
  n = 0.0009
FEATURE [App::DocumentObjectGroupPython] G4_MS20_TISSUE  # scripted group (container) (typed FeaturePython)
  Dunit = g/cm3
  Dvalue = 1
  Group = -> [H_element056,C_element062,N_element024,O_element064,Mg_element010,Cl_element015]
  conduct = 2
  density = 1
  expand = 3
  formula = G4_MS20_TISSUE
  name = G4_MS20_TISSUE
  specific = 4
FEATURE [App::DocumentObjectGroupPython] H_element057  label="H_element : 0.136"  # scripted group (container) (typed FeaturePython)
  n = 0.102
FEATURE [App::DocumentObjectGroupPython] C_element063  label="C_element : 0.143"  # scripted group (container) (typed FeaturePython)
  n = 0.143
FEATURE [App::DocumentObjectGroupPython] N_element025  label="N_element : 0.034"  # scripted group (container) (typed FeaturePython)
  n = 0.034
FEATURE [App::DocumentObjectGroupPython] O_element065  label="O_element : 0.710"  # scripted group (container) (typed FeaturePython)
  n = 0.71
FEATURE [App::DocumentObjectGroupPython] Na_element011  label="Na_element : 0.098"  # scripted group (container) (typed FeaturePython)
  n = 0.001
FEATURE [App::DocumentObjectGroupPython] P_element007  label="P_element : 0.002"  # scripted group (container) (typed FeaturePython)
  n = 0.002
FEATURE [App::DocumentObjectGroupPython] S_element017  label="S_element : 0.018"  # scripted group (container) (typed FeaturePython)
  n = 0.003
FEATURE [App::DocumentObjectGroupPython] Cl_element016  label="Cl_element : 0.589"  # scripted group (container) (typed FeaturePython)
  n = 0.001
FEATURE [App::DocumentObjectGroupPython] K_element006  label="K_element : 0.004"  # scripted group (container) (typed FeaturePython)
  n = 0.004
FEATURE [App::DocumentObjectGroupPython] G4_MUSCLE_SKELETAL_ICRP  # scripted group (container) (typed FeaturePython)
  Dunit = g/cm3
  Dvalue = 1.05
  Group = -> [H_element057,C_element063,N_element025,O_element065,Na_element011,P_element007,S_element017,Cl_element016,K_element006]
  conduct = 2
  density = 1
  expand = 3
  formula = G4_MUSCLE_SKELETAL_ICRP
  name = G4_MUSCLE_SKELETAL_ICRP
  specific = 4
FEATURE [App::DocumentObjectGroupPython] H_element058  label="H_element : 0.137"  # scripted group (container) (typed FeaturePython)
  n = 0.102102
FEATURE [App::DocumentObjectGroupPython] C_element064  label="C_element : 0.123"  # scripted group (container) (typed FeaturePython)
  n = 0.123123
FEATURE [App::DocumentObjectGroupPython] N_element026  label="N_element : 0.756"  # scripted group (container) (typed FeaturePython)
  n = 0.035035
FEATURE [App::DocumentObjectGroupPython] O_element066  label="O_element : 0.730"  # scripted group (container) (typed FeaturePython)
  n = 0.72973
FEATURE [App::DocumentObjectGroupPython] Na_element012  label="Na_element : 0.099"  # scripted group (container) (typed FeaturePython)
  n = 0.001001
FEATURE [App::DocumentObjectGroupPython] P_element008  label="P_element : 0.106"  # scripted group (container) (typed FeaturePython)
  n = 0.002002
FEATURE [App::DocumentObjectGroupPython] S_element018  label="S_element : 0.019"  # scripted group (container) (typed FeaturePython)
  n = 0.004004
FEATURE [App::DocumentObjectGroupPython] K_element007  label="K_element : 0.016"  # scripted group (container) (typed FeaturePython)
  n = 0.003003
FEATURE [App::DocumentObjectGroupPython] G4_MUSCLE_STRIATED_ICRU  # scripted group (container) (typed FeaturePython)
  Dunit = g/cm3
  Dvalue = 1.04
  Group = -> [H_element058,C_element064,N_element026,O_element066,Na_element012,P_element008,S_element018,K_element007]
  conduct = 2
  density = 1
  expand = 3
  formula = G4_MUSCLE_STRIATED_ICRU
  name = G4_MUSCLE_STRIATED_ICRU
  specific = 4
FEATURE [App::DocumentObjectGroupPython] H_element059  label="H_element : 0.098"  # scripted group (container) (typed FeaturePython)
  n = 0.0982341
FEATURE [App::DocumentObjectGroupPython] C_element065  label="C_element : 0.156"  # scripted group (container) (typed FeaturePython)
  n = 0.156214
FEATURE [App::DocumentObjectGroupPython] N_element027  label="N_element : 0.757"  # scripted group (container) (typed FeaturePython)
  n = 0.035451
FEATURE [App::DocumentObjectGroupPython] O_element067  label="O_element : 0.880"  # scripted group (container) (typed FeaturePython)
  n = 0.710101
FEATURE [App::DocumentObjectGroupPython] G4_MUSCLE_WITH_SUCROSE  # scripted group (container) (typed FeaturePython)
  Dunit = g/cm3
  Dvalue = 1.11
  Group = -> [H_element059,C_element065,N_element027,O_element067]
  conduct = 2
  density = 1
  expand = 3
  formula = G4_MUSCLE_WITH_SUCROSE
  name = G4_MUSCLE_WITH_SUCROSE
  specific = 4
FEATURE [App::DocumentObjectGroupPython] H_element060  label="H_element : 0.138"  # scripted group (container) (typed FeaturePython)
  n = 0.101969
FEATURE [App::DocumentObjectGroupPython] C_element066  label="C_element : 0.120"  # scripted group (container) (typed FeaturePython)
  n = 0.120058
FEATURE [App::DocumentObjectGroupPython] N_element028  label="N_element : 0.758"  # scripted group (container) (typed FeaturePython)
  n = 0.035451
FEATURE [App::DocumentObjectGroupPython] O_element068  label="O_element : 0.743"  # scripted group (container) (typed FeaturePython)
  n = 0.742522
FEATURE [App::DocumentObjectGroupPython] G4_MUSCLE_WITHOUT_SUCROSE  # scripted group (container) (typed FeaturePython)
  Dunit = g/cm3
  Dvalue = 1.07
  Group = -> [H_element060,C_element066,N_element028,O_element068]
  conduct = 2
  density = 1
  expand = 3
  formula = G4_MUSCLE_WITHOUT_SUCROSE
  name = G4_MUSCLE_WITHOUT_SUCROSE
  specific = 4
FEATURE [App::DocumentObjectGroupPython] C_element067  label="C_element : 10"  # scripted group (container) (typed FeaturePython)
  n = 10
  ref = C_element
FEATURE [App::DocumentObjectGroupPython] H_element061  label="H_element : 030"  # scripted group (container) (typed FeaturePython)
  n = 8
  ref = H_element
FEATURE [App::DocumentObjectGroupPython] G4_NAPHTHALENE  # scripted group (container) (typed FeaturePython)
  Dunit = g/cm3
  Dvalue = 1.145
  Group = -> [C_element067,H_element061]
  conduct = 2
  density = 1
  expand = 3
  formula = G4_NAPHTHALENE
  name = G4_NAPHTHALENE
  specific = 4
FEATURE [App::DocumentObjectGroupPython] C_element068  label="C_element : 034"  # scripted group (container) (typed FeaturePython)
  n = 6
  ref = C_element
FEATURE [App::DocumentObjectGroupPython] H_element062  label="H_element : 031"  # scripted group (container) (typed FeaturePython)
  n = 5
  ref = H_element
FEATURE [App::DocumentObjectGroupPython] N_element029  label="N_element : 012"  # scripted group (container) (typed FeaturePython)
  n = 1
  ref = N_element
FEATURE [App::DocumentObjectGroupPython] O_element069  label="O_element : 034"  # scripted group (container) (typed FeaturePython)
  n = 2
  ref = O_element
FEATURE [App::DocumentObjectGroupPython] G4_NITROBENZENE  # scripted group (container) (typed FeaturePython)
  Dunit = g/cm3
  Dvalue = 1.19867
  Group = -> [C_element068,H_element062,N_element029,O_element069]
  conduct = 2
  density = 1
  expand = 3
  formula = G4_NITROBENZENE
  name = G4_NITROBENZENE
  specific = 4
FEATURE [App::DocumentObjectGroupPython] N_element030  label="N_element : 013"  # scripted group (container) (typed FeaturePython)
  n = 2
  ref = N_element
FEATURE [App::DocumentObjectGroupPython] O_element070  label="O_element : 035"  # scripted group (container) (typed FeaturePython)
  n = 1
  ref = O_element
FEATURE [App::DocumentObjectGroupPython] G4_NITROUS_OXIDE  # scripted group (container) (typed FeaturePython)
  Dunit = g/cm3
  Dvalue = 0.00183094
  Group = -> [N_element030,O_element070]
  conduct = 2
  density = 1
  expand = 3
  formula = G4_NITROUS_OXIDE
  name = G4_NITROUS_OXIDE
  specific = 4
FEATURE [App::DocumentObjectGroupPython] H_element063  label="H_element : 0.104"  # scripted group (container) (typed FeaturePython)
  n = 0.103509
FEATURE [App::DocumentObjectGroupPython] C_element069  label="C_element : 0.648"  # scripted group (container) (typed FeaturePython)
  n = 0.648416
FEATURE [App::DocumentObjectGroupPython] N_element031  label="N_element : 0.100"  # scripted group (container) (typed FeaturePython)
  n = 0.0995361
FEATURE [App::DocumentObjectGroupPython] O_element071  label="O_element : 0.149"  # scripted group (container) (typed FeaturePython)
  n = 0.148539
FEATURE [App::DocumentObjectGroupPython] G4_NYLON_8062  label="G4_NYLON-8062"  # scripted group (container) (typed FeaturePython)
  Dunit = g/cm3
  Dvalue = 1.08
  Group = -> [H_element063,C_element069,N_element031,O_element071]
  conduct = 2
  density = 1
  expand = 3
  formula = G4_NYLON-8062
  name = G4_NYLON-8062
  specific = 4
FEATURE [App::DocumentObjectGroupPython] C_element070  label="C_element : 035"  # scripted group (container) (typed FeaturePython)
  n = 6
  ref = C_element
FEATURE [App::DocumentObjectGroupPython] H_element064  label="H_element : 11"  # scripted group (container) (typed FeaturePython)
  n = 11
  ref = H_element
FEATURE [App::DocumentObjectGroupPython] N_element032  label="N_element : 014"  # scripted group (container) (typed FeaturePython)
  n = 1
  ref = N_element
FEATURE [App::DocumentObjectGroupPython] O_element072  label="O_element : 036"  # scripted group (container) (typed FeaturePython)
  n = 1
  ref = O_element
FEATURE [App::DocumentObjectGroupPython] G4_NYLON_6_6  label="G4_NYLON-6-6"  # scripted group (container) (typed FeaturePython)
  Dunit = g/cm3
  Dvalue = 1.14
  Group = -> [C_element070,H_element064,N_element032,O_element072]
  conduct = 2
  density = 1
  expand = 3
  formula = G4_NYLON-6-6
  name = G4_NYLON-6-6
  specific = 4
FEATURE [App::DocumentObjectGroupPython] H_element065  label="H_element : 0.139"  # scripted group (container) (typed FeaturePython)
  n = 0.107062
FEATURE [App::DocumentObjectGroupPython] C_element071  label="C_element : 0.680"  # scripted group (container) (typed FeaturePython)
  n = 0.680449
FEATURE [App::DocumentObjectGroupPython] N_element033  label="N_element : 0.099"  # scripted group (container) (typed FeaturePython)
  n = 0.099189
FEATURE [App::DocumentObjectGroupPython] O_element073  label="O_element : 0.113"  # scripted group (container) (typed FeaturePython)
  n = 0.1133
FEATURE [App::DocumentObjectGroupPython] G4_NYLON_6_10  label="G4_NYLON-6-10"  # scripted group (container) (typed FeaturePython)
  Dunit = g/cm3
  Dvalue = 1.14
  Group = -> [H_element065,C_element071,N_element033,O_element073]
  conduct = 2
  density = 1
  expand = 3
  formula = G4_NYLON-6-10
  name = G4_NYLON-6-10
  specific = 4
FEATURE [App::DocumentObjectGroupPython] H_element066  label="H_element : 0.140"  # scripted group (container) (typed FeaturePython)
  n = 0.115476
FEATURE [App::DocumentObjectGroupPython] C_element072  label="C_element : 0.721"  # scripted group (container) (typed FeaturePython)
  n = 0.720818
FEATURE [App::DocumentObjectGroupPython] N_element034  label="N_element : 0.076"  # scripted group (container) (typed FeaturePython)
  n = 0.0764169
FEATURE [App::DocumentObjectGroupPython] O_element074  label="O_element : 0.087"  # scripted group (container) (typed FeaturePython)
  n = 0.0872889
FEATURE [App::DocumentObjectGroupPython] G4_NYLON_11_RILSAN  label="G4_NYLON-11_RILSAN"  # scripted group (container) (typed FeaturePython)
  Dunit = g/cm3
  Dvalue = 1.425
  Group = -> [H_element066,C_element072,N_element034,O_element074]
  conduct = 2
  density = 1
  expand = 3
  formula = G4_NYLON-11_RILSAN
  name = G4_NYLON-11_RILSAN
  specific = 4
FEATURE [App::DocumentObjectGroupPython] C_element073  label="C_element : 8"  # scripted group (container) (typed FeaturePython)
  n = 8
  ref = C_element
FEATURE [App::DocumentObjectGroupPython] H_element067  label="H_element : 18"  # scripted group (container) (typed FeaturePython)
  n = 18
  ref = H_element
FEATURE [App::DocumentObjectGroupPython] G4_OCTANE  # scripted group (container) (typed FeaturePython)
  Dunit = g/cm3
  Dvalue = 0.7026
  Group = -> [C_element073,H_element067]
  conduct = 2
  density = 1
  expand = 3
  formula = G4_OCTANE
  name = G4_OCTANE
  specific = 4
FEATURE [App::DocumentObjectGroupPython] C_element074  label="C_element : 25"  # scripted group (container) (typed FeaturePython)
  n = 25
  ref = C_element
FEATURE [App::DocumentObjectGroupPython] H_element068  label="H_element : 52"  # scripted group (container) (typed FeaturePython)
  n = 52
  ref = H_element
FEATURE [App::DocumentObjectGroupPython] G4_PARAFFIN  # scripted group (container) (typed FeaturePython)
  Dunit = g/cm3
  Dvalue = 0.93
  Group = -> [C_element074,H_element068]
  conduct = 2
  density = 1
  expand = 3
  formula = G4_PARAFFIN
  name = G4_PARAFFIN
  specific = 4
FEATURE [App::DocumentObjectGroupPython] C_element075  label="C_element : 036"  # scripted group (container) (typed FeaturePython)
  n = 5
  ref = C_element
FEATURE [App::DocumentObjectGroupPython] H_element069  label="H_element : 032"  # scripted group (container) (typed FeaturePython)
  n = 12
  ref = H_element
FEATURE [App::DocumentObjectGroupPython] G4_N_PENTANE  label="G4_N-PENTANE"  # scripted group (container) (typed FeaturePython)
  Dunit = g/cm3
  Dvalue = 0.6262
  Group = -> [C_element075,H_element069]
  conduct = 2
  density = 1
  expand = 3
  formula = G4_N-PENTANE
  name = G4_N-PENTANE
  specific = 4
FEATURE [App::DocumentObjectGroupPython] H_element070  label="H_element : 0.014"  # scripted group (container) (typed FeaturePython)
  n = 0.0141
FEATURE [App::DocumentObjectGroupPython] C_element076  label="C_element : 0.072"  # scripted group (container) (typed FeaturePython)
  n = 0.072261
FEATURE [App::DocumentObjectGroupPython] N_element035  label="N_element : 0.019"  # scripted group (container) (typed FeaturePython)
  n = 0.01932
FEATURE [App::DocumentObjectGroupPython] O_element075  label="O_element : 0.066"  # scripted group (container) (typed FeaturePython)
  n = 0.066101
FEATURE [App::DocumentObjectGroupPython] S_element019  label="S_element : 0.020"  # scripted group (container) (typed FeaturePython)
  n = 0.00189
FEATURE [App::DocumentObjectGroupPython] Br_element004  label="Br_element : 0.349"  # scripted group (container) (typed FeaturePython)
  n = 0.349103
FEATURE [App::DocumentObjectGroupPython] Ag_element001  label="Ag_element : 0.474"  # scripted group (container) (typed FeaturePython)
  n = 0.474105
FEATURE [App::DocumentObjectGroupPython] I_element005  label="I_element : 0.003"  # scripted group (container) (typed FeaturePython)
  n = 0.00312
FEATURE [App::DocumentObjectGroupPython] G4_PHOTO_EMULSION  # scripted group (container) (typed FeaturePython)
  Dunit = g/cm3
  Dvalue = 3.815
  Group = -> [H_element070,C_element076,N_element035,O_element075,S_element019,Br_element004,Ag_element001,I_element005]
  conduct = 2
  density = 1
  expand = 3
  formula = G4_PHOTO_EMULSION
  name = G4_PHOTO_EMULSION
  specific = 4
FEATURE [App::DocumentObjectGroupPython] C_element077  label="C_element : 9"  # scripted group (container) (typed FeaturePython)
  n = 9
  ref = C_element
FEATURE [App::DocumentObjectGroupPython] H_element071  label="H_element : 033"  # scripted group (container) (typed FeaturePython)
  n = 10
  ref = H_element
FEATURE [App::DocumentObjectGroupPython] G4_PLASTIC_SC_VINYLTOLUENE  # scripted group (container) (typed FeaturePython)
  Dunit = g/cm3
  Dvalue = 1.032
  Group = -> [C_element077,H_element071]
  conduct = 2
  density = 1
  expand = 3
  formula = G4_PLASTIC_SC_VINYLTOLUENE
  name = G4_PLASTIC_SC_VINYLTOLUENE
  specific = 4
FEATURE [App::DocumentObjectGroupPython] Pu_element001  label="Pu_element : 1"  # scripted group (container) (typed FeaturePython)
  n = 1
  ref = Pu_element
FEATURE [App::DocumentObjectGroupPython] O_element076  label="O_element : 037"  # scripted group (container) (typed FeaturePython)
  n = 2
  ref = O_element
FEATURE [App::DocumentObjectGroupPython] G4_PLUTONIUM_DIOXIDE  # scripted group (container) (typed FeaturePython)
  Dunit = g/cm3
  Dvalue = 11.46
  Group = -> [Pu_element001,O_element076]
  conduct = 2
  density = 1
  expand = 3
  formula = G4_PLUTONIUM_DIOXIDE
  name = G4_PLUTONIUM_DIOXIDE
  specific = 4
FEATURE [App::DocumentObjectGroupPython] C_element078  label="C_element : 037"  # scripted group (container) (typed FeaturePython)
  n = 3
  ref = C_element
FEATURE [App::DocumentObjectGroupPython] H_element072  label="H_element : 034"  # scripted group (container) (typed FeaturePython)
  n = 3
  ref = H_element
FEATURE [App::DocumentObjectGroupPython] N_element036  label="N_element : 015"  # scripted group (container) (typed FeaturePython)
  n = 1
  ref = N_element
FEATURE [App::DocumentObjectGroupPython] G4_POLYACRYLONITRILE  # scripted group (container) (typed FeaturePython)
  Dunit = g/cm3
  Dvalue = 1.17
  Group = -> [C_element078,H_element072,N_element036]
  conduct = 2
  density = 1
  expand = 3
  formula = G4_POLYACRYLONITRILE
  name = G4_POLYACRYLONITRILE
  specific = 4
FEATURE [App::DocumentObjectGroupPython] C_element079  label="C_element : 16"  # scripted group (container) (typed FeaturePython)
  n = 16
  ref = C_element
FEATURE [App::DocumentObjectGroupPython] H_element073  label="H_element : 035"  # scripted group (container) (typed FeaturePython)
  n = 14
  ref = H_element
FEATURE [App::DocumentObjectGroupPython] O_element077  label="O_element : 038"  # scripted group (container) (typed FeaturePython)
  n = 3
  ref = O_element
FEATURE [App::DocumentObjectGroupPython] G4_POLYCARBONATE  # scripted group (container) (typed FeaturePython)
  Dunit = g/cm3
  Dvalue = 1.2
  Group = -> [C_element079,H_element073,O_element077]
  conduct = 2
  density = 1
  expand = 3
  formula = G4_POLYCARBONATE
  name = G4_POLYCARBONATE
  specific = 4
FEATURE [App::DocumentObjectGroupPython] C_element080  label="C_element : 038"  # scripted group (container) (typed FeaturePython)
  n = 8
  ref = C_element
FEATURE [App::DocumentObjectGroupPython] H_element074  label="H_element : 036"  # scripted group (container) (typed FeaturePython)
  n = 7
  ref = H_element
FEATURE [App::DocumentObjectGroupPython] Cl_element017  label="Cl_element : 007"  # scripted group (container) (typed FeaturePython)
  n = 1
  ref = Cl_element
FEATURE [App::DocumentObjectGroupPython] G4_POLYCHLOROSTYRENE  # scripted group (container) (typed FeaturePython)
  Dunit = g/cm3
  Dvalue = 1.3
  Group = -> [C_element080,H_element074,Cl_element017]
  conduct = 2
  density = 1
  expand = 3
  formula = G4_POLYCHLOROSTYRENE
  name = G4_POLYCHLOROSTYRENE
  specific = 4
FEATURE [App::DocumentObjectGroupPython] C_element081  label="C_element : 039"  # scripted group (container) (typed FeaturePython)
  n = 1
  ref = C_element
FEATURE [App::DocumentObjectGroupPython] H_element075  label="H_element : 037"  # scripted group (container) (typed FeaturePython)
  n = 2
  ref = H_element
FEATURE [App::DocumentObjectGroupPython] G4_POLYETHYLENE  # scripted group (container) (typed FeaturePython)
  Dunit = g/cm3
  Dvalue = 0.94
  Group = -> [C_element081,H_element075]
  conduct = 2
  density = 1
  expand = 3
  formula = G4_POLYETHYLENE
  name = G4_POLYETHYLENE
  specific = 4
FEATURE [App::DocumentObjectGroupPython] C_element082  label="C_element : 040"  # scripted group (container) (typed FeaturePython)
  n = 10
  ref = C_element
FEATURE [App::DocumentObjectGroupPython] H_element076  label="H_element : 038"  # scripted group (container) (typed FeaturePython)
  n = 8
  ref = H_element
FEATURE [App::DocumentObjectGroupPython] O_element078  label="O_element : 039"  # scripted group (container) (typed FeaturePython)
  n = 4
  ref = O_element
FEATURE [App::DocumentObjectGroupPython] G4_MYLAR  # scripted group (container) (typed FeaturePython)
  Dunit = g/cm3
  Dvalue = 1.4
  Group = -> [C_element082,H_element076,O_element078]
  conduct = 2
  density = 1
  expand = 3
  formula = G4_MYLAR
  name = G4_MYLAR
  specific = 4
FEATURE [App::DocumentObjectGroupPython] C_element083  label="C_element : 041"  # scripted group (container) (typed FeaturePython)
  n = 5
  ref = C_element
FEATURE [App::DocumentObjectGroupPython] H_element077  label="H_element : 039"  # scripted group (container) (typed FeaturePython)
  n = 8
  ref = H_element
FEATURE [App::DocumentObjectGroupPython] O_element079  label="O_element : 040"  # scripted group (container) (typed FeaturePython)
  n = 2
  ref = O_element
FEATURE [App::DocumentObjectGroupPython] G4_PLEXIGLASS  # scripted group (container) (typed FeaturePython)
  Dunit = g/cm3
  Dvalue = 1.19
  Group = -> [C_element083,H_element077,O_element079]
  conduct = 2
  density = 1
  expand = 3
  formula = G4_PLEXIGLASS
  name = G4_PLEXIGLASS
  specific = 4
FEATURE [App::DocumentObjectGroupPython] C_element084  label="C_element : 042"  # scripted group (container) (typed FeaturePython)
  n = 1
  ref = C_element
FEATURE [App::DocumentObjectGroupPython] H_element078  label="H_element : 040"  # scripted group (container) (typed FeaturePython)
  n = 2
  ref = H_element
FEATURE [App::DocumentObjectGroupPython] O_element080  label="O_element : 041"  # scripted group (container) (typed FeaturePython)
  n = 1
  ref = O_element
FEATURE [App::DocumentObjectGroupPython] G4_POLYOXYMETHYLENE  # scripted group (container) (typed FeaturePython)
  Dunit = g/cm3
  Dvalue = 1.425
  Group = -> [C_element084,H_element078,O_element080]
  conduct = 2
  density = 1
  expand = 3
  formula = G4_POLYOXYMETHYLENE
  name = G4_POLYOXYMETHYLENE
  specific = 4
FEATURE [App::DocumentObjectGroupPython] C_element085  label="C_element : 043"  # scripted group (container) (typed FeaturePython)
  n = 2
  ref = C_element
FEATURE [App::DocumentObjectGroupPython] H_element079  label="H_element : 041"  # scripted group (container) (typed FeaturePython)
  n = 4
  ref = H_element
FEATURE [App::DocumentObjectGroupPython] G4_POLYPROPYLENE  # scripted group (container) (typed FeaturePython)
  Dunit = g/cm3
  Dvalue = 0.9
  Group = -> [C_element085,H_element079]
  conduct = 2
  density = 1
  expand = 3
  formula = G4_POLYPROPYLENE
  name = G4_POLYPROPYLENE
  specific = 4
FEATURE [App::DocumentObjectGroupPython] C_element086  label="C_element : 044"  # scripted group (container) (typed FeaturePython)
  n = 8
  ref = C_element
FEATURE [App::DocumentObjectGroupPython] H_element080  label="H_element : 042"  # scripted group (container) (typed FeaturePython)
  n = 8
  ref = H_element
FEATURE [App::DocumentObjectGroupPython] G4_POLYSTYRENE  # scripted group (container) (typed FeaturePython)
  Dunit = g/cm3
  Dvalue = 1.06
  Group = -> [C_element086,H_element080]
  conduct = 2
  density = 1
  expand = 3
  formula = G4_POLYSTYRENE
  name = G4_POLYSTYRENE
  specific = 4
FEATURE [App::DocumentObjectGroupPython] C_element087  label="C_element : 045"  # scripted group (container) (typed FeaturePython)
  n = 2
  ref = C_element
FEATURE [App::DocumentObjectGroupPython] F_element014  label="F_element : 4"  # scripted group (container) (typed FeaturePython)
  n = 4
  ref = F_element
FEATURE [App::DocumentObjectGroupPython] G4_TEFLON  # scripted group (container) (typed FeaturePython)
  Dunit = g/cm3
  Dvalue = 2.2
  Group = -> [C_element087,F_element014]
  conduct = 2
  density = 1
  expand = 3
  formula = G4_TEFLON
  name = G4_TEFLON
  specific = 4
FEATURE [App::DocumentObjectGroupPython] C_element088  label="C_element : 046"  # scripted group (container) (typed FeaturePython)
  n = 2
  ref = C_element
FEATURE [App::DocumentObjectGroupPython] F_element015  label="F_element : 006"  # scripted group (container) (typed FeaturePython)
  n = 3
  ref = F_element
FEATURE [App::DocumentObjectGroupPython] Cl_element018  label="Cl_element : 008"  # scripted group (container) (typed FeaturePython)
  n = 1
  ref = Cl_element
FEATURE [App::DocumentObjectGroupPython] G4_POLYTRIFLUOROCHLOROETHYLENE  # scripted group (container) (typed FeaturePython)
  Dunit = g/cm3
  Dvalue = 2.1
  Group = -> [C_element088,F_element015,Cl_element018]
  conduct = 2
  density = 1
  expand = 3
  formula = G4_POLYTRIFLUOROCHLOROETHYLENE
  name = G4_POLYTRIFLUOROCHLOROETHYLENE
  specific = 4
FEATURE [App::DocumentObjectGroupPython] C_element089  label="C_element : 047"  # scripted group (container) (typed FeaturePython)
  n = 4
  ref = C_element
FEATURE [App::DocumentObjectGroupPython] H_element081  label="H_element : 043"  # scripted group (container) (typed FeaturePython)
  n = 6
  ref = H_element
FEATURE [App::DocumentObjectGroupPython] O_element081  label="O_element : 042"  # scripted group (container) (typed FeaturePython)
  n = 2
  ref = O_element
FEATURE [App::DocumentObjectGroupPython] G4_POLYVINYL_ACETATE  # scripted group (container) (typed FeaturePython)
  Dunit = g/cm3
  Dvalue = 1.19
  Group = -> [C_element089,H_element081,O_element081]
  conduct = 2
  density = 1
  expand = 3
  formula = G4_POLYVINYL_ACETATE
  name = G4_POLYVINYL_ACETATE
  specific = 4
FEATURE [App::DocumentObjectGroupPython] C_element090  label="C_element : 048"  # scripted group (container) (typed FeaturePython)
  n = 2
  ref = C_element
FEATURE [App::DocumentObjectGroupPython] H_element082  label="H_element : 044"  # scripted group (container) (typed FeaturePython)
  n = 4
  ref = H_element
FEATURE [App::DocumentObjectGroupPython] O_element082  label="O_element : 043"  # scripted group (container) (typed FeaturePython)
  n = 1
  ref = O_element
FEATURE [App::DocumentObjectGroupPython] G4_POLYVINYL_ALCOHOL  # scripted group (container) (typed FeaturePython)
  Dunit = g/cm3
  Dvalue = 1.3
  Group = -> [C_element090,H_element082,O_element082]
  conduct = 2
  density = 1
  expand = 3
  formula = G4_POLYVINYL_ALCOHOL
  name = G4_POLYVINYL_ALCOHOL
  specific = 4
FEATURE [App::DocumentObjectGroupPython] C_element091  label="C_element : 049"  # scripted group (container) (typed FeaturePython)
  n = 8
  ref = C_element
FEATURE [App::DocumentObjectGroupPython] H_element083  label="H_element : 045"  # scripted group (container) (typed FeaturePython)
  n = 14
  ref = H_element
FEATURE [App::DocumentObjectGroupPython] O_element083  label="O_element : 044"  # scripted group (container) (typed FeaturePython)
  n = 2
  ref = O_element
FEATURE [App::DocumentObjectGroupPython] G4_POLYVINYL_BUTYRAL  # scripted group (container) (typed FeaturePython)
  Dunit = g/cm3
  Dvalue = 1.12
  Group = -> [C_element091,H_element083,O_element083]
  conduct = 2
  density = 1
  expand = 3
  formula = G4_POLYVINYL_BUTYRAL
  name = G4_POLYVINYL_BUTYRAL
  specific = 4
FEATURE [App::DocumentObjectGroupPython] C_element092  label="C_element : 050"  # scripted group (container) (typed FeaturePython)
  n = 2
  ref = C_element
FEATURE [App::DocumentObjectGroupPython] H_element084  label="H_element : 046"  # scripted group (container) (typed FeaturePython)
  n = 3
  ref = H_element
FEATURE [App::DocumentObjectGroupPython] Cl_element019  label="Cl_element : 009"  # scripted group (container) (typed FeaturePython)
  n = 1
  ref = Cl_element
FEATURE [App::DocumentObjectGroupPython] G4_POLYVINYL_CHLORIDE  # scripted group (container) (typed FeaturePython)
  Dunit = g/cm3
  Dvalue = 1.3
  Group = -> [C_element092,H_element084,Cl_element019]
  conduct = 2
  density = 1
  expand = 3
  formula = G4_POLYVINYL_CHLORIDE
  name = G4_POLYVINYL_CHLORIDE
  specific = 4
FEATURE [App::DocumentObjectGroupPython] C_element093  label="C_element : 051"  # scripted group (container) (typed FeaturePython)
  n = 2
  ref = C_element
FEATURE [App::DocumentObjectGroupPython] H_element085  label="H_element : 047"  # scripted group (container) (typed FeaturePython)
  n = 2
  ref = H_element
FEATURE [App::DocumentObjectGroupPython] Cl_element020  label="Cl_element : 010"  # scripted group (container) (typed FeaturePython)
  n = 2
  ref = Cl_element
FEATURE [App::DocumentObjectGroupPython] G4_POLYVINYLIDENE_CHLORIDE  # scripted group (container) (typed FeaturePython)
  Dunit = g/cm3
  Dvalue = 1.7
  Group = -> [C_element093,H_element085,Cl_element020]
  conduct = 2
  density = 1
  expand = 3
  formula = G4_POLYVINYLIDENE_CHLORIDE
  name = G4_POLYVINYLIDENE_CHLORIDE
  specific = 4
FEATURE [App::DocumentObjectGroupPython] C_element094  label="C_element : 052"  # scripted group (container) (typed FeaturePython)
  n = 2
  ref = C_element
FEATURE [App::DocumentObjectGroupPython] H_element086  label="H_element : 048"  # scripted group (container) (typed FeaturePython)
  n = 2
  ref = H_element
FEATURE [App::DocumentObjectGroupPython] F_element016  label="F_element : 007"  # scripted group (container) (typed FeaturePython)
  n = 2
  ref = F_element
FEATURE [App::DocumentObjectGroupPython] G4_POLYVINYLIDENE_FLUORIDE  # scripted group (container) (typed FeaturePython)
  Dunit = g/cm3
  Dvalue = 1.76
  Group = -> [C_element094,H_element086,F_element016]
  conduct = 2
  density = 1
  expand = 3
  formula = G4_POLYVINYLIDENE_FLUORIDE
  name = G4_POLYVINYLIDENE_FLUORIDE
  specific = 4
FEATURE [App::DocumentObjectGroupPython] C_element095  label="C_element : 053"  # scripted group (container) (typed FeaturePython)
  n = 6
  ref = C_element
FEATURE [App::DocumentObjectGroupPython] H_element087  label="H_element : 9"  # scripted group (container) (typed FeaturePython)
  n = 9
  ref = H_element
FEATURE [App::DocumentObjectGroupPython] N_element037  label="N_element : 016"  # scripted group (container) (typed FeaturePython)
  n = 1
  ref = N_element
FEATURE [App::DocumentObjectGroupPython] O_element084  label="O_element : 045"  # scripted group (container) (typed FeaturePython)
  n = 1
  ref = O_element
FEATURE [App::DocumentObjectGroupPython] G4_POLYVINYL_PYRROLIDONE  # scripted group (container) (typed FeaturePython)
  Dunit = g/cm3
  Dvalue = 1.25
  Group = -> [C_element095,H_element087,N_element037,O_element084]
  conduct = 2
  density = 1
  expand = 3
  formula = G4_POLYVINYL_PYRROLIDONE
  name = G4_POLYVINYL_PYRROLIDONE
  specific = 4
FEATURE [App::DocumentObjectGroupPython] K_element008  label="K_element : 1"  # scripted group (container) (typed FeaturePython)
  n = 1
  ref = K_element
FEATURE [App::DocumentObjectGroupPython] I_element006  label="I_element : 003"  # scripted group (container) (typed FeaturePython)
  n = 1
  ref = I_element
FEATURE [App::DocumentObjectGroupPython] G4_POTASSIUM_IODIDE  # scripted group (container) (typed FeaturePython)
  Dunit = g/cm3
  Dvalue = 3.13
  Group = -> [K_element008,I_element006]
  conduct = 2
  density = 1
  expand = 3
  formula = G4_POTASSIUM_IODIDE
  name = G4_POTASSIUM_IODIDE
  specific = 4
FEATURE [App::DocumentObjectGroupPython] K_element009  label="K_element : 2"  # scripted group (container) (typed FeaturePython)
  n = 2
  ref = K_element
FEATURE [App::DocumentObjectGroupPython] O_element085  label="O_element : 046"  # scripted group (container) (typed FeaturePython)
  n = 1
  ref = O_element
FEATURE [App::DocumentObjectGroupPython] G4_POTASSIUM_OXIDE  # scripted group (container) (typed FeaturePython)
  Dunit = g/cm3
  Dvalue = 2.32
  Group = -> [K_element009,O_element085]
  conduct = 2
  density = 1
  expand = 3
  formula = G4_POTASSIUM_OXIDE
  name = G4_POTASSIUM_OXIDE
  specific = 4
FEATURE [App::DocumentObjectGroupPython] C_element096  label="C_element : 054"  # scripted group (container) (typed FeaturePython)
  n = 3
  ref = C_element
FEATURE [App::DocumentObjectGroupPython] H_element088  label="H_element : 049"  # scripted group (container) (typed FeaturePython)
  n = 8
  ref = H_element
FEATURE [App::DocumentObjectGroupPython] G4_PROPANE  # scripted group (container) (typed FeaturePython)
  Dunit = g/cm3
  Dvalue = 0.00187939
  Group = -> [C_element096,H_element088]
  conduct = 2
  density = 1
  expand = 3
  formula = G4_PROPANE
  name = G4_PROPANE
  specific = 4
FEATURE [App::DocumentObjectGroupPython] C_element097  label="C_element : 055"  # scripted group (container) (typed FeaturePython)
  n = 3
  ref = C_element
FEATURE [App::DocumentObjectGroupPython] H_element089  label="H_element : 050"  # scripted group (container) (typed FeaturePython)
  n = 8
  ref = H_element
FEATURE [App::DocumentObjectGroupPython] G4_lPROPANE  # scripted group (container) (typed FeaturePython)
  Dunit = g/cm3
  Dvalue = 0.43
  Group = -> [C_element097,H_element089]
  conduct = 2
  density = 1
  expand = 3
  formula = G4_lPROPANE
  name = G4_lPROPANE
  specific = 4
FEATURE [App::DocumentObjectGroupPython] C_element098  label="C_element : 056"  # scripted group (container) (typed FeaturePython)
  n = 3
  ref = C_element
FEATURE [App::DocumentObjectGroupPython] H_element090  label="H_element : 051"  # scripted group (container) (typed FeaturePython)
  n = 8
  ref = H_element
FEATURE [App::DocumentObjectGroupPython] O_element086  label="O_element : 047"  # scripted group (container) (typed FeaturePython)
  n = 1
  ref = O_element
FEATURE [App::DocumentObjectGroupPython] G4_N_PROPYL_ALCOHOL  label="G4_N-PROPYL_ALCOHOL"  # scripted group (container) (typed FeaturePython)
  Dunit = g/cm3
  Dvalue = 0.8035
  Group = -> [C_element098,H_element090,O_element086]
  conduct = 2
  density = 1
  expand = 3
  formula = G4_N-PROPYL_ALCOHOL
  name = G4_N-PROPYL_ALCOHOL
  specific = 4
FEATURE [App::DocumentObjectGroupPython] C_element099  label="C_element : 057"  # scripted group (container) (typed FeaturePython)
  n = 5
  ref = C_element
FEATURE [App::DocumentObjectGroupPython] H_element091  label="H_element : 052"  # scripted group (container) (typed FeaturePython)
  n = 5
  ref = H_element
FEATURE [App::DocumentObjectGroupPython] N_element038  label="N_element : 017"  # scripted group (container) (typed FeaturePython)
  n = 1
  ref = N_element
FEATURE [App::DocumentObjectGroupPython] G4_PYRIDINE  # scripted group (container) (typed FeaturePython)
  Dunit = g/cm3
  Dvalue = 0.9819
  Group = -> [C_element099,H_element091,N_element038]
  conduct = 2
  density = 1
  expand = 3
  formula = G4_PYRIDINE
  name = G4_PYRIDINE
  specific = 4
FEATURE [App::DocumentObjectGroupPython] H_element092  label="H_element : 0.144"  # scripted group (container) (typed FeaturePython)
  n = 0.143711
FEATURE [App::DocumentObjectGroupPython] C_element100  label="C_element : 0.856"  # scripted group (container) (typed FeaturePython)
  n = 0.856289
FEATURE [App::DocumentObjectGroupPython] G4_RUBBER_BUTYL  # scripted group (container) (typed FeaturePython)
  Dunit = g/cm3
  Dvalue = 0.92
  Group = -> [H_element092,C_element100]
  conduct = 2
  density = 1
  expand = 3
  formula = G4_RUBBER_BUTYL
  name = G4_RUBBER_BUTYL
  specific = 4
FEATURE [App::DocumentObjectGroupPython] H_element093  label="H_element : 0.118"  # scripted group (container) (typed FeaturePython)
  n = 0.118371
FEATURE [App::DocumentObjectGroupPython] C_element101  label="C_element : 0.882"  # scripted group (container) (typed FeaturePython)
  n = 0.881629
FEATURE [App::DocumentObjectGroupPython] G4_RUBBER_NATURAL  # scripted group (container) (typed FeaturePython)
  Dunit = g/cm3
  Dvalue = 0.92
  Group = -> [H_element093,C_element101]
  conduct = 2
  density = 1
  expand = 3
  formula = G4_RUBBER_NATURAL
  name = G4_RUBBER_NATURAL
  specific = 4
FEATURE [App::DocumentObjectGroupPython] H_element094  label="H_element : 0.145"  # scripted group (container) (typed FeaturePython)
  n = 0.05692
FEATURE [App::DocumentObjectGroupPython] C_element102  label="C_element : 0.543"  # scripted group (container) (typed FeaturePython)
  n = 0.542646
FEATURE [App::DocumentObjectGroupPython] Cl_element021  label="Cl_element : 0.400"  # scripted group (container) (typed FeaturePython)
  n = 0.400434
FEATURE [App::DocumentObjectGroupPython] G4_RUBBER_NEOPRENE  # scripted group (container) (typed FeaturePython)
  Dunit = g/cm3
  Dvalue = 1.23
  Group = -> [H_element094,C_element102,Cl_element021]
  conduct = 2
  density = 1
  expand = 3
  formula = G4_RUBBER_NEOPRENE
  name = G4_RUBBER_NEOPRENE
  specific = 4
FEATURE [App::DocumentObjectGroupPython] Si_element006  label="Si_element : 1"  # scripted group (container) (typed FeaturePython)
  n = 1
  ref = Si_element
FEATURE [App::DocumentObjectGroupPython] O_element087  label="O_element : 048"  # scripted group (container) (typed FeaturePython)
  n = 2
  ref = O_element
FEATURE [App::DocumentObjectGroupPython] G4_SILICON_DIOXIDE  # scripted group (container) (typed FeaturePython)
  Dunit = g/cm3
  Dvalue = 2.32
  Group = -> [Si_element006,O_element087]
  conduct = 2
  density = 1
  expand = 3
  formula = G4_SILICON_DIOXIDE
  name = G4_SILICON_DIOXIDE
  specific = 4
FEATURE [App::DocumentObjectGroupPython] Ag_element002  label="Ag_element : 1"  # scripted group (container) (typed FeaturePython)
  n = 1
  ref = Ag_element
FEATURE [App::DocumentObjectGroupPython] Br_element005  label="Br_element : 003"  # scripted group (container) (typed FeaturePython)
  n = 1
  ref = Br_element
FEATURE [App::DocumentObjectGroupPython] G4_SILVER_BROMIDE  # scripted group (container) (typed FeaturePython)
  Dunit = g/cm3
  Dvalue = 6.473
  Group = -> [Ag_element002,Br_element005]
  conduct = 2
  density = 1
  expand = 3
  formula = G4_SILVER_BROMIDE
  name = G4_SILVER_BROMIDE
  specific = 4
FEATURE [App::DocumentObjectGroupPython] Ag_element003  label="Ag_element : 002"  # scripted group (container) (typed FeaturePython)
  n = 1
  ref = Ag_element
FEATURE [App::DocumentObjectGroupPython] Cl_element022  label="Cl_element : 011"  # scripted group (container) (typed FeaturePython)
  n = 1
  ref = Cl_element
FEATURE [App::DocumentObjectGroupPython] G4_SILVER_CHLORIDE  # scripted group (container) (typed FeaturePython)
  Dunit = g/cm3
  Dvalue = 5.56
  Group = -> [Ag_element003,Cl_element022]
  conduct = 2
  density = 1
  expand = 3
  formula = G4_SILVER_CHLORIDE
  name = G4_SILVER_CHLORIDE
  specific = 4
FEATURE [App::DocumentObjectGroupPython] Br_element006  label="Br_element : 0.423"  # scripted group (container) (typed FeaturePython)
  n = 0.422895
FEATURE [App::DocumentObjectGroupPython] Ag_element004  label="Ag_element : 0.574"  # scripted group (container) (typed FeaturePython)
  n = 0.573748
FEATURE [App::DocumentObjectGroupPython] I_element007  label="I_element : 0.649"  # scripted group (container) (typed FeaturePython)
  n = 0.003357
FEATURE [App::DocumentObjectGroupPython] G4_SILVER_HALIDES  # scripted group (container) (typed FeaturePython)
  Dunit = g/cm3
  Dvalue = 6.47
  Group = -> [Br_element006,Ag_element004,I_element007]
  conduct = 2
  density = 1
  expand = 3
  formula = G4_SILVER_HALIDES
  name = G4_SILVER_HALIDES
  specific = 4
FEATURE [App::DocumentObjectGroupPython] Ag_element005  label="Ag_element : 003"  # scripted group (container) (typed FeaturePython)
  n = 1
  ref = Ag_element
FEATURE [App::DocumentObjectGroupPython] I_element008  label="I_element : 004"  # scripted group (container) (typed FeaturePython)
  n = 1
  ref = I_element
FEATURE [App::DocumentObjectGroupPython] G4_SILVER_IODIDE  # scripted group (container) (typed FeaturePython)
  Dunit = g/cm3
  Dvalue = 6.01
  Group = -> [Ag_element005,I_element008]
  conduct = 2
  density = 1
  expand = 3
  formula = G4_SILVER_IODIDE
  name = G4_SILVER_IODIDE
  specific = 4
FEATURE [App::DocumentObjectGroupPython] H_element095  label="H_element : 0.100"  # scripted group (container) (typed FeaturePython)
  n = 0.1
FEATURE [App::DocumentObjectGroupPython] C_element103  label="C_element : 0.204"  # scripted group (container) (typed FeaturePython)
  n = 0.204
FEATURE [App::DocumentObjectGroupPython] N_element039  label="N_element : 0.759"  # scripted group (container) (typed FeaturePython)
  n = 0.042
FEATURE [App::DocumentObjectGroupPython] O_element088  label="O_element : 0.645"  # scripted group (container) (typed FeaturePython)
  n = 0.645
FEATURE [App::DocumentObjectGroupPython] Na_element013  label="Na_element : 0.100"  # scripted group (container) (typed FeaturePython)
  n = 0.002
FEATURE [App::DocumentObjectGroupPython] P_element009  label="P_element : 0.107"  # scripted group (container) (typed FeaturePython)
  n = 0.001
FEATURE [App::DocumentObjectGroupPython] S_element020  label="S_element : 0.021"  # scripted group (container) (typed FeaturePython)
  n = 0.002
FEATURE [App::DocumentObjectGroupPython] Cl_element023  label="Cl_element : 0.590"  # scripted group (container) (typed FeaturePython)
  n = 0.003
FEATURE [App::DocumentObjectGroupPython] K_element010  label="K_element : 0.001"  # scripted group (container) (typed FeaturePython)
  n = 0.001
FEATURE [App::DocumentObjectGroupPython] G4_SKIN_ICRP  # scripted group (container) (typed FeaturePython)
  Dunit = g/cm3
  Dvalue = 1.09
  Group = -> [H_element095,C_element103,N_element039,O_element088,Na_element013,P_element009,S_element020,Cl_element023,K_element010]
  conduct = 2
  density = 1
  expand = 3
  formula = G4_SKIN_ICRP
  name = G4_SKIN_ICRP
  specific = 4
FEATURE [App::DocumentObjectGroupPython] Na_element014  label="Na_element : 2"  # scripted group (container) (typed FeaturePython)
  n = 2
  ref = Na_element
FEATURE [App::DocumentObjectGroupPython] C_element104  label="C_element : 058"  # scripted group (container) (typed FeaturePython)
  n = 1
  ref = C_element
FEATURE [App::DocumentObjectGroupPython] O_element089  label="O_element : 049"  # scripted group (container) (typed FeaturePython)
  n = 3
  ref = O_element
FEATURE [App::DocumentObjectGroupPython] G4_SODIUM_CARBONATE  # scripted group (container) (typed FeaturePython)
  Dunit = g/cm3
  Dvalue = 2.532
  Group = -> [Na_element014,C_element104,O_element089]
  conduct = 2
  density = 1
  expand = 3
  formula = G4_SODIUM_CARBONATE
  name = G4_SODIUM_CARBONATE
  specific = 4
FEATURE [App::DocumentObjectGroupPython] Na_element015  label="Na_element : 1"  # scripted group (container) (typed FeaturePython)
  n = 1
  ref = Na_element
FEATURE [App::DocumentObjectGroupPython] I_element009  label="I_element : 005"  # scripted group (container) (typed FeaturePython)
  n = 1
  ref = I_element
FEATURE [App::DocumentObjectGroupPython] G4_SODIUM_IODIDE  # scripted group (container) (typed FeaturePython)
  Dunit = g/cm3
  Dvalue = 3.667
  Group = -> [Na_element015,I_element009]
  conduct = 2
  density = 1
  expand = 3
  formula = G4_SODIUM_IODIDE
  name = G4_SODIUM_IODIDE
  specific = 4
FEATURE [App::DocumentObjectGroupPython] Na_element016  label="Na_element : 003"  # scripted group (container) (typed FeaturePython)
  n = 2
  ref = Na_element
FEATURE [App::DocumentObjectGroupPython] O_element090  label="O_element : 050"  # scripted group (container) (typed FeaturePython)
  n = 1
  ref = O_element
FEATURE [App::DocumentObjectGroupPython] G4_SODIUM_MONOXIDE  # scripted group (container) (typed FeaturePython)
  Dunit = g/cm3
  Dvalue = 2.27
  Group = -> [Na_element016,O_element090]
  conduct = 2
  density = 1
  expand = 3
  formula = G4_SODIUM_MONOXIDE
  name = G4_SODIUM_MONOXIDE
  specific = 4
FEATURE [App::DocumentObjectGroupPython] Na_element017  label="Na_element : 004"  # scripted group (container) (typed FeaturePython)
  n = 1
  ref = Na_element
FEATURE [App::DocumentObjectGroupPython] N_element040  label="N_element : 018"  # scripted group (container) (typed FeaturePython)
  n = 1
  ref = N_element
FEATURE [App::DocumentObjectGroupPython] O_element091  label="O_element : 051"  # scripted group (container) (typed FeaturePython)
  n = 3
  ref = O_element
FEATURE [App::DocumentObjectGroupPython] G4_SODIUM_NITRATE  # scripted group (container) (typed FeaturePython)
  Dunit = g/cm3
  Dvalue = 2.261
  Group = -> [Na_element017,N_element040,O_element091]
  conduct = 2
  density = 1
  expand = 3
  formula = G4_SODIUM_NITRATE
  name = G4_SODIUM_NITRATE
  specific = 4
FEATURE [App::DocumentObjectGroupPython] C_element105  label="C_element : 059"  # scripted group (container) (typed FeaturePython)
  n = 14
  ref = C_element
FEATURE [App::DocumentObjectGroupPython] H_element096  label="H_element : 053"  # scripted group (container) (typed FeaturePython)
  n = 12
  ref = H_element
FEATURE [App::DocumentObjectGroupPython] G4_STILBENE  # scripted group (container) (typed FeaturePython)
  Dunit = g/cm3
  Dvalue = 0.9707
  Group = -> [C_element105,H_element096]
  conduct = 2
  density = 1
  expand = 3
  formula = G4_STILBENE
  name = G4_STILBENE
  specific = 4
FEATURE [App::DocumentObjectGroupPython] C_element106  label="C_element : 12"  # scripted group (container) (typed FeaturePython)
  n = 12
  ref = C_element
FEATURE [App::DocumentObjectGroupPython] H_element097  label="H_element : 22"  # scripted group (container) (typed FeaturePython)
  n = 22
  ref = H_element
FEATURE [App::DocumentObjectGroupPython] O_element092  label="O_element : 11"  # scripted group (container) (typed FeaturePython)
  n = 11
  ref = O_element
FEATURE [App::DocumentObjectGroupPython] G4_SUCROSE  # scripted group (container) (typed FeaturePython)
  Dunit = g/cm3
  Dvalue = 1.5805
  Group = -> [C_element106,H_element097,O_element092]
  conduct = 2
  density = 1
  expand = 3
  formula = G4_SUCROSE
  name = G4_SUCROSE
  specific = 4
FEATURE [App::DocumentObjectGroupPython] C_element107  label="C_element : 18"  # scripted group (container) (typed FeaturePython)
  n = 18
  ref = C_element
FEATURE [App::DocumentObjectGroupPython] H_element098  label="H_element : 054"  # scripted group (container) (typed FeaturePython)
  n = 14
  ref = H_element
FEATURE [App::DocumentObjectGroupPython] G4_TERPHENYL  # scripted group (container) (typed FeaturePython)
  Dunit = g/cm3
  Dvalue = 1.24
  Group = -> [C_element107,H_element098]
  conduct = 2
  density = 1
  expand = 3
  formula = G4_TERPHENYL
  name = G4_TERPHENYL
  specific = 4
FEATURE [App::DocumentObjectGroupPython] H_element099  label="H_element : 0.146"  # scripted group (container) (typed FeaturePython)
  n = 0.106
FEATURE [App::DocumentObjectGroupPython] C_element108  label="C_element : 0.883"  # scripted group (container) (typed FeaturePython)
  n = 0.099
FEATURE [App::DocumentObjectGroupPython] N_element041  label="N_element : 0.020"  # scripted group (container) (typed FeaturePython)
  n = 0.02
FEATURE [App::DocumentObjectGroupPython] O_element093  label="O_element : 0.766"  # scripted group (container) (typed FeaturePython)
  n = 0.766
FEATURE [App::DocumentObjectGroupPython] Na_element018  label="Na_element : 0.101"  # scripted group (container) (typed FeaturePython)
  n = 0.002
FEATURE [App::DocumentObjectGroupPython] P_element010  label="P_element : 0.108"  # scripted group (container) (typed FeaturePython)
  n = 0.001
FEATURE [App::DocumentObjectGroupPython] S_element021  label="S_element : 0.022"  # scripted group (container) (typed FeaturePython)
  n = 0.002
FEATURE [App::DocumentObjectGroupPython] Cl_element024  label="Cl_element : 0.002"  # scripted group (container) (typed FeaturePython)
  n = 0.002
FEATURE [App::DocumentObjectGroupPython] K_element011  label="K_element : 0.017"  # scripted group (container) (typed FeaturePython)
  n = 0.002
FEATURE [App::DocumentObjectGroupPython] G4_TESTIS_ICRP  # scripted group (container) (typed FeaturePython)
  Dunit = g/cm3
  Dvalue = 1.04
  Group = -> [H_element099,C_element108,N_element041,O_element093,Na_element018,P_element010,S_element021,Cl_element024,K_element011]
  conduct = 2
  density = 1
  expand = 3
  formula = G4_TESTIS_ICRP
  name = G4_TESTIS_ICRP
  specific = 4
FEATURE [App::DocumentObjectGroupPython] C_element109  label="C_element : 060"  # scripted group (container) (typed FeaturePython)
  n = 2
  ref = C_element
FEATURE [App::DocumentObjectGroupPython] Cl_element025  label="Cl_element : 012"  # scripted group (container) (typed FeaturePython)
  n = 4
  ref = Cl_element
FEATURE [App::DocumentObjectGroupPython] G4_TETRACHLOROETHYLENE  # scripted group (container) (typed FeaturePython)
  Dunit = g/cm3
  Dvalue = 1.625
  Group = -> [C_element109,Cl_element025]
  conduct = 2
  density = 1
  expand = 3
  formula = G4_TETRACHLOROETHYLENE
  name = G4_TETRACHLOROETHYLENE
  specific = 4
FEATURE [App::DocumentObjectGroupPython] Tl_element001  label="Tl_element : 1"  # scripted group (container) (typed FeaturePython)
  n = 1
  ref = Tl_element
FEATURE [App::DocumentObjectGroupPython] Cl_element026  label="Cl_element : 013"  # scripted group (container) (typed FeaturePython)
  n = 1
  ref = Cl_element
FEATURE [App::DocumentObjectGroupPython] G4_THALLIUM_CHLORIDE  # scripted group (container) (typed FeaturePython)
  Dunit = g/cm3
  Dvalue = 7.004
  Group = -> [Tl_element001,Cl_element026]
  conduct = 2
  density = 1
  expand = 3
  formula = G4_THALLIUM_CHLORIDE
  name = G4_THALLIUM_CHLORIDE
  specific = 4
FEATURE [App::DocumentObjectGroupPython] H_element100  label="H_element : 0.147"  # scripted group (container) (typed FeaturePython)
  n = 0.105
FEATURE [App::DocumentObjectGroupPython] C_element110  label="C_element : 0.256"  # scripted group (container) (typed FeaturePython)
  n = 0.256
FEATURE [App::DocumentObjectGroupPython] N_element042  label="N_element : 0.760"  # scripted group (container) (typed FeaturePython)
  n = 0.027
FEATURE [App::DocumentObjectGroupPython] O_element094  label="O_element : 0.602"  # scripted group (container) (typed FeaturePython)
  n = 0.602
FEATURE [App::DocumentObjectGroupPython] Na_element019  label="Na_element : 0.102"  # scripted group (container) (typed FeaturePython)
  n = 0.001
FEATURE [App::DocumentObjectGroupPython] P_element011  label="P_element : 0.109"  # scripted group (container) (typed FeaturePython)
  n = 0.002
FEATURE [App::DocumentObjectGroupPython] S_element022  label="S_element : 0.023"  # scripted group (container) (typed FeaturePython)
  n = 0.003
FEATURE [App::DocumentObjectGroupPython] Cl_element027  label="Cl_element : 0.591"  # scripted group (container) (typed FeaturePython)
  n = 0.002
FEATURE [App::DocumentObjectGroupPython] K_element012  label="K_element : 0.018"  # scripted group (container) (typed FeaturePython)
  n = 0.002
FEATURE [App::DocumentObjectGroupPython] G4_TISSUE_SOFT_ICRP  # scripted group (container) (typed FeaturePython)
  Dunit = g/cm3
  Dvalue = 1.03
  Group = -> [H_element100,C_element110,N_element042,O_element094,Na_element019,P_element011,S_element022,Cl_element027,K_element012]
  conduct = 2
  density = 1
  expand = 3
  formula = G4_TISSUE_SOFT_ICRP
  name = G4_TISSUE_SOFT_ICRP
  specific = 4
FEATURE [App::DocumentObjectGroupPython] H_element101  label="H_element : 0.148"  # scripted group (container) (typed FeaturePython)
  n = 0.101
FEATURE [App::DocumentObjectGroupPython] C_element111  label="C_element : 0.111"  # scripted group (container) (typed FeaturePython)
  n = 0.111
FEATURE [App::DocumentObjectGroupPython] N_element043  label="N_element : 0.026"  # scripted group (container) (typed FeaturePython)
  n = 0.026
FEATURE [App::DocumentObjectGroupPython] O_element095  label="O_element : 0.762"  # scripted group (container) (typed FeaturePython)
  n = 0.762
FEATURE [App::DocumentObjectGroupPython] G4_TISSUE_SOFT_ICRU_4  label="G4_TISSUE_SOFT_ICRU-4"  # scripted group (container) (typed FeaturePython)
  Dunit = g/cm3
  Dvalue = 1
  Group = -> [H_element101,C_element111,N_element043,O_element095]
  conduct = 2
  density = 1
  expand = 3
  formula = G4_TISSUE_SOFT_ICRU-4
  name = G4_TISSUE_SOFT_ICRU-4
  specific = 4
FEATURE [App::DocumentObjectGroupPython] H_element102  label="H_element : 0.149"  # scripted group (container) (typed FeaturePython)
  n = 0.101869
FEATURE [App::DocumentObjectGroupPython] C_element112  label="C_element : 0.456"  # scripted group (container) (typed FeaturePython)
  n = 0.456179
FEATURE [App::DocumentObjectGroupPython] N_element044  label="N_element : 0.761"  # scripted group (container) (typed FeaturePython)
  n = 0.035172
FEATURE [App::DocumentObjectGroupPython] O_element096  label="O_element : 0.407"  # scripted group (container) (typed FeaturePython)
  n = 0.40678
FEATURE [App::DocumentObjectGroupPython] G4_TISSUE_METHANE  label="G4_TISSUE-METHANE"  # scripted group (container) (typed FeaturePython)
  Dunit = g/cm3
  Dvalue = 0.00106409
  Group = -> [H_element102,C_element112,N_element044,O_element096]
  conduct = 2
  density = 1
  expand = 3
  formula = G4_TISSUE-METHANE
  name = G4_TISSUE-METHANE
  specific = 4
FEATURE [App::DocumentObjectGroupPython] H_element103  label="H_element : 0.103"  # scripted group (container) (typed FeaturePython)
  n = 0.102672
FEATURE [App::DocumentObjectGroupPython] C_element113  label="C_element : 0.569"  # scripted group (container) (typed FeaturePython)
  n = 0.56894
FEATURE [App::DocumentObjectGroupPython] N_element045  label="N_element : 0.762"  # scripted group (container) (typed FeaturePython)
  n = 0.035022
FEATURE [App::DocumentObjectGroupPython] O_element097  label="O_element : 0.293"  # scripted group (container) (typed FeaturePython)
  n = 0.293366
FEATURE [App::DocumentObjectGroupPython] G4_TISSUE_PROPANE  label="G4_TISSUE-PROPANE"  # scripted group (container) (typed FeaturePython)
  Dunit = g/cm3
  Dvalue = 0.00182628
  Group = -> [H_element103,C_element113,N_element045,O_element097]
  conduct = 2
  density = 1
  expand = 3
  formula = G4_TISSUE-PROPANE
  name = G4_TISSUE-PROPANE
  specific = 4
FEATURE [App::DocumentObjectGroupPython] Ti_element003  label="Ti_element : 1"  # scripted group (container) (typed FeaturePython)
  n = 1
  ref = Ti_element
FEATURE [App::DocumentObjectGroupPython] O_element098  label="O_element : 052"  # scripted group (container) (typed FeaturePython)
  n = 2
  ref = O_element
FEATURE [App::DocumentObjectGroupPython] G4_TITANIUM_DIOXIDE  # scripted group (container) (typed FeaturePython)
  Dunit = g/cm3
  Dvalue = 4.26
  Group = -> [Ti_element003,O_element098]
  conduct = 2
  density = 1
  expand = 3
  formula = G4_TITANIUM_DIOXIDE
  name = G4_TITANIUM_DIOXIDE
  specific = 4
FEATURE [App::DocumentObjectGroupPython] C_element114  label="C_element : 061"  # scripted group (container) (typed FeaturePython)
  n = 7
  ref = C_element
FEATURE [App::DocumentObjectGroupPython] H_element104  label="H_element : 055"  # scripted group (container) (typed FeaturePython)
  n = 8
  ref = H_element
FEATURE [App::DocumentObjectGroupPython] G4_TOLUENE  # scripted group (container) (typed FeaturePython)
  Dunit = g/cm3
  Dvalue = 0.8669
  Group = -> [C_element114,H_element104]
  conduct = 2
  density = 1
  expand = 3
  formula = G4_TOLUENE
  name = G4_TOLUENE
  specific = 4
FEATURE [App::DocumentObjectGroupPython] C_element115  label="C_element : 062"  # scripted group (container) (typed FeaturePython)
  n = 2
  ref = C_element
FEATURE [App::DocumentObjectGroupPython] H_element105  label="H_element : 056"  # scripted group (container) (typed FeaturePython)
  n = 1
  ref = H_element
FEATURE [App::DocumentObjectGroupPython] Cl_element028  label="Cl_element : 014"  # scripted group (container) (typed FeaturePython)
  n = 3
  ref = Cl_element
FEATURE [App::DocumentObjectGroupPython] G4_TRICHLOROETHYLENE  # scripted group (container) (typed FeaturePython)
  Dunit = g/cm3
  Dvalue = 1.46
  Group = -> [C_element115,H_element105,Cl_element028]
  conduct = 2
  density = 1
  expand = 3
  formula = G4_TRICHLOROETHYLENE
  name = G4_TRICHLOROETHYLENE
  specific = 4
FEATURE [App::DocumentObjectGroupPython] C_element116  label="C_element : 063"  # scripted group (container) (typed FeaturePython)
  n = 6
  ref = C_element
FEATURE [App::DocumentObjectGroupPython] H_element106  label="H_element : 15"  # scripted group (container) (typed FeaturePython)
  n = 15
  ref = H_element
FEATURE [App::DocumentObjectGroupPython] O_element099  label="O_element : 053"  # scripted group (container) (typed FeaturePython)
  n = 4
  ref = O_element
FEATURE [App::DocumentObjectGroupPython] P_element012  label="P_element : 1"  # scripted group (container) (typed FeaturePython)
  n = 1
  ref = P_element
FEATURE [App::DocumentObjectGroupPython] G4_TRIETHYL_PHOSPHATE  # scripted group (container) (typed FeaturePython)
  Dunit = g/cm3
  Dvalue = 1.07
  Group = -> [C_element116,H_element106,O_element099,P_element012]
  conduct = 2
  density = 1
  expand = 3
  formula = G4_TRIETHYL_PHOSPHATE
  name = G4_TRIETHYL_PHOSPHATE
  specific = 4
FEATURE [App::DocumentObjectGroupPython] W_element003  label="W_element : 003"  # scripted group (container) (typed FeaturePython)
  n = 1
  ref = W_element
FEATURE [App::DocumentObjectGroupPython] F_element017  label="F_element : 6"  # scripted group (container) (typed FeaturePython)
  n = 6
  ref = F_element
FEATURE [App::DocumentObjectGroupPython] G4_TUNGSTEN_HEXAFLUORIDE  # scripted group (container) (typed FeaturePython)
  Dunit = g/cm3
  Dvalue = 2.4
  Group = -> [W_element003,F_element017]
  conduct = 2
  density = 1
  expand = 3
  formula = G4_TUNGSTEN_HEXAFLUORIDE
  name = G4_TUNGSTEN_HEXAFLUORIDE
  specific = 4
FEATURE [App::DocumentObjectGroupPython] U_element001  label="U_element : 1"  # scripted group (container) (typed FeaturePython)
  n = 1
  ref = U_element
FEATURE [App::DocumentObjectGroupPython] C_element117  label="C_element : 064"  # scripted group (container) (typed FeaturePython)
  n = 2
  ref = C_element
FEATURE [App::DocumentObjectGroupPython] G4_URANIUM_DICARBIDE  # scripted group (container) (typed FeaturePython)
  Dunit = g/cm3
  Dvalue = 11.28
  Group = -> [U_element001,C_element117]
  conduct = 2
  density = 1
  expand = 3
  formula = G4_URANIUM_DICARBIDE
  name = G4_URANIUM_DICARBIDE
  specific = 4
FEATURE [App::DocumentObjectGroupPython] U_element002  label="U_element : 002"  # scripted group (container) (typed FeaturePython)
  n = 1
  ref = U_element
FEATURE [App::DocumentObjectGroupPython] C_element118  label="C_element : 065"  # scripted group (container) (typed FeaturePython)
  n = 1
  ref = C_element
FEATURE [App::DocumentObjectGroupPython] G4_URANIUM_MONOCARBIDE  # scripted group (container) (typed FeaturePython)
  Dunit = g/cm3
  Dvalue = 13.63
  Group = -> [U_element002,C_element118]
  conduct = 2
  density = 1
  expand = 3
  formula = G4_URANIUM_MONOCARBIDE
  name = G4_URANIUM_MONOCARBIDE
  specific = 4
FEATURE [App::DocumentObjectGroupPython] U_element003  label="U_element : 003"  # scripted group (container) (typed FeaturePython)
  n = 1
  ref = U_element
FEATURE [App::DocumentObjectGroupPython] O_element100  label="O_element : 054"  # scripted group (container) (typed FeaturePython)
  n = 2
  ref = O_element
FEATURE [App::DocumentObjectGroupPython] G4_URANIUM_OXIDE  # scripted group (container) (typed FeaturePython)
  Dunit = g/cm3
  Dvalue = 10.96
  Group = -> [U_element003,O_element100]
  conduct = 2
  density = 1
  expand = 3
  formula = G4_URANIUM_OXIDE
  name = G4_URANIUM_OXIDE
  specific = 4
FEATURE [App::DocumentObjectGroupPython] C_element119  label="C_element : 066"  # scripted group (container) (typed FeaturePython)
  n = 1
  ref = C_element
FEATURE [App::DocumentObjectGroupPython] H_element107  label="H_element : 057"  # scripted group (container) (typed FeaturePython)
  n = 4
  ref = H_element
FEATURE [App::DocumentObjectGroupPython] N_element046  label="N_element : 019"  # scripted group (container) (typed FeaturePython)
  n = 2
  ref = N_element
FEATURE [App::DocumentObjectGroupPython] O_element101  label="O_element : 055"  # scripted group (container) (typed FeaturePython)
  n = 1
  ref = O_element
FEATURE [App::DocumentObjectGroupPython] G4_UREA  # scripted group (container) (typed FeaturePython)
  Dunit = g/cm3
  Dvalue = 1.323
  Group = -> [C_element119,H_element107,N_element046,O_element101]
  conduct = 2
  density = 1
  expand = 3
  formula = G4_UREA
  name = G4_UREA
  specific = 4
FEATURE [App::DocumentObjectGroupPython] C_element120  label="C_element : 067"  # scripted group (container) (typed FeaturePython)
  n = 5
  ref = C_element
FEATURE [App::DocumentObjectGroupPython] H_element108  label="H_element : 058"  # scripted group (container) (typed FeaturePython)
  n = 11
  ref = H_element
FEATURE [App::DocumentObjectGroupPython] N_element047  label="N_element : 020"  # scripted group (container) (typed FeaturePython)
  n = 1
  ref = N_element
FEATURE [App::DocumentObjectGroupPython] O_element102  label="O_element : 056"  # scripted group (container) (typed FeaturePython)
  n = 2
  ref = O_element
FEATURE [App::DocumentObjectGroupPython] G4_VALINE  # scripted group (container) (typed FeaturePython)
  Dunit = g/cm3
  Dvalue = 1.23
  Group = -> [C_element120,H_element108,N_element047,O_element102]
  conduct = 2
  density = 1
  expand = 3
  formula = G4_VALINE
  name = G4_VALINE
  specific = 4
FEATURE [App::DocumentObjectGroupPython] H_element109  label="H_element : 0.009"  # scripted group (container) (typed FeaturePython)
  n = 0.009417
FEATURE [App::DocumentObjectGroupPython] C_element121  label="C_element : 0.281"  # scripted group (container) (typed FeaturePython)
  n = 0.280555
FEATURE [App::DocumentObjectGroupPython] F_element018  label="F_element : 0.710"  # scripted group (container) (typed FeaturePython)
  n = 0.710028
FEATURE [App::DocumentObjectGroupPython] G4_VITON  # scripted group (container) (typed FeaturePython)
  Dunit = g/cm3
  Dvalue = 1.8
  Group = -> [H_element109,C_element121,F_element018]
  conduct = 2
  density = 1
  expand = 3
  formula = G4_VITON
  name = G4_VITON
  specific = 4
FEATURE [App::DocumentObjectGroupPython] H_element110  label="H_element : 059"  # scripted group (container) (typed FeaturePython)
  n = 2
  ref = H_element
FEATURE [App::DocumentObjectGroupPython] O_element103  label="O_element : 057"  # scripted group (container) (typed FeaturePython)
  n = 1
  ref = O_element
FEATURE [App::DocumentObjectGroupPython] G4_WATER  # scripted group (container) (typed FeaturePython)
  Dunit = g/cm3
  Dvalue = 1
  Group = -> [H_element110,O_element103]
  conduct = 2
  density = 1
  expand = 3
  formula = G4_WATER
  name = G4_WATER
  specific = 4
FEATURE [App::DocumentObjectGroupPython] H_element111  label="H_element : 060"  # scripted group (container) (typed FeaturePython)
  n = 2
  ref = H_element
FEATURE [App::DocumentObjectGroupPython] O_element104  label="O_element : 058"  # scripted group (container) (typed FeaturePython)
  n = 1
  ref = O_element
FEATURE [App::DocumentObjectGroupPython] G4_WATER_VAPOR  # scripted group (container) (typed FeaturePython)
  Dunit = g/cm3
  Dvalue = 0.000756182
  Group = -> [H_element111,O_element104]
  conduct = 2
  density = 1
  expand = 3
  formula = G4_WATER_VAPOR
  name = G4_WATER_VAPOR
  specific = 4
FEATURE [App::DocumentObjectGroupPython] C_element122  label="C_element : 068"  # scripted group (container) (typed FeaturePython)
  n = 8
  ref = C_element
FEATURE [App::DocumentObjectGroupPython] H_element112  label="H_element : 061"  # scripted group (container) (typed FeaturePython)
  n = 10
  ref = H_element
FEATURE [App::DocumentObjectGroupPython] G4_XYLENE  # scripted group (container) (typed FeaturePython)
  Dunit = g/cm3
  Dvalue = 0.87
  Group = -> [C_element122,H_element112]
  conduct = 2
  density = 1
  expand = 3
  formula = G4_XYLENE
  name = G4_XYLENE
  specific = 4
FEATURE [App::DocumentObjectGroupPython] C_element123  label="C_element : 069"  # scripted group (container) (typed FeaturePython)
  n = 1
  ref = C_element
FEATURE [App::DocumentObjectGroupPython] G4_GRAPHITE  # scripted group (container) (typed FeaturePython)
  Dunit = g/cm3
  Dvalue = 2.21
  Group = -> [C_element123]
  conduct = 2
  density = 1
  expand = 3
  formula = G4_GRAPHITE
  name = G4_GRAPHITE
  specific = 4
FEATURE [App::DocumentObjectGroupPython] NIST  # scripted group (container) (typed FeaturePython)
  Group = -> [G4_A_150_TISSUE,G4_ACETONE,G4_ACETYLENE,G4_ADENINE,G4_ADIPOSE_TISSUE_ICRP,G4_AIR,G4_ALANINE,G4_ALUMINUM_OXIDE,G4_AMBER,G4_AMMONIA,G4_ANILINE,G4_ANTHRACENE,G4_B_100_BONE,G4_BAKELITE,G4_BARIUM_FLUORIDE,G4_BARIUM_SULFATE,G4_BENZENE,G4_BERYLLIUM_OXIDE,G4_BGO,G4_BLOOD_ICRP,G4_BONE_COMPACT_ICRU,G4_BONE_CORTICAL_ICRP,G4_BORON_CARBIDE,G4_BORON_OXIDE,G4_BRAIN_ICRP,G4_BUTANE,G4_N_BUTYL_ALCOHOL,G4_C_552,+152 more]
FEATURE [App::DocumentObjectGroupPython] H_element113  label="H_element : 062"  # scripted group (container) (typed FeaturePython)
  n = 1
  ref = H_element
FEATURE [App::DocumentObjectGroupPython] G4_H  # scripted group (container) (typed FeaturePython)
  Dunit = g/cm3
  Dvalue = 8.3748e-05
  Group = -> [H_element113]
  conduct = 2
  density = 1
  expand = 3
  formula = H
  name = G4_H
  specific = 4
FEATURE [App::DocumentObjectGroupPython] He_element001  label="He_element : 1"  # scripted group (container) (typed FeaturePython)
  n = 1
  ref = He_element
FEATURE [App::DocumentObjectGroupPython] G4_He  # scripted group (container) (typed FeaturePython)
  Dunit = g/cm3
  Dvalue = 0.000166322
  Group = -> [He_element001]
  conduct = 2
  density = 1
  expand = 3
  formula = He
  name = G4_He
  specific = 4
FEATURE [App::DocumentObjectGroupPython] Li_element008  label="Li_element : 008"  # scripted group (container) (typed FeaturePython)
  n = 1
  ref = Li_element
FEATURE [App::DocumentObjectGroupPython] G4_Li  # scripted group (container) (typed FeaturePython)
  Dunit = g/cm3
  Dvalue = 0.534
  Group = -> [Li_element008]
  conduct = 2
  density = 1
  expand = 3
  formula = Li
  name = G4_Li
  specific = 4
FEATURE [App::DocumentObjectGroupPython] Be_element002  label="Be_element : 002"  # scripted group (container) (typed FeaturePython)
  n = 1
  ref = Be_element
FEATURE [App::DocumentObjectGroupPython] G4_Be  # scripted group (container) (typed FeaturePython)
  Dunit = g/cm3
  Dvalue = 1.848
  Group = -> [Be_element002]
  conduct = 2
  density = 1
  expand = 3
  formula = Be
  name = G4_Be
  specific = 4
FEATURE [App::DocumentObjectGroupPython] B_element007  label="B_element : 007"  # scripted group (container) (typed FeaturePython)
  n = 1
  ref = B_element
FEATURE [App::DocumentObjectGroupPython] G4_B  # scripted group (container) (typed FeaturePython)
  Dunit = g/cm3
  Dvalue = 2.37
  Group = -> [B_element007]
  conduct = 2
  density = 1
  expand = 3
  formula = B
  name = G4_B
  specific = 4
FEATURE [App::DocumentObjectGroupPython] C_element124  label="C_element : 070"  # scripted group (container) (typed FeaturePython)
  n = 1
  ref = C_element
FEATURE [App::DocumentObjectGroupPython] G4_C  # scripted group (container) (typed FeaturePython)
  Dunit = g/cm3
  Dvalue = 2
  Group = -> [C_element124]
  conduct = 2
  density = 1
  expand = 3
  formula = C
  name = G4_C
  specific = 4
FEATURE [App::DocumentObjectGroupPython] N_element048  label="N_element : 021"  # scripted group (container) (typed FeaturePython)
  n = 1
  ref = N_element
FEATURE [App::DocumentObjectGroupPython] G4_N  # scripted group (container) (typed FeaturePython)
  Dunit = g/cm3
  Dvalue = 0.0011652
  Group = -> [N_element048]
  conduct = 2
  density = 1
  expand = 3
  formula = N
  name = G4_N
  specific = 4
FEATURE [App::DocumentObjectGroupPython] O_element105  label="O_element : 059"  # scripted group (container) (typed FeaturePython)
  n = 1
  ref = O_element
FEATURE [App::DocumentObjectGroupPython] G4_O  # scripted group (container) (typed FeaturePython)
  Dunit = g/cm3
  Dvalue = 0.00133151
  Group = -> [O_element105]
  conduct = 2
  density = 1
  expand = 3
  formula = O
  name = G4_O
  specific = 4
FEATURE [App::DocumentObjectGroupPython] F_element019  label="F_element : 008"  # scripted group (container) (typed FeaturePython)
  n = 1
  ref = F_element
FEATURE [App::DocumentObjectGroupPython] G4_F  # scripted group (container) (typed FeaturePython)
  Dunit = g/cm3
  Dvalue = 0.00158029
  Group = -> [F_element019]
  conduct = 2
  density = 1
  expand = 3
  formula = F
  name = G4_F
  specific = 4
FEATURE [App::DocumentObjectGroupPython] Ne_element001  label="Ne_element : 1"  # scripted group (container) (typed FeaturePython)
  n = 1
  ref = Ne_element
FEATURE [App::DocumentObjectGroupPython] G4_Ne  # scripted group (container) (typed FeaturePython)
  Dunit = g/cm3
  Dvalue = 0.000838505
  Group = -> [Ne_element001]
  conduct = 2
  density = 1
  expand = 3
  formula = Ne
  name = G4_Ne
  specific = 4
FEATURE [App::DocumentObjectGroupPython] Na_element020  label="Na_element : 005"  # scripted group (container) (typed FeaturePython)
  n = 1
  ref = Na_element
FEATURE [App::DocumentObjectGroupPython] G4_Na  # scripted group (container) (typed FeaturePython)
  Dunit = g/cm3
  Dvalue = 0.971
  Group = -> [Na_element020]
  conduct = 2
  density = 1
  expand = 3
  formula = Na
  name = G4_Na
  specific = 4
FEATURE [App::DocumentObjectGroupPython] Mg_element011  label="Mg_element : 005"  # scripted group (container) (typed FeaturePython)
  n = 1
  ref = Mg_element
FEATURE [App::DocumentObjectGroupPython] G4_Mg  # scripted group (container) (typed FeaturePython)
  Dunit = g/cm3
  Dvalue = 1.74
  Group = -> [Mg_element011]
  conduct = 2
  density = 1
  expand = 3
  formula = Mg
  name = G4_Mg
  specific = 4
FEATURE [App::DocumentObjectGroupPython] Al_element004  label="Al_element : 1"  # scripted group (container) (typed FeaturePython)
  n = 1
  ref = Al_element
FEATURE [App::DocumentObjectGroupPython] G4_Al  # scripted group (container) (typed FeaturePython)
  Dunit = g/cm3
  Dvalue = 2.699
  Group = -> [Al_element004]
  conduct = 2
  density = 1
  expand = 3
  formula = Al
  name = G4_Al
  specific = 4
FEATURE [App::DocumentObjectGroupPython] Si_element007  label="Si_element : 002"  # scripted group (container) (typed FeaturePython)
  n = 1
  ref = Si_element
FEATURE [App::DocumentObjectGroupPython] G4_Si  # scripted group (container) (typed FeaturePython)
  Dunit = g/cm3
  Dvalue = 2.33
  Group = -> [Si_element007]
  conduct = 2
  density = 1
  expand = 3
  formula = Si
  name = G4_Si
  specific = 4
FEATURE [App::DocumentObjectGroupPython] P_element013  label="P_element : 002"  # scripted group (container) (typed FeaturePython)
  n = 1
  ref = P_element
FEATURE [App::DocumentObjectGroupPython] G4_P  # scripted group (container) (typed FeaturePython)
  Dunit = g/cm3
  Dvalue = 2.2
  Group = -> [P_element013]
  conduct = 2
  density = 1
  expand = 3
  formula = P
  name = G4_P
  specific = 4
FEATURE [App::DocumentObjectGroupPython] S_element023  label="S_element : 007"  # scripted group (container) (typed FeaturePython)
  n = 1
  ref = S_element
FEATURE [App::DocumentObjectGroupPython] G4_S  # scripted group (container) (typed FeaturePython)
  Dunit = g/cm3
  Dvalue = 2
  Group = -> [S_element023]
  conduct = 2
  density = 1
  expand = 3
  formula = S
  name = G4_S
  specific = 4
FEATURE [App::DocumentObjectGroupPython] Cl_element029  label="Cl_element : 015"  # scripted group (container) (typed FeaturePython)
  n = 1
  ref = Cl_element
FEATURE [App::DocumentObjectGroupPython] G4_Cl  # scripted group (container) (typed FeaturePython)
  Dunit = g/cm3
  Dvalue = 0.00299473
  Group = -> [Cl_element029]
  conduct = 2
  density = 1
  expand = 3
  formula = Cl
  name = G4_Cl
  specific = 4
FEATURE [App::DocumentObjectGroupPython] Ar_element002  label="Ar_element : 1"  # scripted group (container) (typed FeaturePython)
  n = 1
  ref = Ar_element
FEATURE [App::DocumentObjectGroupPython] G4_Ar  # scripted group (container) (typed FeaturePython)
  Dunit = g/cm3
  Dvalue = 0.00166201
  Group = -> [Ar_element002]
  conduct = 2
  density = 1
  expand = 3
  formula = Ar
  name = G4_Ar
  specific = 4
FEATURE [App::DocumentObjectGroupPython] K_element013  label="K_element : 003"  # scripted group (container) (typed FeaturePython)
  n = 1
  ref = K_element
FEATURE [App::DocumentObjectGroupPython] G4_K  # scripted group (container) (typed FeaturePython)
  Dunit = g/cm3
  Dvalue = 0.862
  Group = -> [K_element013]
  conduct = 2
  density = 1
  expand = 3
  formula = K
  name = G4_K
  specific = 4
FEATURE [App::DocumentObjectGroupPython] Ca_element014  label="Ca_element : 007"  # scripted group (container) (typed FeaturePython)
  n = 1
  ref = Ca_element
FEATURE [App::DocumentObjectGroupPython] G4_Ca  # scripted group (container) (typed FeaturePython)
  Dunit = g/cm3
  Dvalue = 1.55
  Group = -> [Ca_element014]
  conduct = 2
  density = 1
  expand = 3
  formula = Ca
  name = G4_Ca
  specific = 4
FEATURE [App::DocumentObjectGroupPython] Sc_element001  label="Sc_element : 1"  # scripted group (container) (typed FeaturePython)
  n = 1
  ref = Sc_element
FEATURE [App::DocumentObjectGroupPython] G4_Sc  # scripted group (container) (typed FeaturePython)
  Dunit = g/cm3
  Dvalue = 2.989
  Group = -> [Sc_element001]
  conduct = 2
  density = 1
  expand = 3
  formula = Sc
  name = G4_Sc
  specific = 4
FEATURE [App::DocumentObjectGroupPython] Ti_element004  label="Ti_element : 002"  # scripted group (container) (typed FeaturePython)
  n = 1
  ref = Ti_element
FEATURE [App::DocumentObjectGroupPython] G4_Ti  # scripted group (container) (typed FeaturePython)
  Dunit = g/cm3
  Dvalue = 4.54
  Group = -> [Ti_element004]
  conduct = 2
  density = 1
  expand = 3
  formula = Ti
  name = G4_Ti
  specific = 4
FEATURE [App::DocumentObjectGroupPython] V_element001  label="V_element : 1"  # scripted group (container) (typed FeaturePython)
  n = 1
  ref = V_element
FEATURE [App::DocumentObjectGroupPython] G4_V  # scripted group (container) (typed FeaturePython)
  Dunit = g/cm3
  Dvalue = 6.11
  Group = -> [V_element001]
  conduct = 2
  density = 1
  expand = 3
  formula = V
  name = G4_V
  specific = 4
FEATURE [App::DocumentObjectGroupPython] Cr_element001  label="Cr_element : 1"  # scripted group (container) (typed FeaturePython)
  n = 1
  ref = Cr_element
FEATURE [App::DocumentObjectGroupPython] G4_Cr  # scripted group (container) (typed FeaturePython)
  Dunit = g/cm3
  Dvalue = 7.18
  Group = -> [Cr_element001]
  conduct = 2
  density = 1
  expand = 3
  formula = Cr
  name = G4_Cr
  specific = 4
FEATURE [App::DocumentObjectGroupPython] Mn_element001  label="Mn_element : 1"  # scripted group (container) (typed FeaturePython)
  n = 1
  ref = Mn_element
FEATURE [App::DocumentObjectGroupPython] G4_Mn  # scripted group (container) (typed FeaturePython)
  Dunit = g/cm3
  Dvalue = 7.44
  Group = -> [Mn_element001]
  conduct = 2
  density = 1
  expand = 3
  formula = Mn
  name = G4_Mn
  specific = 4
FEATURE [App::DocumentObjectGroupPython] Fe_element007  label="Fe_element : 004"  # scripted group (container) (typed FeaturePython)
  n = 1
  ref = Fe_element
FEATURE [App::DocumentObjectGroupPython] G4_Fe  # scripted group (container) (typed FeaturePython)
  Dunit = g/cm3
  Dvalue = 7.874
  Group = -> [Fe_element007]
  conduct = 2
  density = 1
  expand = 3
  formula = Fe
  name = G4_Fe
  specific = 4
FEATURE [App::DocumentObjectGroupPython] Co_element001  label="Co_element : 1"  # scripted group (container) (typed FeaturePython)
  n = 1
  ref = Co_element
FEATURE [App::DocumentObjectGroupPython] G4_Co  # scripted group (container) (typed FeaturePython)
  Dunit = g/cm3
  Dvalue = 8.9
  Group = -> [Co_element001]
  conduct = 2
  density = 1
  expand = 3
  formula = Co
  name = G4_Co
  specific = 4
FEATURE [App::DocumentObjectGroupPython] Ni_element001  label="Ni_element : 1"  # scripted group (container) (typed FeaturePython)
  n = 1
  ref = Ni_element
FEATURE [App::DocumentObjectGroupPython] G4_Ni  # scripted group (container) (typed FeaturePython)
  Dunit = g/cm3
  Dvalue = 8.902
  Group = -> [Ni_element001]
  conduct = 2
  density = 1
  expand = 3
  formula = Ni
  name = G4_Ni
  specific = 4
FEATURE [App::DocumentObjectGroupPython] Cu_element001  label="Cu_element : 1"  # scripted group (container) (typed FeaturePython)
  n = 1
  ref = Cu_element
FEATURE [App::DocumentObjectGroupPython] G4_Cu  # scripted group (container) (typed FeaturePython)
  Dunit = g/cm3
  Dvalue = 8.96
  Group = -> [Cu_element001]
  conduct = 2
  density = 1
  expand = 3
  formula = Cu
  name = G4_Cu
  specific = 4
FEATURE [App::DocumentObjectGroupPython] Zn_element001  label="Zn_element : 1"  # scripted group (container) (typed FeaturePython)
  n = 1
  ref = Zn_element
FEATURE [App::DocumentObjectGroupPython] G4_Zn  # scripted group (container) (typed FeaturePython)
  Dunit = g/cm3
  Dvalue = 7.133
  Group = -> [Zn_element001]
  conduct = 2
  density = 1
  expand = 3
  formula = Zn
  name = G4_Zn
  specific = 4
FEATURE [App::DocumentObjectGroupPython] Ga_element002  label="Ga_element : 002"  # scripted group (container) (typed FeaturePython)
  n = 1
  ref = Ga_element
FEATURE [App::DocumentObjectGroupPython] G4_Ga  # scripted group (container) (typed FeaturePython)
  Dunit = g/cm3
  Dvalue = 5.904
  Group = -> [Ga_element002]
  conduct = 2
  density = 1
  expand = 3
  formula = Ga
  name = G4_Ga
  specific = 4
FEATURE [App::DocumentObjectGroupPython] Ge_element002  label="Ge_element : 1"  # scripted group (container) (typed FeaturePython)
  n = 1
  ref = Ge_element
FEATURE [App::DocumentObjectGroupPython] G4_Ge  # scripted group (container) (typed FeaturePython)
  Dunit = g/cm3
  Dvalue = 5.323
  Group = -> [Ge_element002]
  conduct = 2
  density = 1
  expand = 3
  formula = Ge
  name = G4_Ge
  specific = 4
FEATURE [App::DocumentObjectGroupPython] As_element003  label="As_element : 002"  # scripted group (container) (typed FeaturePython)
  n = 1
  ref = As_element
FEATURE [App::DocumentObjectGroupPython] G4_As  # scripted group (container) (typed FeaturePython)
  Dunit = g/cm3
  Dvalue = 5.73
  Group = -> [As_element003]
  conduct = 2
  density = 1
  expand = 3
  formula = As
  name = G4_As
  specific = 4
FEATURE [App::DocumentObjectGroupPython] Se_element001  label="Se_element : 1"  # scripted group (container) (typed FeaturePython)
  n = 1
  ref = Se_element
FEATURE [App::DocumentObjectGroupPython] G4_Se  # scripted group (container) (typed FeaturePython)
  Dunit = g/cm3
  Dvalue = 4.5
  Group = -> [Se_element001]
  conduct = 2
  density = 1
  expand = 3
  formula = Se
  name = G4_Se
  specific = 4
FEATURE [App::DocumentObjectGroupPython] Br_element007  label="Br_element : 004"  # scripted group (container) (typed FeaturePython)
  n = 1
  ref = Br_element
FEATURE [App::DocumentObjectGroupPython] G4_Br  # scripted group (container) (typed FeaturePython)
  Dunit = g/cm3
  Dvalue = 0.0070721
  Group = -> [Br_element007]
  conduct = 2
  density = 1
  expand = 3
  formula = Br
  name = G4_Br
  specific = 4
FEATURE [App::DocumentObjectGroupPython] Kr_element001  label="Kr_element : 1"  # scripted group (container) (typed FeaturePython)
  n = 1
  ref = Kr_element
FEATURE [App::DocumentObjectGroupPython] G4_Kr  # scripted group (container) (typed FeaturePython)
  Dunit = g/cm3
  Dvalue = 0.00347832
  Group = -> [Kr_element001]
  conduct = 2
  density = 1
  expand = 3
  formula = Kr
  name = G4_Kr
  specific = 4
FEATURE [App::DocumentObjectGroupPython] Rb_element001  label="Rb_element : 1"  # scripted group (container) (typed FeaturePython)
  n = 1
  ref = Rb_element
FEATURE [App::DocumentObjectGroupPython] G4_Rb  # scripted group (container) (typed FeaturePython)
  Dunit = g/cm3
  Dvalue = 1.532
  Group = -> [Rb_element001]
  conduct = 2
  density = 1
  expand = 3
  formula = Rb
  name = G4_Rb
  specific = 4
FEATURE [App::DocumentObjectGroupPython] Sr_element001  label="Sr_element : 1"  # scripted group (container) (typed FeaturePython)
  n = 1
  ref = Sr_element
FEATURE [App::DocumentObjectGroupPython] G4_Sr  # scripted group (container) (typed FeaturePython)
  Dunit = g/cm3
  Dvalue = 2.54
  Group = -> [Sr_element001]
  conduct = 2
  density = 1
  expand = 3
  formula = Sr
  name = G4_Sr
  specific = 4
FEATURE [App::DocumentObjectGroupPython] Y_element001  label="Y_element : 1"  # scripted group (container) (typed FeaturePython)
  n = 1
  ref = Y_element
FEATURE [App::DocumentObjectGroupPython] G4_Y  # scripted group (container) (typed FeaturePython)
  Dunit = g/cm3
  Dvalue = 4.469
  Group = -> [Y_element001]
  conduct = 2
  density = 1
  expand = 3
  formula = Y
  name = G4_Y
  specific = 4
FEATURE [App::DocumentObjectGroupPython] Zr_element001  label="Zr_element : 1"  # scripted group (container) (typed FeaturePython)
  n = 1
  ref = Zr_element
FEATURE [App::DocumentObjectGroupPython] G4_Zr  # scripted group (container) (typed FeaturePython)
  Dunit = g/cm3
  Dvalue = 6.506
  Group = -> [Zr_element001]
  conduct = 2
  density = 1
  expand = 3
  formula = Zr
  name = G4_Zr
  specific = 4
FEATURE [App::DocumentObjectGroupPython] Nb_element001  label="Nb_element : 1"  # scripted group (container) (typed FeaturePython)
  n = 1
  ref = Nb_element
FEATURE [App::DocumentObjectGroupPython] G4_Nb  # scripted group (container) (typed FeaturePython)
  Dunit = g/cm3
  Dvalue = 8.57
  Group = -> [Nb_element001]
  conduct = 2
  density = 1
  expand = 3
  formula = Nb
  name = G4_Nb
  specific = 4
FEATURE [App::DocumentObjectGroupPython] Mo_element001  label="Mo_element : 1"  # scripted group (container) (typed FeaturePython)
  n = 1
  ref = Mo_element
FEATURE [App::DocumentObjectGroupPython] G4_Mo  # scripted group (container) (typed FeaturePython)
  Dunit = g/cm3
  Dvalue = 10.22
  Group = -> [Mo_element001]
  conduct = 2
  density = 1
  expand = 3
  formula = Mo
  name = G4_Mo
  specific = 4
FEATURE [App::DocumentObjectGroupPython] Tc_element001  label="Tc_element : 1"  # scripted group (container) (typed FeaturePython)
  n = 1
  ref = Tc_element
FEATURE [App::DocumentObjectGroupPython] G4_Tc  # scripted group (container) (typed FeaturePython)
  Dunit = g/cm3
  Dvalue = 11.5
  Group = -> [Tc_element001]
  conduct = 2
  density = 1
  expand = 3
  formula = Tc
  name = G4_Tc
  specific = 4
FEATURE [App::DocumentObjectGroupPython] Ru_element001  label="Ru_element : 1"  # scripted group (container) (typed FeaturePython)
  n = 1
  ref = Ru_element
FEATURE [App::DocumentObjectGroupPython] G4_Ru  # scripted group (container) (typed FeaturePython)
  Dunit = g/cm3
  Dvalue = 12.41
  Group = -> [Ru_element001]
  conduct = 2
  density = 1
  expand = 3
  formula = Ru
  name = G4_Ru
  specific = 4
FEATURE [App::DocumentObjectGroupPython] Rh_element001  label="Rh_element : 1"  # scripted group (container) (typed FeaturePython)
  n = 1
  ref = Rh_element
FEATURE [App::DocumentObjectGroupPython] G4_Rh  # scripted group (container) (typed FeaturePython)
  Dunit = g/cm3
  Dvalue = 12.41
  Group = -> [Rh_element001]
  conduct = 2
  density = 1
  expand = 3
  formula = Rh
  name = G4_Rh
  specific = 4
FEATURE [App::DocumentObjectGroupPython] Pd_element001  label="Pd_element : 1"  # scripted group (container) (typed FeaturePython)
  n = 1
  ref = Pd_element
FEATURE [App::DocumentObjectGroupPython] G4_Pd  # scripted group (container) (typed FeaturePython)
  Dunit = g/cm3
  Dvalue = 12.02
  Group = -> [Pd_element001]
  conduct = 2
  density = 1
  expand = 3
  formula = Pd
  name = G4_Pd
  specific = 4
FEATURE [App::DocumentObjectGroupPython] Ag_element006  label="Ag_element : 004"  # scripted group (container) (typed FeaturePython)
  n = 1
  ref = Ag_element
FEATURE [App::DocumentObjectGroupPython] G4_Ag  # scripted group (container) (typed FeaturePython)
  Dunit = g/cm3
  Dvalue = 10.5
  Group = -> [Ag_element006]
  conduct = 2
  density = 1
  expand = 3
  formula = Ag
  name = G4_Ag
  specific = 4
FEATURE [App::DocumentObjectGroupPython] Cd_element003  label="Cd_element : 003"  # scripted group (container) (typed FeaturePython)
  n = 1
  ref = Cd_element
FEATURE [App::DocumentObjectGroupPython] G4_Cd  # scripted group (container) (typed FeaturePython)
  Dunit = g/cm3
  Dvalue = 8.65
  Group = -> [Cd_element003]
  conduct = 2
  density = 1
  expand = 3
  formula = Cd
  name = G4_Cd
  specific = 4
FEATURE [App::DocumentObjectGroupPython] In_element001  label="In_element : 1"  # scripted group (container) (typed FeaturePython)
  n = 1
  ref = In_element
FEATURE [App::DocumentObjectGroupPython] G4_In  # scripted group (container) (typed FeaturePython)
  Dunit = g/cm3
  Dvalue = 7.31
  Group = -> [In_element001]
  conduct = 2
  density = 1
  expand = 3
  formula = In
  name = G4_In
  specific = 4
FEATURE [App::DocumentObjectGroupPython] Sn_element001  label="Sn_element : 1"  # scripted group (container) (typed FeaturePython)
  n = 1
  ref = Sn_element
FEATURE [App::DocumentObjectGroupPython] G4_Sn  # scripted group (container) (typed FeaturePython)
  Dunit = g/cm3
  Dvalue = 7.31
  Group = -> [Sn_element001]
  conduct = 2
  density = 1
  expand = 3
  formula = Sn
  name = G4_Sn
  specific = 4
FEATURE [App::DocumentObjectGroupPython] Sb_element001  label="Sb_element : 1"  # scripted group (container) (typed FeaturePython)
  n = 1
  ref = Sb_element
FEATURE [App::DocumentObjectGroupPython] G4_Sb  # scripted group (container) (typed FeaturePython)
  Dunit = g/cm3
  Dvalue = 6.691
  Group = -> [Sb_element001]
  conduct = 2
  density = 1
  expand = 3
  formula = Sb
  name = G4_Sb
  specific = 4
FEATURE [App::DocumentObjectGroupPython] Te_element002  label="Te_element : 002"  # scripted group (container) (typed FeaturePython)
  n = 1
  ref = Te_element
FEATURE [App::DocumentObjectGroupPython] G4_Te  # scripted group (container) (typed FeaturePython)
  Dunit = g/cm3
  Dvalue = 6.24
  Group = -> [Te_element002]
  conduct = 2
  density = 1
  expand = 3
  formula = Te
  name = G4_Te
  specific = 4
FEATURE [App::DocumentObjectGroupPython] I_element010  label="I_element : 006"  # scripted group (container) (typed FeaturePython)
  n = 1
  ref = I_element
FEATURE [App::DocumentObjectGroupPython] G4_I  # scripted group (container) (typed FeaturePython)
  Dunit = g/cm3
  Dvalue = 4.93
  Group = -> [I_element010]
  conduct = 2
  density = 1
  expand = 3
  formula = I
  name = G4_I
  specific = 4
FEATURE [App::DocumentObjectGroupPython] Xe_element001  label="Xe_element : 1"  # scripted group (container) (typed FeaturePython)
  n = 1
  ref = Xe_element
FEATURE [App::DocumentObjectGroupPython] G4_Xe  # scripted group (container) (typed FeaturePython)
  Dunit = g/cm3
  Dvalue = 0.00548536
  Group = -> [Xe_element001]
  conduct = 2
  density = 1
  expand = 3
  formula = Xe
  name = G4_Xe
  specific = 4
FEATURE [App::DocumentObjectGroupPython] Cs_element003  label="Cs_element : 003"  # scripted group (container) (typed FeaturePython)
  n = 1
  ref = Cs_element
FEATURE [App::DocumentObjectGroupPython] G4_Cs  # scripted group (container) (typed FeaturePython)
  Dunit = g/cm3
  Dvalue = 1.873
  Group = -> [Cs_element003]
  conduct = 2
  density = 1
  expand = 3
  formula = Cs
  name = G4_Cs
  specific = 4
FEATURE [App::DocumentObjectGroupPython] Ba_element003  label="Ba_element : 003"  # scripted group (container) (typed FeaturePython)
  n = 1
  ref = Ba_element
FEATURE [App::DocumentObjectGroupPython] G4_Ba  # scripted group (container) (typed FeaturePython)
  Dunit = g/cm3
  Dvalue = 3.5
  Group = -> [Ba_element003]
  conduct = 2
  density = 1
  expand = 3
  formula = Ba
  name = G4_Ba
  specific = 4
FEATURE [App::DocumentObjectGroupPython] La_element003  label="La_element : 003"  # scripted group (container) (typed FeaturePython)
  n = 1
  ref = La_element
FEATURE [App::DocumentObjectGroupPython] G4_La  # scripted group (container) (typed FeaturePython)
  Dunit = g/cm3
  Dvalue = 6.154
  Group = -> [La_element003]
  conduct = 2
  density = 1
  expand = 3
  formula = La
  name = G4_La
  specific = 4
FEATURE [App::DocumentObjectGroupPython] Ce_element002  label="Ce_element : 1"  # scripted group (container) (typed FeaturePython)
  n = 1
  ref = Ce_element
FEATURE [App::DocumentObjectGroupPython] G4_Ce  # scripted group (container) (typed FeaturePython)
  Dunit = g/cm3
  Dvalue = 6.657
  Group = -> [Ce_element002]
  conduct = 2
  density = 1
  expand = 3
  formula = Ce
  name = G4_Ce
  specific = 4
FEATURE [App::DocumentObjectGroupPython] Pr_element001  label="Pr_element : 1"  # scripted group (container) (typed FeaturePython)
  n = 1
  ref = Pr_element
FEATURE [App::DocumentObjectGroupPython] G4_Pr  # scripted group (container) (typed FeaturePython)
  Dunit = g/cm3
  Dvalue = 6.71
  Group = -> [Pr_element001]
  conduct = 2
  density = 1
  expand = 3
  formula = Pr
  name = G4_Pr
  specific = 4
FEATURE [App::DocumentObjectGroupPython] Nd_element001  label="Nd_element : 1"  # scripted group (container) (typed FeaturePython)
  n = 1
  ref = Nd_element
FEATURE [App::DocumentObjectGroupPython] G4_Nd  # scripted group (container) (typed FeaturePython)
  Dunit = g/cm3
  Dvalue = 6.9
  Group = -> [Nd_element001]
  conduct = 2
  density = 1
  expand = 3
  formula = Nd
  name = G4_Nd
  specific = 4
FEATURE [App::DocumentObjectGroupPython] Pm_element001  label="Pm_element : 1"  # scripted group (container) (typed FeaturePython)
  n = 1
  ref = Pm_element
FEATURE [App::DocumentObjectGroupPython] G4_Pm  # scripted group (container) (typed FeaturePython)
  Dunit = g/cm3
  Dvalue = 7.22
  Group = -> [Pm_element001]
  conduct = 2
  density = 1
  expand = 3
  formula = Pm
  name = G4_Pm
  specific = 4
FEATURE [App::DocumentObjectGroupPython] Sm_element001  label="Sm_element : 1"  # scripted group (container) (typed FeaturePython)
  n = 1
  ref = Sm_element
FEATURE [App::DocumentObjectGroupPython] G4_Sm  # scripted group (container) (typed FeaturePython)
  Dunit = g/cm3
  Dvalue = 7.46
  Group = -> [Sm_element001]
  conduct = 2
  density = 1
  expand = 3
  formula = Sm
  name = G4_Sm
  specific = 4
FEATURE [App::DocumentObjectGroupPython] Eu_element001  label="Eu_element : 1"  # scripted group (container) (typed FeaturePython)
  n = 1
  ref = Eu_element
FEATURE [App::DocumentObjectGroupPython] G4_Eu  # scripted group (container) (typed FeaturePython)
  Dunit = g/cm3
  Dvalue = 5.243
  Group = -> [Eu_element001]
  conduct = 2
  density = 1
  expand = 3
  formula = Eu
  name = G4_Eu
  specific = 4
FEATURE [App::DocumentObjectGroupPython] Gd_element002  label="Gd_element : 1"  # scripted group (container) (typed FeaturePython)
  n = 1
  ref = Gd_element
FEATURE [App::DocumentObjectGroupPython] G4_Gd  # scripted group (container) (typed FeaturePython)
  Dunit = g/cm3
  Dvalue = 7.9004
  Group = -> [Gd_element002]
  conduct = 2
  density = 1
  expand = 3
  formula = Gd
  name = G4_Gd
  specific = 4
FEATURE [App::DocumentObjectGroupPython] Tb_element001  label="Tb_element : 1"  # scripted group (container) (typed FeaturePython)
  n = 1
  ref = Tb_element
FEATURE [App::DocumentObjectGroupPython] G4_Tb  # scripted group (container) (typed FeaturePython)
  Dunit = g/cm3
  Dvalue = 8.229
  Group = -> [Tb_element001]
  conduct = 2
  density = 1
  expand = 3
  formula = Tb
  name = G4_Tb
  specific = 4
FEATURE [App::DocumentObjectGroupPython] Dy_element001  label="Dy_element : 1"  # scripted group (container) (typed FeaturePython)
  n = 1
  ref = Dy_element
FEATURE [App::DocumentObjectGroupPython] G4_Dy  # scripted group (container) (typed FeaturePython)
  Dunit = g/cm3
  Dvalue = 8.55
  Group = -> [Dy_element001]
  conduct = 2
  density = 1
  expand = 3
  formula = Dy
  name = G4_Dy
  specific = 4
FEATURE [App::DocumentObjectGroupPython] Ho_element001  label="Ho_element : 1"  # scripted group (container) (typed FeaturePython)
  n = 1
  ref = Ho_element
FEATURE [App::DocumentObjectGroupPython] G4_Ho  # scripted group (container) (typed FeaturePython)
  Dunit = g/cm3
  Dvalue = 8.795
  Group = -> [Ho_element001]
  conduct = 2
  density = 1
  expand = 3
  formula = Ho
  name = G4_Ho
  specific = 4
FEATURE [App::DocumentObjectGroupPython] Er_element001  label="Er_element : 1"  # scripted group (container) (typed FeaturePython)
  n = 1
  ref = Er_element
FEATURE [App::DocumentObjectGroupPython] G4_Er  # scripted group (container) (typed FeaturePython)
  Dunit = g/cm3
  Dvalue = 9.066
  Group = -> [Er_element001]
  conduct = 2
  density = 1
  expand = 3
  formula = Er
  name = G4_Er
  specific = 4
FEATURE [App::DocumentObjectGroupPython] Tm_element001  label="Tm_element : 1"  # scripted group (container) (typed FeaturePython)
  n = 1
  ref = Tm_element
FEATURE [App::DocumentObjectGroupPython] G4_Tm  # scripted group (container) (typed FeaturePython)
  Dunit = g/cm3
  Dvalue = 9.321
  Group = -> [Tm_element001]
  conduct = 2
  density = 1
  expand = 3
  formula = Tm
  name = G4_Tm
  specific = 4
FEATURE [App::DocumentObjectGroupPython] Yb_element001  label="Yb_element : 1"  # scripted group (container) (typed FeaturePython)
  n = 1
  ref = Yb_element
FEATURE [App::DocumentObjectGroupPython] G4_Yb  # scripted group (container) (typed FeaturePython)
  Dunit = g/cm3
  Dvalue = 6.73
  Group = -> [Yb_element001]
  conduct = 2
  density = 1
  expand = 3
  formula = Yb
  name = G4_Yb
  specific = 4
FEATURE [App::DocumentObjectGroupPython] Lu_element001  label="Lu_element : 1"  # scripted group (container) (typed FeaturePython)
  n = 1
  ref = Lu_element
FEATURE [App::DocumentObjectGroupPython] G4_Lu  # scripted group (container) (typed FeaturePython)
  Dunit = g/cm3
  Dvalue = 9.84
  Group = -> [Lu_element001]
  conduct = 2
  density = 1
  expand = 3
  formula = Lu
  name = G4_Lu
  specific = 4
FEATURE [App::DocumentObjectGroupPython] Hf_element001  label="Hf_element : 1"  # scripted group (container) (typed FeaturePython)
  n = 1
  ref = Hf_element
FEATURE [App::DocumentObjectGroupPython] G4_Hf  # scripted group (container) (typed FeaturePython)
  Dunit = g/cm3
  Dvalue = 13.31
  Group = -> [Hf_element001]
  conduct = 2
  density = 1
  expand = 3
  formula = Hf
  name = G4_Hf
  specific = 4
FEATURE [App::DocumentObjectGroupPython] Ta_element001  label="Ta_element : 1"  # scripted group (container) (typed FeaturePython)
  n = 1
  ref = Ta_element
FEATURE [App::DocumentObjectGroupPython] G4_Ta  # scripted group (container) (typed FeaturePython)
  Dunit = g/cm3
  Dvalue = 16.654
  Group = -> [Ta_element001]
  conduct = 2
  density = 1
  expand = 3
  formula = Ta
  name = G4_Ta
  specific = 4
FEATURE [App::DocumentObjectGroupPython] W_element004  label="W_element : 004"  # scripted group (container) (typed FeaturePython)
  n = 1
  ref = W_element
FEATURE [App::DocumentObjectGroupPython] G4_W  # scripted group (container) (typed FeaturePython)
  Dunit = g/cm3
  Dvalue = 19.3
  Group = -> [W_element004]
  conduct = 2
  density = 1
  expand = 3
  formula = W
  name = G4_W
  specific = 4
FEATURE [App::DocumentObjectGroupPython] Re_element001  label="Re_element : 1"  # scripted group (container) (typed FeaturePython)
  n = 1
  ref = Re_element
FEATURE [App::DocumentObjectGroupPython] G4_Re  # scripted group (container) (typed FeaturePython)
  Dunit = g/cm3
  Dvalue = 21.02
  Group = -> [Re_element001]
  conduct = 2
  density = 1
  expand = 3
  formula = Re
  name = G4_Re
  specific = 4
FEATURE [App::DocumentObjectGroupPython] Os_element001  label="Os_element : 1"  # scripted group (container) (typed FeaturePython)
  n = 1
  ref = Os_element
FEATURE [App::DocumentObjectGroupPython] G4_Os  # scripted group (container) (typed FeaturePython)
  Dunit = g/cm3
  Dvalue = 22.57
  Group = -> [Os_element001]
  conduct = 2
  density = 1
  expand = 3
  formula = Os
  name = G4_Os
  specific = 4
FEATURE [App::DocumentObjectGroupPython] Ir_element001  label="Ir_element : 1"  # scripted group (container) (typed FeaturePython)
  n = 1
  ref = Ir_element
FEATURE [App::DocumentObjectGroupPython] G4_Ir  # scripted group (container) (typed FeaturePython)
  Dunit = g/cm3
  Dvalue = 22.42
  Group = -> [Ir_element001]
  conduct = 2
  density = 1
  expand = 3
  formula = Ir
  name = G4_Ir
  specific = 4
FEATURE [App::DocumentObjectGroupPython] Pt_element001  label="Pt_element : 1"  # scripted group (container) (typed FeaturePython)
  n = 1
  ref = Pt_element
FEATURE [App::DocumentObjectGroupPython] G4_Pt  # scripted group (container) (typed FeaturePython)
  Dunit = g/cm3
  Dvalue = 21.45
  Group = -> [Pt_element001]
  conduct = 2
  density = 1
  expand = 3
  formula = Pt
  name = G4_Pt
  specific = 4
FEATURE [App::DocumentObjectGroupPython] Au_element001  label="Au_element : 1"  # scripted group (container) (typed FeaturePython)
  n = 1
  ref = Au_element
FEATURE [App::DocumentObjectGroupPython] G4_Au  # scripted group (container) (typed FeaturePython)
  Dunit = g/cm3
  Dvalue = 19.32
  Group = -> [Au_element001]
  conduct = 2
  density = 1
  expand = 3
  formula = Au
  name = G4_Au
  specific = 4
FEATURE [App::DocumentObjectGroupPython] Hg_element002  label="Hg_element : 002"  # scripted group (container) (typed FeaturePython)
  n = 1
  ref = Hg_element
FEATURE [App::DocumentObjectGroupPython] G4_Hg  # scripted group (container) (typed FeaturePython)
  Dunit = g/cm3
  Dvalue = 13.546
  Group = -> [Hg_element002]
  conduct = 2
  density = 1
  expand = 3
  formula = Hg
  name = G4_Hg
  specific = 4
FEATURE [App::DocumentObjectGroupPython] Tl_element002  label="Tl_element : 002"  # scripted group (container) (typed FeaturePython)
  n = 1
  ref = Tl_element
FEATURE [App::DocumentObjectGroupPython] G4_Tl  # scripted group (container) (typed FeaturePython)
  Dunit = g/cm3
  Dvalue = 11.72
  Group = -> [Tl_element002]
  conduct = 2
  density = 1
  expand = 3
  formula = Tl
  name = G4_Tl
  specific = 4
FEATURE [App::DocumentObjectGroupPython] Pb_element003  label="Pb_element : 1"  # scripted group (container) (typed FeaturePython)
  n = 1
  ref = Pb_element
FEATURE [App::DocumentObjectGroupPython] G4_Pb  # scripted group (container) (typed FeaturePython)
  Dunit = g/cm3
  Dvalue = 11.35
  Group = -> [Pb_element003]
  conduct = 2
  density = 1
  expand = 3
  formula = Pb
  name = G4_Pb
  specific = 4
FEATURE [App::DocumentObjectGroupPython] Bi_element002  label="Bi_element : 1"  # scripted group (container) (typed FeaturePython)
  n = 1
  ref = Bi_element
FEATURE [App::DocumentObjectGroupPython] G4_Bi  # scripted group (container) (typed FeaturePython)
  Dunit = g/cm3
  Dvalue = 9.747
  Group = -> [Bi_element002]
  conduct = 2
  density = 1
  expand = 3
  formula = Bi
  name = G4_Bi
  specific = 4
FEATURE [App::DocumentObjectGroupPython] Po_element001  label="Po_element : 1"  # scripted group (container) (typed FeaturePython)
  n = 1
  ref = Po_element
FEATURE [App::DocumentObjectGroupPython] G4_Po  # scripted group (container) (typed FeaturePython)
  Dunit = g/cm3
  Dvalue = 9.32
  Group = -> [Po_element001]
  conduct = 2
  density = 1
  expand = 3
  formula = Po
  name = G4_Po
  specific = 4
FEATURE [App::DocumentObjectGroupPython] At_element001  label="At_element : 1"  # scripted group (container) (typed FeaturePython)
  n = 1
  ref = At_element
FEATURE [App::DocumentObjectGroupPython] G4_At  # scripted group (container) (typed FeaturePython)
  Dunit = g/cm3
  Dvalue = 9.32
  Group = -> [At_element001]
  conduct = 2
  density = 1
  expand = 3
  formula = At
  name = G4_At
  specific = 4
FEATURE [App::DocumentObjectGroupPython] Rn_element001  label="Rn_element : 1"  # scripted group (container) (typed FeaturePython)
  n = 1
  ref = Rn_element
FEATURE [App::DocumentObjectGroupPython] G4_Rn  # scripted group (container) (typed FeaturePython)
  Dunit = g/cm3
  Dvalue = 0.00900662
  Group = -> [Rn_element001]
  conduct = 2
  density = 1
  expand = 3
  formula = Rn
  name = G4_Rn
  specific = 4
FEATURE [App::DocumentObjectGroupPython] Fr_element001  label="Fr_element : 1"  # scripted group (container) (typed FeaturePython)
  n = 1
  ref = Fr_element
FEATURE [App::DocumentObjectGroupPython] G4_Fr  # scripted group (container) (typed FeaturePython)
  Dunit = g/cm3
  Dvalue = 1
  Group = -> [Fr_element001]
  conduct = 2
  density = 1
  expand = 3
  formula = Fr
  name = G4_Fr
  specific = 4
FEATURE [App::DocumentObjectGroupPython] Ra_element001  label="Ra_element : 1"  # scripted group (container) (typed FeaturePython)
  n = 1
  ref = Ra_element
FEATURE [App::DocumentObjectGroupPython] G4_Ra  # scripted group (container) (typed FeaturePython)
  Dunit = g/cm3
  Dvalue = 5
  Group = -> [Ra_element001]
  conduct = 2
  density = 1
  expand = 3
  formula = Ra
  name = G4_Ra
  specific = 4
FEATURE [App::DocumentObjectGroupPython] Ac_element001  label="Ac_element : 1"  # scripted group (container) (typed FeaturePython)
  n = 1
  ref = Ac_element
FEATURE [App::DocumentObjectGroupPython] G4_Ac  # scripted group (container) (typed FeaturePython)
  Dunit = g/cm3
  Dvalue = 10.07
  Group = -> [Ac_element001]
  conduct = 2
  density = 1
  expand = 3
  formula = Ac
  name = G4_Ac
  specific = 4
FEATURE [App::DocumentObjectGroupPython] Th_element001  label="Th_element : 1"  # scripted group (container) (typed FeaturePython)
  n = 1
  ref = Th_element
FEATURE [App::DocumentObjectGroupPython] G4_Th  # scripted group (container) (typed FeaturePython)
  Dunit = g/cm3
  Dvalue = 11.72
  Group = -> [Th_element001]
  conduct = 2
  density = 1
  expand = 3
  formula = Th
  name = G4_Th
  specific = 4
FEATURE [App::DocumentObjectGroupPython] Pa_element001  label="Pa_element : 1"  # scripted group (container) (typed FeaturePython)
  n = 1
  ref = Pa_element
FEATURE [App::DocumentObjectGroupPython] G4_Pa  # scripted group (container) (typed FeaturePython)
  Dunit = g/cm3
  Dvalue = 15.37
  Group = -> [Pa_element001]
  conduct = 2
  density = 1
  expand = 3
  formula = Pa
  name = G4_Pa
  specific = 4
FEATURE [App::DocumentObjectGroupPython] U_element004  label="U_element : 004"  # scripted group (container) (typed FeaturePython)
  n = 1
  ref = U_element
FEATURE [App::DocumentObjectGroupPython] G4_U  # scripted group (container) (typed FeaturePython)
  Dunit = g/cm3
  Dvalue = 18.95
  Group = -> [U_element004]
  conduct = 2
  density = 1
  expand = 3
  formula = U
  name = G4_U
  specific = 4
FEATURE [App::DocumentObjectGroupPython] Np_element001  label="Np_element : 1"  # scripted group (container) (typed FeaturePython)
  n = 1
  ref = Np_element
FEATURE [App::DocumentObjectGroupPython] G4_Np  # scripted group (container) (typed FeaturePython)
  Dunit = g/cm3
  Dvalue = 20.25
  Group = -> [Np_element001]
  conduct = 2
  density = 1
  expand = 3
  formula = Np
  name = G4_Np
  specific = 4
FEATURE [App::DocumentObjectGroupPython] Pu_element002  label="Pu_element : 002"  # scripted group (container) (typed FeaturePython)
  n = 1
  ref = Pu_element
FEATURE [App::DocumentObjectGroupPython] G4_Pu  # scripted group (container) (typed FeaturePython)
  Dunit = g/cm3
  Dvalue = 19.84
  Group = -> [Pu_element002]
  conduct = 2
  density = 1
  expand = 3
  formula = Pu
  name = G4_Pu
  specific = 4
FEATURE [App::DocumentObjectGroupPython] Am_element001  label="Am_element : 1"  # scripted group (container) (typed FeaturePython)
  n = 1
  ref = Am_element
FEATURE [App::DocumentObjectGroupPython] G4_Am  # scripted group (container) (typed FeaturePython)
  Dunit = g/cm3
  Dvalue = 13.67
  Group = -> [Am_element001]
  conduct = 2
  density = 1
  expand = 3
  formula = Am
  name = G4_Am
  specific = 4
FEATURE [App::DocumentObjectGroupPython] Cm_element001  label="Cm_element : 1"  # scripted group (container) (typed FeaturePython)
  n = 1
  ref = Cm_element
FEATURE [App::DocumentObjectGroupPython] G4_Cm  # scripted group (container) (typed FeaturePython)
  Dunit = g/cm3
  Dvalue = 13.51
  Group = -> [Cm_element001]
  conduct = 2
  density = 1
  expand = 3
  formula = Cm
  name = G4_Cm
  specific = 4
FEATURE [App::DocumentObjectGroupPython] Bk_element001  label="Bk_element : 1"  # scripted group (container) (typed FeaturePython)
  n = 1
  ref = Bk_element
FEATURE [App::DocumentObjectGroupPython] G4_Bk  # scripted group (container) (typed FeaturePython)
  Dunit = g/cm3
  Dvalue = 14
  Group = -> [Bk_element001]
  conduct = 2
  density = 1
  expand = 3
  formula = Bk
  name = G4_Bk
  specific = 4
FEATURE [App::DocumentObjectGroupPython] Cf_element001  label="Cf_element : 1"  # scripted group (container) (typed FeaturePython)
  n = 1
  ref = Cf_element
FEATURE [App::DocumentObjectGroupPython] G4_Cf  # scripted group (container) (typed FeaturePython)
  Dunit = g/cm3
  Dvalue = 10
  Group = -> [Cf_element001]
  conduct = 2
  density = 1
  expand = 3
  formula = Cf
  name = G4_Cf
  specific = 4
FEATURE [App::DocumentObjectGroupPython] Element  # scripted group (container) (typed FeaturePython)
  Group = -> [G4_H,G4_He,G4_Li,G4_Be,G4_B,G4_C,G4_N,G4_O,G4_F,G4_Ne,G4_Na,G4_Mg,G4_Al,G4_Si,G4_P,G4_S,G4_Cl,G4_Ar,G4_K,G4_Ca,G4_Sc,G4_Ti,G4_V,G4_Cr,G4_Mn,G4_Fe,G4_Co,G4_Ni,G4_Cu,G4_Zn,G4_Ga,G4_Ge,G4_As,G4_Se,G4_Br,G4_Kr,G4_Rb,G4_Sr,G4_Y,G4_Zr,G4_Nb,G4_Mo,G4_Tc,G4_Ru,G4_Rh,G4_Pd,G4_Ag,G4_Cd,G4_In,G4_Sn,G4_Sb,G4_Te,G4_I,G4_Xe,G4_Cs,G4_Ba,G4_La,G4_Ce,G4_Pr,G4_Nd,G4_Pm,G4_Sm,G4_Eu,G4_Gd,G4_Tb,G4_Dy,G4_Ho,G4_Er,+30 more]
FEATURE [App::DocumentObjectGroupPython] H_element114  label="H_element : 063"  # scripted group (container) (typed FeaturePython)
  n = 2
  ref = H_element
FEATURE [App::DocumentObjectGroupPython] G4_lH2  # scripted group (container) (typed FeaturePython)
  Dunit = g/cm3
  Dvalue = 0.0708
  Group = -> [H_element114]
  conduct = 2
  density = 1
  expand = 3
  formula = G4_lH2
  name = G4_lH2
  specific = 4
FEATURE [App::DocumentObjectGroupPython] N_element049  label="N_element : 022"  # scripted group (container) (typed FeaturePython)
  n = 2
  ref = N_element
FEATURE [App::DocumentObjectGroupPython] G4_lN2  # scripted group (container) (typed FeaturePython)
  Dunit = g/cm3
  Dvalue = 0.807
  Group = -> [N_element049]
  conduct = 2
  density = 1
  expand = 3
  formula = G4_lN2
  name = G4_lN2
  specific = 4
FEATURE [App::DocumentObjectGroupPython] O_element106  label="O_element : 060"  # scripted group (container) (typed FeaturePython)
  n = 2
  ref = O_element
FEATURE [App::DocumentObjectGroupPython] G4_lO2  # scripted group (container) (typed FeaturePython)
  Dunit = g/cm3
  Dvalue = 1.141
  Group = -> [O_element106]
  conduct = 2
  density = 1
  expand = 3
  formula = G4_lO2
  name = G4_lO2
  specific = 4
FEATURE [App::DocumentObjectGroupPython] Ar  label="Ar : 1"  # scripted group (container) (typed FeaturePython)
  n = 1
  ref = Ar
FEATURE [App::DocumentObjectGroupPython] G4_lAr  # scripted group (container) (typed FeaturePython)
  Dunit = g/cm3
  Dvalue = 1.396
  Group = -> [Ar]
  conduct = 2
  density = 1
  expand = 3
  formula = G4_lAr
  name = G4_lAr
  specific = 4
FEATURE [App::DocumentObjectGroupPython] Br  label="Br : 1"  # scripted group (container) (typed FeaturePython)
  n = 1
  ref = Br
FEATURE [App::DocumentObjectGroupPython] G4_lBr  # scripted group (container) (typed FeaturePython)
  Dunit = g/cm3
  Dvalue = 3.1028
  Group = -> [Br]
  conduct = 2
  density = 1
  expand = 3
  formula = G4_lBr
  name = G4_lBr
  specific = 4
FEATURE [App::DocumentObjectGroupPython] Kr  label="Kr : 1"  # scripted group (container) (typed FeaturePython)
  n = 1
  ref = Kr
FEATURE [App::DocumentObjectGroupPython] G4_lKr  # scripted group (container) (typed FeaturePython)
  Dunit = g/cm3
  Dvalue = 2.418
  Group = -> [Kr]
  conduct = 2
  density = 1
  expand = 3
  formula = G4_lKr
  name = G4_lKr
  specific = 4
FEATURE [App::DocumentObjectGroupPython] Xe  label="Xe : 1"  # scripted group (container) (typed FeaturePython)
  n = 1
  ref = Xe
FEATURE [App::DocumentObjectGroupPython] G4_lXe  # scripted group (container) (typed FeaturePython)
  Dunit = g/cm3
  Dvalue = 2.953
  Group = -> [Xe]
  conduct = 2
  density = 1
  expand = 3
  formula = G4_lXe
  name = G4_lXe
  specific = 4
FEATURE [App::DocumentObjectGroupPython] O_element107  label="O_element : 061"  # scripted group (container) (typed FeaturePython)
  n = 4
  ref = O_element
FEATURE [App::DocumentObjectGroupPython] Pb_element004  label="Pb_element : 002"  # scripted group (container) (typed FeaturePython)
  n = 1
  ref = Pb_element
FEATURE [App::DocumentObjectGroupPython] W_element005  label="W_element : 005"  # scripted group (container) (typed FeaturePython)
  n = 1
  ref = W_element
FEATURE [App::DocumentObjectGroupPython] G4_PbWO4  # scripted group (container) (typed FeaturePython)
  Dunit = g/cm3
  Dvalue = 8.28
  Group = -> [O_element107,Pb_element004,W_element005]
  conduct = 2
  density = 1
  expand = 3
  formula = G4_PbWO4
  name = G4_PbWO4
  specific = 4
FEATURE [App::DocumentObjectGroupPython] alactic  label="alactic : 1"  # scripted group (container) (typed FeaturePython)
  n = 1
  ref = alactic
FEATURE [App::DocumentObjectGroupPython] G4_Galactic  # scripted group (container) (typed FeaturePython)
  Dunit = g/cm3
  Dvalue = 0
  Group = -> [alactic]
  conduct = 2
  density = 1
  expand = 3
  formula = G4_Galactic
  name = G4_Galactic
  specific = 4
FEATURE [App::DocumentObjectGroupPython] RAPHITE_POROUS  label="RAPHITE_POROUS : 1"  # scripted group (container) (typed FeaturePython)
  n = 1
  ref = RAPHITE_POROUS
FEATURE [App::DocumentObjectGroupPython] G4_GRAPHITE_POROUS  # scripted group (container) (typed FeaturePython)
  Dunit = g/cm3
  Dvalue = 1.7
  Group = -> [RAPHITE_POROUS]
  conduct = 2
  density = 1
  expand = 3
  formula = G4_GRAPHITE_POROUS
  name = G4_GRAPHITE_POROUS
  specific = 4
FEATURE [App::DocumentObjectGroupPython] H_element115  label="H_element : 0.150"  # scripted group (container) (typed FeaturePython)
  n = 0.080538
FEATURE [App::DocumentObjectGroupPython] C_element125  label="C_element : 0.600"  # scripted group (container) (typed FeaturePython)
  n = 0.599848
FEATURE [App::DocumentObjectGroupPython] O_element108  label="O_element : 0.320"  # scripted group (container) (typed FeaturePython)
  n = 0.319614
FEATURE [App::DocumentObjectGroupPython] G4_LUCITE  # scripted group (container) (typed FeaturePython)
  Dunit = g/cm3
  Dvalue = 1.19
  Group = -> [H_element115,C_element125,O_element108]
  conduct = 2
  density = 1
  expand = 3
  formula = G4_LUCITE
  name = G4_LUCITE
  specific = 4
FEATURE [App::DocumentObjectGroupPython] Cu_element002  label="Cu_element : 62"  # scripted group (container) (typed FeaturePython)
  n = 62
  ref = Cu_element
FEATURE [App::DocumentObjectGroupPython] Zn_element002  label="Zn_element : 35"  # scripted group (container) (typed FeaturePython)
  n = 35
  ref = Zn_element
FEATURE [App::DocumentObjectGroupPython] Pb_element005  label="Pb_element : 3"  # scripted group (container) (typed FeaturePython)
  n = 3
  ref = Pb_element
FEATURE [App::DocumentObjectGroupPython] G4_BRASS  # scripted group (container) (typed FeaturePython)
  Dunit = g/cm3
  Dvalue = 8.52
  Group = -> [Cu_element002,Zn_element002,Pb_element005]
  conduct = 2
  density = 1
  expand = 3
  formula = G4_BRASS
  name = G4_BRASS
  specific = 4
FEATURE [App::DocumentObjectGroupPython] Cu_element003  label="Cu_element : 89"  # scripted group (container) (typed FeaturePython)
  n = 89
  ref = Cu_element
FEATURE [App::DocumentObjectGroupPython] Zn_element003  label="Zn_element : 9"  # scripted group (container) (typed FeaturePython)
  n = 9
  ref = Zn_element
FEATURE [App::DocumentObjectGroupPython] Pb_element006  label="Pb_element : 2"  # scripted group (container) (typed FeaturePython)
  n = 2
  ref = Pb_element
FEATURE [App::DocumentObjectGroupPython] G4_BRONZE  # scripted group (container) (typed FeaturePython)
  Dunit = g/cm3
  Dvalue = 8.82
  Group = -> [Cu_element003,Zn_element003,Pb_element006]
  conduct = 2
  density = 1
  expand = 3
  formula = G4_BRONZE
  name = G4_BRONZE
  specific = 4
FEATURE [App::DocumentObjectGroupPython] Fe_element008  label="Fe_element : 74"  # scripted group (container) (typed FeaturePython)
  n = 74
  ref = Fe_element
FEATURE [App::DocumentObjectGroupPython] Cr_element002  label="Cr_element : 18"  # scripted group (container) (typed FeaturePython)
  n = 18
  ref = Cr_element
FEATURE [App::DocumentObjectGroupPython] Ni_element002  label="Ni_element : 8"  # scripted group (container) (typed FeaturePython)
  n = 8
  ref = Ni_element
FEATURE [App::DocumentObjectGroupPython] G4_STAINLESS_STEEL  label="G4_STAINLESS-STEEL"  # scripted group (container) (typed FeaturePython)
  Dunit = g/cm3
  Dvalue = 8
  Group = -> [Fe_element008,Cr_element002,Ni_element002]
  conduct = 2
  density = 1
  expand = 3
  formula = G4_STAINLESS-STEEL
  name = G4_STAINLESS-STEEL
  specific = 4
FEATURE [App::DocumentObjectGroupPython] H_element116  label="H_element : 064"  # scripted group (container) (typed FeaturePython)
  n = 18
  ref = H_element
FEATURE [App::DocumentObjectGroupPython] C_element126  label="C_element : 071"  # scripted group (container) (typed FeaturePython)
  n = 12
  ref = C_element
FEATURE [App::DocumentObjectGroupPython] O_element109  label="O_element : 062"  # scripted group (container) (typed FeaturePython)
  n = 7
  ref = O_element
FEATURE [App::DocumentObjectGroupPython] G4_CR39  # scripted group (container) (typed FeaturePython)
  Dunit = g/cm3
  Dvalue = 1.32
  Group = -> [H_element116,C_element126,O_element109]
  conduct = 2
  density = 1
  expand = 3
  formula = G4_CR39
  name = G4_CR39
  specific = 4
FEATURE [App::DocumentObjectGroupPython] H_element117  label="H_element : 38"  # scripted group (container) (typed FeaturePython)
  n = 38
  ref = H_element
FEATURE [App::DocumentObjectGroupPython] C_element127  label="C_element : 072"  # scripted group (container) (typed FeaturePython)
  n = 18
  ref = C_element
FEATURE [App::DocumentObjectGroupPython] O_element110  label="O_element : 063"  # scripted group (container) (typed FeaturePython)
  n = 1
  ref = O_element
FEATURE [App::DocumentObjectGroupPython] G4_OCTADECANOL  # scripted group (container) (typed FeaturePython)
  Dunit = g/cm3
  Dvalue = 0.812
  Group = -> [H_element117,C_element127,O_element110]
  conduct = 2
  density = 1
  expand = 3
  formula = G4_OCTADECANOL
  name = G4_OCTADECANOL
  specific = 4
FEATURE [App::DocumentObjectGroupPython] HEP  # scripted group (container) (typed FeaturePython)
  Group = -> [G4_lH2,G4_lN2,G4_lO2,G4_lAr,G4_lBr,G4_lKr,G4_lXe,G4_PbWO4,G4_Galactic,G4_GRAPHITE_POROUS,G4_LUCITE,G4_BRASS,G4_BRONZE,G4_STAINLESS_STEEL,G4_CR39,G4_OCTADECANOL]
FEATURE [App::DocumentObjectGroupPython] C_element128  label="C_element : 073"  # scripted group (container) (typed FeaturePython)
  n = 14
  ref = C_element
FEATURE [App::DocumentObjectGroupPython] H_element118  label="H_element : 065"  # scripted group (container) (typed FeaturePython)
  n = 10
  ref = H_element
FEATURE [App::DocumentObjectGroupPython] O_element111  label="O_element : 064"  # scripted group (container) (typed FeaturePython)
  n = 2
  ref = O_element
FEATURE [App::DocumentObjectGroupPython] N_element050  label="N_element : 023"  # scripted group (container) (typed FeaturePython)
  n = 2
  ref = N_element
FEATURE [App::DocumentObjectGroupPython] G4_KEVLAR  # scripted group (container) (typed FeaturePython)
  Dunit = g/cm3
  Dvalue = 1.44
  Group = -> [C_element128,H_element118,O_element111,N_element050]
  conduct = 2
  density = 1
  expand = 3
  formula = G4_KEVLAR
  name = G4_KEVLAR
  specific = 4
FEATURE [App::DocumentObjectGroupPython] C_element129  label="C_element : 074"  # scripted group (container) (typed FeaturePython)
  n = 10
  ref = C_element
FEATURE [App::DocumentObjectGroupPython] H_element119  label="H_element : 066"  # scripted group (container) (typed FeaturePython)
  n = 8
  ref = H_element
FEATURE [App::DocumentObjectGroupPython] O_element112  label="O_element : 065"  # scripted group (container) (typed FeaturePython)
  n = 4
  ref = O_element
FEATURE [App::DocumentObjectGroupPython] G4_DACRON  # scripted group (container) (typed FeaturePython)
  Dunit = g/cm3
  Dvalue = 1.4
  Group = -> [C_element129,H_element119,O_element112]
  conduct = 2
  density = 1
  expand = 3
  formula = G4_DACRON
  name = G4_DACRON
  specific = 4
FEATURE [App::DocumentObjectGroupPython] C_element130  label="C_element : 075"  # scripted group (container) (typed FeaturePython)
  n = 4
  ref = C_element
FEATURE [App::DocumentObjectGroupPython] H_element120  label="H_element : 067"  # scripted group (container) (typed FeaturePython)
  n = 5
  ref = H_element
FEATURE [App::DocumentObjectGroupPython] Cl_element030  label="Cl_element : 016"  # scripted group (container) (typed FeaturePython)
  n = 1
  ref = Cl_element
FEATURE [App::DocumentObjectGroupPython] G4_NEOPRENE  # scripted group (container) (typed FeaturePython)
  Dunit = g/cm3
  Dvalue = 1.23
  Group = -> [C_element130,H_element120,Cl_element030]
  conduct = 2
  density = 1
  expand = 3
  formula = G4_NEOPRENE
  name = G4_NEOPRENE
  specific = 4
FEATURE [App::DocumentObjectGroupPython] Space  # scripted group (container) (typed FeaturePython)
  Group = -> [G4_KEVLAR,G4_DACRON,G4_NEOPRENE]
FEATURE [App::DocumentObjectGroupPython] H_element121  label="H_element : 068"  # scripted group (container) (typed FeaturePython)
  n = 5
  ref = H_element
FEATURE [App::DocumentObjectGroupPython] C_element131  label="C_element : 076"  # scripted group (container) (typed FeaturePython)
  n = 4
  ref = C_element
FEATURE [App::DocumentObjectGroupPython] N_element051  label="N_element : 3"  # scripted group (container) (typed FeaturePython)
  n = 3
  ref = N_element
FEATURE [App::DocumentObjectGroupPython] O_element113  label="O_element : 066"  # scripted group (container) (typed FeaturePython)
  n = 1
  ref = O_element
FEATURE [App::DocumentObjectGroupPython] G4_CYTOSINE  # scripted group (container) (typed FeaturePython)
  Dunit = g/cm3
  Dvalue = 1.55
  Group = -> [H_element121,C_element131,N_element051,O_element113]
  conduct = 2
  density = 1
  expand = 3
  formula = G4_CYTOSINE
  name = G4_CYTOSINE
  specific = 4
FEATURE [App::DocumentObjectGroupPython] H_element122  label="H_element : 069"  # scripted group (container) (typed FeaturePython)
  n = 6
  ref = H_element
FEATURE [App::DocumentObjectGroupPython] C_element132  label="C_element : 077"  # scripted group (container) (typed FeaturePython)
  n = 5
  ref = C_element
FEATURE [App::DocumentObjectGroupPython] N_element052  label="N_element : 024"  # scripted group (container) (typed FeaturePython)
  n = 2
  ref = N_element
FEATURE [App::DocumentObjectGroupPython] O_element114  label="O_element : 067"  # scripted group (container) (typed FeaturePython)
  n = 2
  ref = O_element
FEATURE [App::DocumentObjectGroupPython] G4_THYMINE  # scripted group (container) (typed FeaturePython)
  Dunit = g/cm3
  Dvalue = 1.23
  Group = -> [H_element122,C_element132,N_element052,O_element114]
  conduct = 2
  density = 1
  expand = 3
  formula = G4_THYMINE
  name = G4_THYMINE
  specific = 4
FEATURE [App::DocumentObjectGroupPython] H_element123  label="H_element : 070"  # scripted group (container) (typed FeaturePython)
  n = 4
  ref = H_element
FEATURE [App::DocumentObjectGroupPython] C_element133  label="C_element : 078"  # scripted group (container) (typed FeaturePython)
  n = 4
  ref = C_element
FEATURE [App::DocumentObjectGroupPython] N_element053  label="N_element : 025"  # scripted group (container) (typed FeaturePython)
  n = 2
  ref = N_element
FEATURE [App::DocumentObjectGroupPython] O_element115  label="O_element : 068"  # scripted group (container) (typed FeaturePython)
  n = 2
  ref = O_element
FEATURE [App::DocumentObjectGroupPython] G4_URACIL  # scripted group (container) (typed FeaturePython)
  Dunit = g/cm3
  Dvalue = 1.32
  Group = -> [H_element123,C_element133,N_element053,O_element115]
  conduct = 2
  density = 1
  expand = 3
  formula = G4_URACIL
  name = G4_URACIL
  specific = 4
FEATURE [App::DocumentObjectGroupPython] H_element124  label="H_element : 071"  # scripted group (container) (typed FeaturePython)
  n = 4
  ref = H_element
FEATURE [App::DocumentObjectGroupPython] C_element134  label="C_element : 079"  # scripted group (container) (typed FeaturePython)
  n = 5
  ref = C_element
FEATURE [App::DocumentObjectGroupPython] N_element054  label="N_element : 026"  # scripted group (container) (typed FeaturePython)
  n = 5
  ref = N_element
FEATURE [App::DocumentObjectGroupPython] G4_DNA_ADENINE  # scripted group (container) (typed FeaturePython)
  Dunit = g/cm3
  Dvalue = 1
  Group = -> [H_element124,C_element134,N_element054]
  conduct = 2
  density = 1
  expand = 3
  formula = G4_DNA_ADENINE
  name = G4_DNA_ADENINE
  specific = 4
FEATURE [App::DocumentObjectGroupPython] H_element125  label="H_element : 072"  # scripted group (container) (typed FeaturePython)
  n = 4
  ref = H_element
FEATURE [App::DocumentObjectGroupPython] C_element135  label="C_element : 080"  # scripted group (container) (typed FeaturePython)
  n = 5
  ref = C_element
FEATURE [App::DocumentObjectGroupPython] N_element055  label="N_element : 027"  # scripted group (container) (typed FeaturePython)
  n = 5
  ref = N_element
FEATURE [App::DocumentObjectGroupPython] O_element116  label="O_element : 069"  # scripted group (container) (typed FeaturePython)
  n = 1
  ref = O_element
FEATURE [App::DocumentObjectGroupPython] G4_DNA_GUANINE  # scripted group (container) (typed FeaturePython)
  Dunit = g/cm3
  Dvalue = 1
  Group = -> [H_element125,C_element135,N_element055,O_element116]
  conduct = 2
  density = 1
  expand = 3
  formula = G4_DNA_GUANINE
  name = G4_DNA_GUANINE
  specific = 4
FEATURE [App::DocumentObjectGroupPython] H_element126  label="H_element : 073"  # scripted group (container) (typed FeaturePython)
  n = 4
  ref = H_element
FEATURE [App::DocumentObjectGroupPython] C_element136  label="C_element : 081"  # scripted group (container) (typed FeaturePython)
  n = 4
  ref = C_element
FEATURE [App::DocumentObjectGroupPython] N_element056  label="N_element : 028"  # scripted group (container) (typed FeaturePython)
  n = 3
  ref = N_element
FEATURE [App::DocumentObjectGroupPython] O_element117  label="O_element : 070"  # scripted group (container) (typed FeaturePython)
  n = 1
  ref = O_element
FEATURE [App::DocumentObjectGroupPython] G4_DNA_CYTOSINE  # scripted group (container) (typed FeaturePython)
  Dunit = g/cm3
  Dvalue = 1
  Group = -> [H_element126,C_element136,N_element056,O_element117]
  conduct = 2
  density = 1
  expand = 3
  formula = G4_DNA_CYTOSINE
  name = G4_DNA_CYTOSINE
  specific = 4
FEATURE [App::DocumentObjectGroupPython] H_element127  label="H_element : 074"  # scripted group (container) (typed FeaturePython)
  n = 5
  ref = H_element
FEATURE [App::DocumentObjectGroupPython] C_element137  label="C_element : 082"  # scripted group (container) (typed FeaturePython)
  n = 5
  ref = C_element
FEATURE [App::DocumentObjectGroupPython] N_element057  label="N_element : 029"  # scripted group (container) (typed FeaturePython)
  n = 2
  ref = N_element
FEATURE [App::DocumentObjectGroupPython] O_element118  label="O_element : 071"  # scripted group (container) (typed FeaturePython)
  n = 2
  ref = O_element
FEATURE [App::DocumentObjectGroupPython] G4_DNA_THYMINE  # scripted group (container) (typed FeaturePython)
  Dunit = g/cm3
  Dvalue = 1
  Group = -> [H_element127,C_element137,N_element057,O_element118]
  conduct = 2
  density = 1
  expand = 3
  formula = G4_DNA_THYMINE
  name = G4_DNA_THYMINE
  specific = 4
FEATURE [App::DocumentObjectGroupPython] H_element128  label="H_element : 075"  # scripted group (container) (typed FeaturePython)
  n = 3
  ref = H_element
FEATURE [App::DocumentObjectGroupPython] C_element138  label="C_element : 083"  # scripted group (container) (typed FeaturePython)
  n = 4
  ref = C_element
FEATURE [App::DocumentObjectGroupPython] N_element058  label="N_element : 030"  # scripted group (container) (typed FeaturePython)
  n = 2
  ref = N_element
FEATURE [App::DocumentObjectGroupPython] O_element119  label="O_element : 072"  # scripted group (container) (typed FeaturePython)
  n = 2
  ref = O_element
FEATURE [App::DocumentObjectGroupPython] G4_DNA_URACIL  # scripted group (container) (typed FeaturePython)
  Dunit = g/cm3
  Dvalue = 1
  Group = -> [H_element128,C_element138,N_element058,O_element119]
  conduct = 2
  density = 1
  expand = 3
  formula = G4_DNA_URACIL
  name = G4_DNA_URACIL
  specific = 4
FEATURE [App::DocumentObjectGroupPython] H_element129  label="H_element : 076"  # scripted group (container) (typed FeaturePython)
  n = 10
  ref = H_element
FEATURE [App::DocumentObjectGroupPython] C_element139  label="C_element : 084"  # scripted group (container) (typed FeaturePython)
  n = 10
  ref = C_element
FEATURE [App::DocumentObjectGroupPython] N_element059  label="N_element : 031"  # scripted group (container) (typed FeaturePython)
  n = 5
  ref = N_element
FEATURE [App::DocumentObjectGroupPython] O_element120  label="O_element : 073"  # scripted group (container) (typed FeaturePython)
  n = 4
  ref = O_element
FEATURE [App::DocumentObjectGroupPython] G4_DNA_ADENOSINE  # scripted group (container) (typed FeaturePython)
  Dunit = g/cm3
  Dvalue = 1
  Group = -> [H_element129,C_element139,N_element059,O_element120]
  conduct = 2
  density = 1
  expand = 3
  formula = G4_DNA_ADENOSINE
  name = G4_DNA_ADENOSINE
  specific = 4
FEATURE [App::DocumentObjectGroupPython] H_element130  label="H_element : 077"  # scripted group (container) (typed FeaturePython)
  n = 10
  ref = H_element
FEATURE [App::DocumentObjectGroupPython] C_element140  label="C_element : 085"  # scripted group (container) (typed FeaturePython)
  n = 10
  ref = C_element
FEATURE [App::DocumentObjectGroupPython] N_element060  label="N_element : 032"  # scripted group (container) (typed FeaturePython)
  n = 5
  ref = N_element
FEATURE [App::DocumentObjectGroupPython] O_element121  label="O_element : 074"  # scripted group (container) (typed FeaturePython)
  n = 5
  ref = O_element
FEATURE [App::DocumentObjectGroupPython] G4_DNA_GUANOSINE  # scripted group (container) (typed FeaturePython)
  Dunit = g/cm3
  Dvalue = 1
  Group = -> [H_element130,C_element140,N_element060,O_element121]
  conduct = 2
  density = 1
  expand = 3
  formula = G4_DNA_GUANOSINE
  name = G4_DNA_GUANOSINE
  specific = 4
FEATURE [App::DocumentObjectGroupPython] H_element131  label="H_element : 078"  # scripted group (container) (typed FeaturePython)
  n = 10
  ref = H_element
FEATURE [App::DocumentObjectGroupPython] C_element141  label="C_element : 086"  # scripted group (container) (typed FeaturePython)
  n = 9
  ref = C_element
FEATURE [App::DocumentObjectGroupPython] N_element061  label="N_element : 033"  # scripted group (container) (typed FeaturePython)
  n = 3
  ref = N_element
FEATURE [App::DocumentObjectGroupPython] O_element122  label="O_element : 075"  # scripted group (container) (typed FeaturePython)
  n = 5
  ref = O_element
FEATURE [App::DocumentObjectGroupPython] G4_DNA_CYTIDINE  # scripted group (container) (typed FeaturePython)
  Dunit = g/cm3
  Dvalue = 1
  Group = -> [H_element131,C_element141,N_element061,O_element122]
  conduct = 2
  density = 1
  expand = 3
  formula = G4_DNA_CYTIDINE
  name = G4_DNA_CYTIDINE
  specific = 4
FEATURE [App::DocumentObjectGroupPython] H_element132  label="H_element : 079"  # scripted group (container) (typed FeaturePython)
  n = 9
  ref = H_element
FEATURE [App::DocumentObjectGroupPython] C_element142  label="C_element : 087"  # scripted group (container) (typed FeaturePython)
  n = 9
  ref = C_element
FEATURE [App::DocumentObjectGroupPython] N_element062  label="N_element : 034"  # scripted group (container) (typed FeaturePython)
  n = 2
  ref = N_element
FEATURE [App::DocumentObjectGroupPython] O_element123  label="O_element : 076"  # scripted group (container) (typed FeaturePython)
  n = 6
  ref = O_element
FEATURE [App::DocumentObjectGroupPython] G4_DNA_URIDINE  # scripted group (container) (typed FeaturePython)
  Dunit = g/cm3
  Dvalue = 1
  Group = -> [H_element132,C_element142,N_element062,O_element123]
  conduct = 2
  density = 1
  expand = 3
  formula = G4_DNA_URIDINE
  name = G4_DNA_URIDINE
  specific = 4
FEATURE [App::DocumentObjectGroupPython] H_element133  label="H_element : 080"  # scripted group (container) (typed FeaturePython)
  n = 11
  ref = H_element
FEATURE [App::DocumentObjectGroupPython] C_element143  label="C_element : 088"  # scripted group (container) (typed FeaturePython)
  n = 10
  ref = C_element
FEATURE [App::DocumentObjectGroupPython] N_element063  label="N_element : 035"  # scripted group (container) (typed FeaturePython)
  n = 2
  ref = N_element
FEATURE [App::DocumentObjectGroupPython] O_element124  label="O_element : 077"  # scripted group (container) (typed FeaturePython)
  n = 6
  ref = O_element
FEATURE [App::DocumentObjectGroupPython] G4_DNA_METHYLURIDINE  # scripted group (container) (typed FeaturePython)
  Dunit = g/cm3
  Dvalue = 1
  Group = -> [H_element133,C_element143,N_element063,O_element124]
  conduct = 2
  density = 1
  expand = 3
  formula = G4_DNA_METHYLURIDINE
  name = G4_DNA_METHYLURIDINE
  specific = 4
FEATURE [App::DocumentObjectGroupPython] P_element014  label="P_element : 003"  # scripted group (container) (typed FeaturePython)
  n = 1
  ref = P_element
FEATURE [App::DocumentObjectGroupPython] O_element125  label="O_element : 078"  # scripted group (container) (typed FeaturePython)
  n = 3
  ref = O_element
FEATURE [App::DocumentObjectGroupPython] G4_DNA_MONOPHOSPHATE  # scripted group (container) (typed FeaturePython)
  Dunit = g/cm3
  Dvalue = 1
  Group = -> [P_element014,O_element125]
  conduct = 2
  density = 1
  expand = 3
  formula = G4_DNA_MONOPHOSPHATE
  name = G4_DNA_MONOPHOSPHATE
  specific = 4
FEATURE [App::DocumentObjectGroupPython] H_element134  label="H_element : 081"  # scripted group (container) (typed FeaturePython)
  n = 10
  ref = H_element
FEATURE [App::DocumentObjectGroupPython] C_element144  label="C_element : 089"  # scripted group (container) (typed FeaturePython)
  n = 10
  ref = C_element
FEATURE [App::DocumentObjectGroupPython] N_element064  label="N_element : 036"  # scripted group (container) (typed FeaturePython)
  n = 5
  ref = N_element
FEATURE [App::DocumentObjectGroupPython] O_element126  label="O_element : 079"  # scripted group (container) (typed FeaturePython)
  n = 7
  ref = O_element
FEATURE [App::DocumentObjectGroupPython] P_element015  label="P_element : 004"  # scripted group (container) (typed FeaturePython)
  n = 1
  ref = P_element
FEATURE [App::DocumentObjectGroupPython] G4_DNA_A  # scripted group (container) (typed FeaturePython)
  Dunit = g/cm3
  Dvalue = 1
  Group = -> [H_element134,C_element144,N_element064,O_element126,P_element015]
  conduct = 2
  density = 1
  expand = 3
  formula = G4_DNA_A
  name = G4_DNA_A
  specific = 4
FEATURE [App::DocumentObjectGroupPython] H_element135  label="H_element : 082"  # scripted group (container) (typed FeaturePython)
  n = 10
  ref = H_element
FEATURE [App::DocumentObjectGroupPython] C_element145  label="C_element : 090"  # scripted group (container) (typed FeaturePython)
  n = 10
  ref = C_element
FEATURE [App::DocumentObjectGroupPython] N_element065  label="N_element : 037"  # scripted group (container) (typed FeaturePython)
  n = 5
  ref = N_element
FEATURE [App::DocumentObjectGroupPython] O_element127  label="O_element : 8"  # scripted group (container) (typed FeaturePython)
  n = 8
  ref = O_element
FEATURE [App::DocumentObjectGroupPython] P_element016  label="P_element : 005"  # scripted group (container) (typed FeaturePython)
  n = 1
  ref = P_element
FEATURE [App::DocumentObjectGroupPython] G4_DNA_G  # scripted group (container) (typed FeaturePython)
  Dunit = g/cm3
  Dvalue = 1
  Group = -> [H_element135,C_element145,N_element065,O_element127,P_element016]
  conduct = 2
  density = 1
  expand = 3
  formula = G4_DNA_G
  name = G4_DNA_G
  specific = 4
FEATURE [App::DocumentObjectGroupPython] H_element136  label="H_element : 083"  # scripted group (container) (typed FeaturePython)
  n = 10
  ref = H_element
FEATURE [App::DocumentObjectGroupPython] C_element146  label="C_element : 091"  # scripted group (container) (typed FeaturePython)
  n = 9
  ref = C_element
FEATURE [App::DocumentObjectGroupPython] N_element066  label="N_element : 038"  # scripted group (container) (typed FeaturePython)
  n = 3
  ref = N_element
FEATURE [App::DocumentObjectGroupPython] O_element128  label="O_element : 080"  # scripted group (container) (typed FeaturePython)
  n = 8
  ref = O_element
FEATURE [App::DocumentObjectGroupPython] P_element017  label="P_element : 006"  # scripted group (container) (typed FeaturePython)
  n = 1
  ref = P_element
FEATURE [App::DocumentObjectGroupPython] G4_DNA_C  # scripted group (container) (typed FeaturePython)
  Dunit = g/cm3
  Dvalue = 1
  Group = -> [H_element136,C_element146,N_element066,O_element128,P_element017]
  conduct = 2
  density = 1
  expand = 3
  formula = G4_DNA_C
  name = G4_DNA_C
  specific = 4
FEATURE [App::DocumentObjectGroupPython] H_element137  label="H_element : 084"  # scripted group (container) (typed FeaturePython)
  n = 9
  ref = H_element
FEATURE [App::DocumentObjectGroupPython] C_element147  label="C_element : 092"  # scripted group (container) (typed FeaturePython)
  n = 9
  ref = C_element
FEATURE [App::DocumentObjectGroupPython] N_element067  label="N_element : 039"  # scripted group (container) (typed FeaturePython)
  n = 2
  ref = N_element
FEATURE [App::DocumentObjectGroupPython] O_element129  label="O_element : 9"  # scripted group (container) (typed FeaturePython)
  n = 9
  ref = O_element
FEATURE [App::DocumentObjectGroupPython] P_element018  label="P_element : 007"  # scripted group (container) (typed FeaturePython)
  n = 1
  ref = P_element
FEATURE [App::DocumentObjectGroupPython] G4_DNA_U  # scripted group (container) (typed FeaturePython)
  Dunit = g/cm3
  Dvalue = 1
  Group = -> [H_element137,C_element147,N_element067,O_element129,P_element018]
  conduct = 2
  density = 1
  expand = 3
  formula = G4_DNA_U
  name = G4_DNA_U
  specific = 4
FEATURE [App::DocumentObjectGroupPython] H_element138  label="H_element : 085"  # scripted group (container) (typed FeaturePython)
  n = 11
  ref = H_element
FEATURE [App::DocumentObjectGroupPython] C_element148  label="C_element : 093"  # scripted group (container) (typed FeaturePython)
  n = 10
  ref = C_element
FEATURE [App::DocumentObjectGroupPython] N_element068  label="N_element : 040"  # scripted group (container) (typed FeaturePython)
  n = 2
  ref = N_element
FEATURE [App::DocumentObjectGroupPython] O_element130  label="O_element : 081"  # scripted group (container) (typed FeaturePython)
  n = 9
  ref = O_element
FEATURE [App::DocumentObjectGroupPython] P_element019  label="P_element : 008"  # scripted group (container) (typed FeaturePython)
  n = 1
  ref = P_element
FEATURE [App::DocumentObjectGroupPython] G4_DNA_MU  # scripted group (container) (typed FeaturePython)
  Dunit = g/cm3
  Dvalue = 1
  Group = -> [H_element138,C_element148,N_element068,O_element130,P_element019]
  conduct = 2
  density = 1
  expand = 3
  formula = G4_DNA_MU
  name = G4_DNA_MU
  specific = 4
FEATURE [App::DocumentObjectGroupPython] BioChemical  # scripted group (container) (typed FeaturePython)
  Group = -> [G4_CYTOSINE,G4_THYMINE,G4_URACIL,G4_DNA_ADENINE,G4_DNA_GUANINE,G4_DNA_CYTOSINE,G4_DNA_THYMINE,G4_DNA_URACIL,G4_DNA_ADENOSINE,G4_DNA_GUANOSINE,G4_DNA_CYTIDINE,G4_DNA_URIDINE,G4_DNA_METHYLURIDINE,G4_DNA_MONOPHOSPHATE,G4_DNA_A,G4_DNA_G,G4_DNA_C,G4_DNA_U,G4_DNA_MU]
FEATURE [App::DocumentObjectGroupPython] G4Materials  # scripted group (container) (typed FeaturePython)
  Group = -> [NIST,Element,HEP,Space,BioChemical]
  version = 1
FEATURE [App::DocumentObjectGroupPython] Geant4  # scripted group (container) (typed FeaturePython)
  Group = -> [G4Isotopes,G4Elements,G4Materials]
FEATURE [App::DocumentObjectGroupPython] Materials  # scripted group (container) (typed FeaturePython)
  Group = -> [Geant4]
FEATURE [Part::FeaturePython] GDMLBox_WorldBox  # WARN: FeaturePython — macro-defined, semantics opaque (R4)
  lunit = 2
  material = 5
  x = 200
  y = 200
  z = 200
FEATURE [Part::FeaturePython] GDMLSphere_Sphere  # WARN: FeaturePython — macro-defined, semantics opaque (R4)
  Placement = pos=(20,0,0) rot=(0,0,1;0rad)
  aunit = 0
  deltaphi = 2.02
  deltatheta = 2.02
  lunit = 2
  material = 18
  rmax = 20
  rmin = 10
  startphi = 0
  starttheta = 0
FEATURE [Part::FeaturePython] GDMLTorus_Torus  # WARN: FeaturePython — macro-defined, semantics opaque (R4)
  aunit = deg
  deltaphi = 360
  lunit = 2
  material = 5
  rmax = 5
  rmin = 0
  rtor = 10
  startphi = 10
FEATURE [Part::MultiFuse] Fusion
  Placement = pos=(30,0,0) rot=(0,0,1;0rad)
  Shapes = -> [GDMLSphere_Sphere,GDMLTorus_Torus]
  material = 18
FEATURE [Part::FeaturePython] Array  # Draft array (typed FeaturePython)
  Angle = 360
  ArrayType = 1
  Axis = (0,0,1)
  Base = -> Fusion
  Center = (0,0,0)
  Fuse = false
  IntervalAxis = (0,0,0)
  IntervalX = (50,0,0)
  IntervalY = (0,50,0)
  IntervalZ = (0,0,50)
  NumberCircles = 3
  NumberPolar = 5
  NumberX = 2
  NumberY = 2
  NumberZ = 1
  RadialDistance = 50
  Symmetry = 1
  TangentialDistance = 25
  material = 261
FEATURE [App::Part] Part
  Group = -> [GDMLSphere_Sphere,GDMLTorus_Torus,Fusion,Array]
  Origin = -> Origin001
FEATURE [App::Part] worldVOL
  Group = -> [GDMLBox_WorldBox,Part]
  Origin = -> Origin
